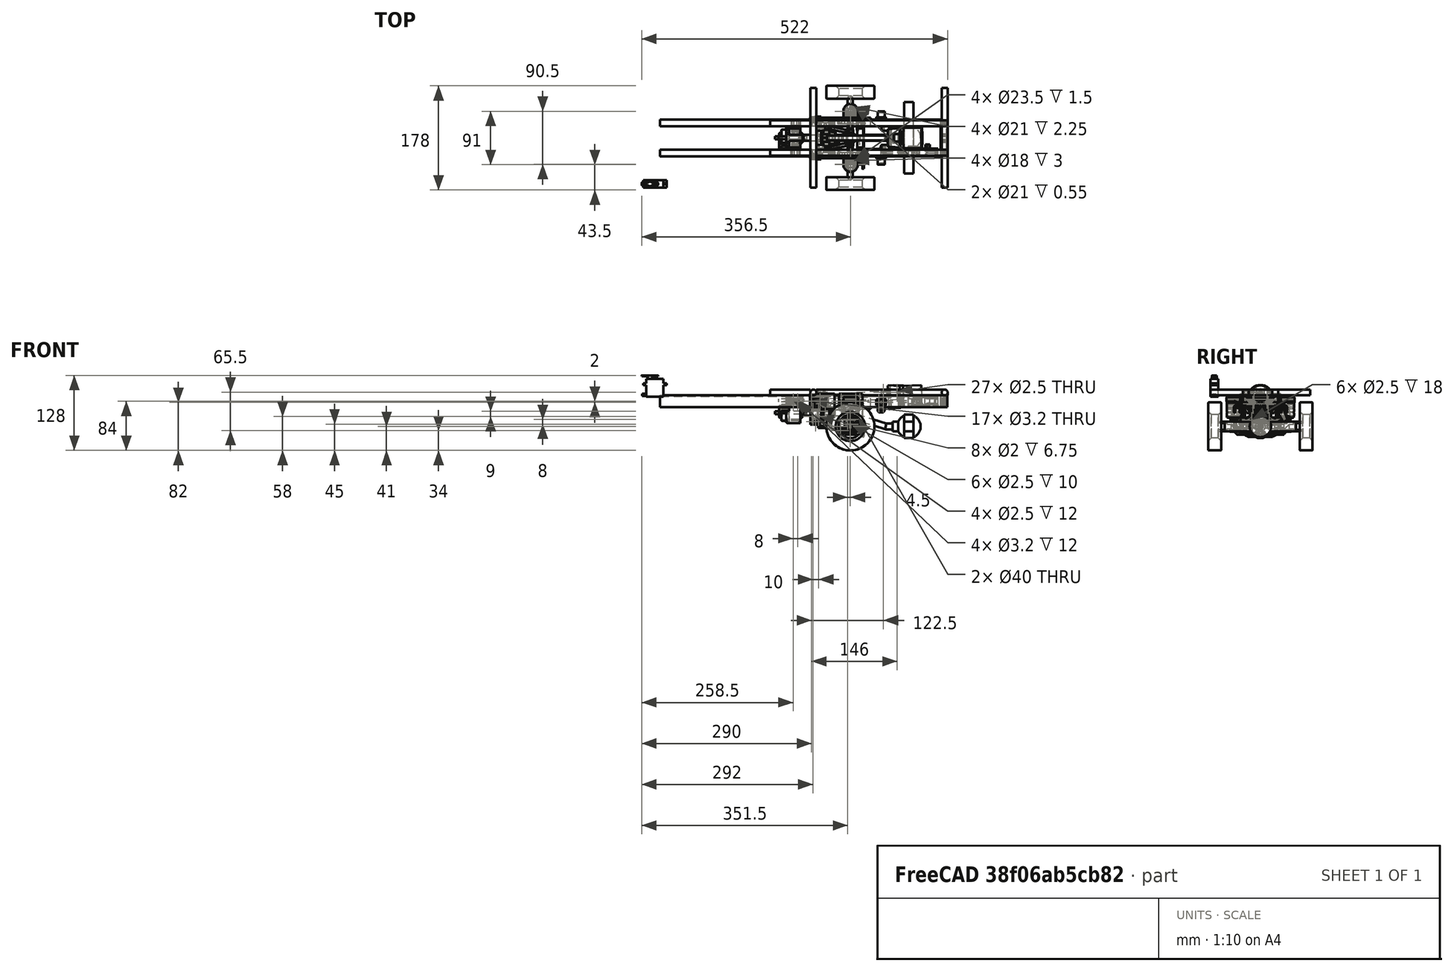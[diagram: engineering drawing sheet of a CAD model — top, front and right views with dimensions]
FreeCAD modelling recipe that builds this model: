
FCSTD DOCUMENT  (FreeCAD 0.17R13522 (Git))
Label: central-axle-lift-02
License: All rights reserved
LicenseURL: http://en.wikipedia.org/wiki/All_rights_reserved
objects: Part::Cylinder×338, Part::Box×195, Part::MultiFuse×193, Part::Cut×182, Part::Fillet×66, Part::Chamfer×49, Part::Torus×34, Part::Mirroring×14, Part::Feature×13, Part::Loft×6, App::DocumentObjectGroup×6, Part::Cone×3, Part::Sphere×1, Part::Extrusion×1
note: 1095 computed .brp shape members not serialized (recipe doc carries the construction recipe); baked Part::Feature solids carry a one-line shape summary decoded from their .brp

FEATURE [Part::Box] Box416  label="Cube641"
  AttacherType = Attacher::AttachEngine3D
  Height = 20
  Length = 490
  Placement = pos=(0,0,-92) rot=(0,0,1;0rad)
  Width = 11.5
FEATURE [Part::Box] Box417  label="Cube642"
  AttacherType = Attacher::AttachEngine3D
  Height = 17
  Length = 490
  Placement = pos=(0,1.5,-90.5) rot=(0,0,1;0rad)
  Width = 10
FEATURE [Part::Cut] Cut429  label="Cut768"
  Base = -> Box416
  Refine = true
  Tool = -> Box417
FEATURE [Part::Fillet] Fillet268
  Base = -> Cut429
  Edges = 2 edges r=3: [Edge11,Edge23]
  Placement = pos=(0,-1.5,0) rot=(0,0,1;0rad)
FEATURE [Part::Box] Box418  label="Cube643"
  AttacherType = Attacher::AttachEngine3D
  Height = 20
  Length = 490
  Placement = pos=(0,0,-92) rot=(0,0,1;0rad)
  Width = 11.5
FEATURE [Part::Box] Box419  label="Cube644"
  AttacherType = Attacher::AttachEngine3D
  Height = 17
  Length = 490
  Placement = pos=(0,1.5,-90.5) rot=(0,0,1;0rad)
  Width = 10
FEATURE [Part::Cut] Cut430  label="Cut769"
  Base = -> Box418
  Refine = true
  Tool = -> Box419
FEATURE [Part::Fillet] Fillet269
  Base = -> Cut430
  Edges = 2 edges r=3: [Edge11,Edge23]
FEATURE [Part::Mirroring] Part__Mirroring036  label="Fillet269 (Mirror #29)"
  Base = (0,0,0)
  Normal = (0,1,0)
  Placement = pos=(0,61.5,0) rot=(0,0,1;0rad)
  Source = -> Fillet269
FEATURE [Part::MultiFuse] Fusion231  label="frame-00"
  Placement = pos=(23.5,55,74) rot=(0,0,1;0rad)
  Refine = true
  Shapes = -> [Part__Mirroring036,Fillet268]
FEATURE [Part::Box] Box494  label="Cube696"
  AttacherType = Attacher::AttachEngine3D
  Height = 10
  Length = 15
  Placement = pos=(340.5,44.5,-63) rot=(0,0,1;0rad)
  Width = 7
FEATURE [Part::Cylinder] Cylinder766  label="Cylinder982"
  Angle = 360
  AttacherType = Attacher::AttachEngine3D
  Height = 10
  Placement = pos=(0,0,0) rot=(0,1,0;1.5708rad)
  Radius = 1.5
FEATURE [Part::Cylinder] Cylinder767  label="Cylinder983"
  Angle = 360
  AttacherType = Attacher::AttachEngine3D
  Height = 10
  Placement = pos=(0,74,0) rot=(0,1,0;1.5708rad)
  Radius = 1.5
FEATURE [Part::MultiFuse] Fusion498
  Placement = pos=(335,48,-59) rot=(0,0,1;0rad)
  Refine = true
  Shapes = -> [Cylinder767,Cylinder766]
FEATURE [Part::Box] Box495  label="Cube697"
  AttacherType = Attacher::AttachEngine3D
  Height = 8
  Length = 9
  Placement = pos=(343.5,28.5,-55) rot=(0,0,1;0rad)
  Width = 7
FEATURE [Part::Box] Box496  label="Cube698"
  AttacherType = Attacher::AttachEngine3D
  Height = 8
  Length = 9
  Placement = pos=(343.5,43.5,-63) rot=(0,0,1;0rad)
  Width = 83
FEATURE [Part::Box] Box497  label="Cube699"
  AttacherType = Attacher::AttachEngine3D
  Height = 8
  Length = 9
  Placement = pos=(343.5,134.5,-55) rot=(0,0,1;0rad)
  Width = 7
FEATURE [Part::Box] Box498  label="Cube700"
  AttacherType = Attacher::AttachEngine3D
  Height = 16
  Length = 9
  Placement = pos=(343.5,13.5,-59) rot=(0,0,1;0rad)
  Width = 15
FEATURE [Part::Box] Box499  label="Cube701"
  AttacherType = Attacher::AttachEngine3D
  Height = 16
  Length = 9
  Placement = pos=(343.5,141.5,-59) rot=(0,0,1;0rad)
  Width = 15
FEATURE [Part::MultiFuse] Fusion499
  Refine = true
  Shapes = -> [Box495,Box498]
FEATURE [Part::MultiFuse] Fusion500
  Refine = true
  Shapes = -> [Box499,Box497]
FEATURE [Part::Box] Box501  label="Cube703"
  AttacherType = Attacher::AttachEngine3D
  Height = 11
  Length = 9
  Placement = pos=(343.5,144,-56.5) rot=(0,0,1;0rad)
  Width = 15
FEATURE [Part::Feature] Face040
  shape: bbox 9.9 x 2e-07 x 8.8 mm, 1 faces, 0 solids (baked)
FEATURE [Part::Feature] Face041
  shape: bbox 9.9 x 2e-07 x 8.8 mm, 1 faces, 0 solids (baked)
FEATURE [Part::Loft] Loft016
  Closed = false
  MaxDegree = 5
  Ruled = false
  Sections = -> [Face040,Face041]
  Solid = true
FEATURE [Part::Feature] Face042
  shape: bbox 9.9 x 2e-07 x 8.8 mm, 1 faces, 0 solids (baked)
FEATURE [Part::Feature] Face043
  shape: bbox 9.9 x 2e-07 x 8.8 mm, 1 faces, 0 solids (baked)
FEATURE [Part::Loft] Loft017
  Closed = false
  MaxDegree = 5
  Ruled = false
  Sections = -> [Face042,Face043]
  Solid = true
FEATURE [Part::MultiFuse] Fusion501
  Refine = true
  Shapes = -> [Fusion499,Loft016]
FEATURE [Part::MultiFuse] Fusion502
  Refine = true
  Shapes = -> [Fusion500,Loft017]
FEATURE [Part::MultiFuse] Fusion503
  Refine = true
  Shapes = -> [Fusion501,Box496,Fusion502]
FEATURE [Part::Fillet] Fillet339
  Base = -> Fusion503
  Edges = 4 edges r=4.49: [Edge18,Edge39,Edge51,Edge65]
FEATURE [Part::Box] Box504  label="Cube706"
  AttacherType = Attacher::AttachEngine3D
  Height = 11
  Length = 9
  Placement = pos=(343.5,11,-56.5) rot=(0,0,1;0rad)
  Width = 15
FEATURE [Part::MultiFuse] Fusion504
  Refine = true
  Shapes = -> [Box501,Box504]
FEATURE [Part::Cut] Cut606  label="Cut878"
  Base = -> Fillet339
  Refine = true
  Tool = -> Fusion504
FEATURE [Part::Box] Box505  label="Cube707"
  AttacherType = Attacher::AttachEngine3D
  Height = 10
  Length = 15
  Placement = pos=(340.5,118.5,-63) rot=(0,0,1;0rad)
  Width = 7
FEATURE [Part::MultiFuse] Fusion505
  Refine = true
  Shapes = -> [Box505,Box494,Cut606]
FEATURE [Part::Cylinder] Cylinder768  label="Cylinder984"
  Angle = 360
  AttacherType = Attacher::AttachEngine3D
  Height = 2.5
  Placement = pos=(0,0,0) rot=(0,1,0;1.5708rad)
  Radius = 2.25
FEATURE [Part::Cylinder] Cylinder769  label="Cylinder985"
  Angle = 360
  AttacherType = Attacher::AttachEngine3D
  Height = 2.5
  Placement = pos=(0,74,0) rot=(0,1,0;1.5708rad)
  Radius = 2.25
FEATURE [Part::MultiFuse] Fusion506
  Placement = pos=(348,48,-53) rot=(0,1,0;1.5708rad)
  Refine = true
  Shapes = -> [Cylinder769,Cylinder768]
FEATURE [Part::Cut] Cut607  label="Cut879"
  Base = -> Fusion505
  Refine = true
  Tool = -> Fusion498
FEATURE [Part::Cut] Cut608  label="Cut880"
  Base = -> Cut607
  Refine = true
  Tool = -> Fusion506
FEATURE [Part::Cylinder] Cylinder807  label="Cylinder986"
  Angle = 360
  AttacherType = Attacher::AttachEngine3D
  Height = 1.5
  Placement = pos=(348,48,-64.5) rot=(0,0,1;0rad)
  Radius = 1.5
FEATURE [Part::Cylinder] Cylinder808  label="Cylinder987"
  Angle = 360
  AttacherType = Attacher::AttachEngine3D
  Height = 1.5
  Placement = pos=(348,122,-64.5) rot=(0,0,1;0rad)
  Radius = 1.5
FEATURE [Part::MultiFuse] Fusion523
  Refine = true
  Shapes = -> [Cylinder808,Cylinder807]
FEATURE [Part::Cylinder] Cylinder288
  Angle = 360
  AttacherType = Attacher::AttachEngine3D
  Height = 22
  Placement = pos=(0,0,0) rot=(1,0,0;1.5708rad)
  Radius = 41
FEATURE [Part::Cylinder] Cylinder289
  Angle = 360
  AttacherType = Attacher::AttachEngine3D
  Height = 22
  Placement = pos=(0,0,0) rot=(1,0,0;1.5708rad)
  Radius = 41
FEATURE [Part::Cylinder] Cylinder290
  Angle = 360
  AttacherType = Attacher::AttachEngine3D
  Height = 22
  Placement = pos=(0,0,0) rot=(1,0,0;1.5708rad)
  Radius = 20
FEATURE [Part::Cut] Cut427  label="Cut766"
  Base = -> Cylinder289
  Refine = true
  Tool = -> Cylinder290
FEATURE [Part::Fillet] Fillet267  label="wheel-007"
  Base = -> Cut427
  Edges = 2 edges r=1: [Edge1,Edge3]
  Placement = pos=(0,174,0) rot=(0,0,1;0rad)
FEATURE [Part::Cylinder] Cylinder291
  Angle = 360
  AttacherType = Attacher::AttachEngine3D
  Height = 22
  Placement = pos=(0,0,0) rot=(1,0,0;1.5708rad)
  Radius = 20
FEATURE [Part::Cut] Cut428  label="Cut767"
  Base = -> Cylinder288
  Refine = true
  Tool = -> Cylinder291
FEATURE [Part::Fillet] Fillet266  label="wheel-006"
  Base = -> Cut428
  Edges = 2 edges r=1: [Edge1,Edge3]
  Placement = pos=(0,18,0) rot=(0,0,1;0rad)
FEATURE [Part::MultiFuse] Fusion244
  Placement = pos=(348,0,-51) rot=(0,0,1;0rad)
  Refine = true
  Shapes = -> [Fillet266,Fillet267]
FEATURE [Part::Chamfer] Chamfer056  label="whees-middle"
  Base = -> Fusion244
  Edges = 4 edges r=5: [Edge8,Edge9,Edge18,Edge19]
FEATURE [Part::Box] Box512  label="Cube712"
  AttacherType = Attacher::AttachEngine3D
  Height = 10
  Length = 15
  Placement = pos=(340.5,44.5,-63) rot=(0,0,1;0rad)
  Width = 7
FEATURE [Part::Cylinder] Cylinder780  label="Cylinder896"
  Angle = 360
  AttacherType = Attacher::AttachEngine3D
  Height = 10
  Placement = pos=(332.5,48,-59) rot=(0,1,0;1.5708rad)
  Radius = 1.5
FEATURE [Part::Box] Box513  label="Cube713"
  AttacherType = Attacher::AttachEngine3D
  Height = 8
  Length = 9
  Placement = pos=(343.5,38.5,-63) rot=(0,0,1;0rad)
  Width = 25
FEATURE [Part::Box] Box514  label="Cube714"
  AttacherType = Attacher::AttachEngine3D
  Height = 12
  Length = 14
  Placement = pos=(338.5,44.5,-65) rot=(0,0,1;0rad)
  Width = 16
FEATURE [Part::Cylinder] Cylinder797  label="Cylinder988"
  Angle = 360
  AttacherType = Attacher::AttachEngine3D
  Height = 3
  Placement = pos=(348.5,40,-38.5) rot=(0,0,1;0rad)
  Radius = 8
FEATURE [Part::MultiFuse] Fusion518
  Refine = true
  Shapes = -> [Box513,Cylinder780,Box512]
FEATURE [Part::Box] Box523  label="Cube723"
  AttacherType = Attacher::AttachEngine3D
  Height = 17.5
  Length = 14
  Placement = pos=(338.5,44.5,-53) rot=(0,0,1;0rad)
  Width = 16
FEATURE [Part::Box] Box524  label="Cube724"
  AttacherType = Attacher::AttachEngine3D
  Height = 10
  Length = 26
  Placement = pos=(326.5,51.5,-63) rot=(0,0,1;0rad)
  Width = 5
FEATURE [Part::Fillet] Fillet352
  Base = -> Box524
  Edges = 2 edges r=4.99: [Edge2,Edge4]
  Placement = pos=(0,4,0) rot=(0,0,1;0rad)
FEATURE [Part::Cylinder] Cylinder798  label="Cylinder989"
  Angle = 360
  AttacherType = Attacher::AttachEngine3D
  Height = 10
  Placement = pos=(348.5,40,-44) rot=(0,0,1;0rad)
  Radius = 1.25
FEATURE [Part::Cylinder] Cylinder800  label="Cylinder903"
  Angle = 360
  AttacherType = Attacher::AttachEngine3D
  Height = 10
  Placement = pos=(331.5,60.5,-58) rot=(1,0,0;1.5708rad)
  Radius = 1.25
FEATURE [Part::Cylinder] Cylinder801  label="Cylinder990"
  Angle = 360
  AttacherType = Attacher::AttachEngine3D
  Height = 10
  Placement = pos=(343.5,56,-40) rot=(1,0,0;1.5708rad)
  Radius = 1.25
FEATURE [Part::Cylinder] Cylinder802  label="Cylinder991"
  Angle = 360
  AttacherType = Attacher::AttachEngine3D
  Height = 10
  Placement = pos=(342.5,51.5,-50) rot=(0,1,0;1.5708rad)
  Radius = 1.25
FEATURE [Part::Cylinder] Cylinder806  label="Cylinder992"
  Angle = 360
  AttacherType = Attacher::AttachEngine3D
  Height = 10
  Placement = pos=(342.5,51.5,-42) rot=(0,1,0;1.5708rad)
  Radius = 1.25
FEATURE [Part::Cylinder] Cylinder810  label="Cylinder993"
  Angle = 360
  AttacherType = Attacher::AttachEngine3D
  Height = 2
  Placement = pos=(348.5,48,-65) rot=(0,0,1;0rad)
  Radius = 2.1
FEATURE [Part::Cylinder] Cylinder
  Angle = 360
  AttacherType = Attacher::AttachEngine3D
  Height = 5
  Placement = pos=(291.5,51.5,-48) rot=(1,0,0;1.5708rad)
  Radius = 5
FEATURE [Part::Cylinder] Cylinder783
  Angle = 360
  AttacherType = Attacher::AttachEngine3D
  Height = 5
  Placement = pos=(336.5,51.5,-48) rot=(1,0,0;1.5708rad)
  Radius = 5
FEATURE [Part::Box] Box526  label="Cube726"
  AttacherType = Attacher::AttachEngine3D
  Height = 6
  Length = 45
  Placement = pos=(291.5,46.5,-51) rot=(0,0,1;0rad)
  Width = 5
FEATURE [Part::Cylinder] Cylinder784
  Angle = 360
  AttacherType = Attacher::AttachEngine3D
  Height = 5
  Placement = pos=(291.5,51.5,-48) rot=(1,0,0;1.5708rad)
  Radius = 3.1
FEATURE [Part::Cylinder] Cylinder785
  Angle = 360
  AttacherType = Attacher::AttachEngine3D
  Height = 5
  Placement = pos=(336.5,51.5,-48) rot=(1,0,0;1.5708rad)
  Radius = 3.1
FEATURE [Part::MultiFuse] Fusion
  Refine = true
  Shapes = -> [Cylinder,Cylinder783,Box526]
FEATURE [Part::MultiFuse] Fusion511
  Refine = true
  Shapes = -> [Cylinder784,Cylinder785]
FEATURE [Part::Cut] Cut
  Base = -> Fusion
  Refine = true
  Tool = -> Fusion511
FEATURE [Part::Box] Box042  label="Cube280"
  AttacherType = Attacher::AttachEngine3D
  Height = 28
  Length = 21
  Placement = pos=(-13,0,0) rot=(0,0,1;0rad)
  Width = 170
FEATURE [Part::Fillet] Fillet013
  Base = -> Box042
  Edges = 2 edges r=15: [Edge1,Edge3]
FEATURE [Part::Box] Box184  label="Cube410"
  AttacherType = Attacher::AttachEngine3D
  Height = 10
  Length = 2.5
  Placement = pos=(-1.25,0,0) rot=(0,0,1;0rad)
  Width = 4
FEATURE [Part::Cylinder] Cylinder068
  Angle = 360
  AttacherType = Attacher::AttachEngine3D
  Height = 10
  Placement = pos=(0,4,0) rot=(0,0,1;0rad)
  Radius = 1.25
FEATURE [Part::Cylinder] Cylinder069
  Angle = 360
  AttacherType = Attacher::AttachEngine3D
  Height = 10
  Radius = 1.25
FEATURE [Part::MultiFuse] Fusion056
  Placement = pos=(0,8,0) rot=(0,0,1;0rad)
  Refine = true
  Shapes = -> [Box184,Cylinder068,Cylinder069]
FEATURE [Part::Box] Box527  label="Cube727"
  AttacherType = Attacher::AttachEngine3D
  Height = 16
  Length = 16
  Placement = pos=(90,24,-59) rot=(0,0,1;0rad)
  Width = 122
FEATURE [Part::Cylinder] Cylinder795  label="Cylinder994"
  Angle = 360
  AttacherType = Attacher::AttachEngine3D
  Height = 16
  Placement = pos=(90,85,-51) rot=(0,1,0;1.5708rad)
  Radius = 20
FEATURE [Part::Sphere] Sphere001
  Angle1 = -90
  Angle2 = 90
  Angle3 = 360
  AttacherType = Attacher::AttachEngine3D
  Placement = pos=(98,85,-51) rot=(0,0,1;0rad)
  Radius = 20
FEATURE [Part::Cylinder] Cylinder796  label="Cylinder995"
  Angle = 360
  AttacherType = Attacher::AttachEngine3D
  Height = 28
  Placement = pos=(70,85,-51) rot=(0,1,0;1.5708rad)
  Radius = 8.5
FEATURE [Part::MultiFuse] Fusion513  label="rear-axle"
  Placement = pos=(350,0,0) rot=(0,0,1;0rad)
  Refine = true
  Shapes = -> [Box527,Sphere001,Cylinder796,Cylinder795]
FEATURE [Part::Cut] Cut014047  label="diff-box-rear-01"
  Placement = pos=(0,0,-1) rot=(0,0,1;0rad)
  Refine = true
FEATURE [Part::Fillet] Fillet355  label="diff-box-front-01"
  Edges = 1 edges r=1.99: [Edge305]
FEATURE [Part::Cylinder] Cylinder088
  Angle = 360
  AttacherType = Attacher::AttachEngine3D
  Height = 43.5
  Placement = pos=(20.75,0,-18.5) rot=(0,0,1;0rad)
  Radius = 2.5
FEATURE [Part::Cylinder] Cylinder087
  Angle = 360
  AttacherType = Attacher::AttachEngine3D
  Height = 54
  Placement = pos=(0,0,-23.5) rot=(0,0,1;0rad)
  Radius = 2.5
FEATURE [Part::Cut] Cut014020  label="diff-box-mount-left"
  Base = -> Fillet013
  Placement = pos=(0,0,-1) rot=(0,0,1;0rad)
  Refine = true
  Tool = -> Fusion056
FEATURE [Part::Mirroring] Part__Mirroring001  label="diff-box-mount-right"
  Base = (0,0,0)
  Normal = (0,1,0)
  Placement = pos=(0,0,-1) rot=(0,0,1;0rad)
FEATURE [Part::MultiFuse] Fusion514  label="gearbox"
  Placement = pos=(250,85,-27.5) rot=(0,-1,0;1.5708rad)
  Refine = true
  Shapes = -> [Cut014047,Fillet355,Cylinder087,Cylinder088,Cut014020,Part__Mirroring001]
FEATURE [Part::Cylinder] Cylinder811  label="Cylinder996"
  Angle = 360
  AttacherType = Attacher::AttachEngine3D
  Height = 12
  Placement = pos=(408,85,-54) rot=(0,1,0;1.5708rad)
  Radius = 5
FEATURE [Part::Cylinder] Cylinder812  label="Cylinder997"
  Angle = 360
  AttacherType = Attacher::AttachEngine3D
  Height = 12
  Placement = pos=(268,85,-30.5) rot=(0,1,0;1.5708rad)
  Radius = 5
FEATURE [Part::Cylinder] Cylinder813  label="Cylinder998"
  Angle = 360
  AttacherType = Attacher::AttachEngine3D
  Height = 78
  Placement = pos=(334,85,-30.5) rot=(0,1,0;1.87623rad)
  Radius = 5
FEATURE [Part::Cylinder] Cylinder817  label="Cylinder999"
  Angle = 360
  AttacherType = Attacher::AttachEngine3D
  Height = 40
  Placement = pos=(361,105,-46.5) rot=(1,0,0;1.5708rad)
  Radius = 1.5
FEATURE [Part::Cylinder] Cylinder818  label="Cylinder1000"
  Angle = 360
  AttacherType = Attacher::AttachEngine3D
  Height = 12
  Placement = pos=(322,85,-30.5) rot=(0,1,0;1.5708rad)
  Radius = 5
FEATURE [Part::Cylinder] Cylinder819  label="Cylinder1001"
  Angle = 360
  AttacherType = Attacher::AttachEngine3D
  Height = 30
  Placement = pos=(292,85,-30.5) rot=(0,1,0;1.5708rad)
  Radius = 2.5
FEATURE [Part::Cylinder] Cylinder820  label="Cylinder1002"
  Angle = 360
  AttacherType = Attacher::AttachEngine3D
  Height = 12
  Placement = pos=(280,85,-30.5) rot=(0,1,0;1.5708rad)
  Radius = 5
FEATURE [Part::Cylinder] Cylinder821  label="Cylinder1003"
  Angle = 360
  AttacherType = Attacher::AttachEngine3D
  Height = 15
  Placement = pos=(370,47.5,-46.5) rot=(1,0,0;1.5708rad)
  Radius = 1.5
FEATURE [Part::Cylinder] Cylinder822  label="Cylinder1004"
  Angle = 360
  AttacherType = Attacher::AttachEngine3D
  Height = 15
  Placement = pos=(370,137.5,-46.5) rot=(1,0,0;1.5708rad)
  Radius = 1.5
FEATURE [Part::Feature] Face
  shape: bbox 3.476 x 2e-07 x 3.258 mm, 1 faces, 0 solids (baked)
FEATURE [Part::Feature] Face044
  shape: bbox 3.476 x 2e-07 x 3.258 mm, 1 faces, 0 solids (baked)
FEATURE [Part::Feature] Face045
  shape: bbox 3.476 x 2e-07 x 3.258 mm, 1 faces, 0 solids (baked)
FEATURE [Part::Feature] Face046
  shape: bbox 3.551 x 2e-07 x 3.372 mm, 1 faces, 0 solids (baked)
FEATURE [Part::Loft] Loft
  Closed = false
  MaxDegree = 5
  Ruled = false
  Sections = -> [Face,Face044]
  Solid = true
FEATURE [Part::Loft] Loft018
  Closed = false
  MaxDegree = 5
  Ruled = false
  Sections = -> [Face045,Face046]
  Solid = true
FEATURE [Part::MultiFuse] Fusion528
  Placement = pos=(323.5,0,-428.5) rot=(0,-1,0;1.5708rad)
  Refine = true
  Shapes = -> [Cylinder817,Cylinder821,Cylinder822,Loft,Loft018]
FEATURE [Part::Box] Box558  label="Cube749"
  AttacherType = Attacher::AttachEngine3D
  Height = 10
  Length = 10
  Placement = pos=(312,57,-28) rot=(0,0,1;0rad)
  Width = 56
FEATURE [Part::Cylinder] Cylinder823  label="Cylinder1005"
  Angle = 360
  AttacherType = Attacher::AttachEngine3D
  Height = 1
  Placement = pos=(317,85,-30.5) rot=(0,1,0;1.5708rad)
  Radius = 4
FEATURE [Part::Cylinder] Cylinder824  label="Cylinder1006"
  Angle = 360
  AttacherType = Attacher::AttachEngine3D
  Height = 5
  Placement = pos=(317,85,-27.5) rot=(0,1,0;1.5708rad)
  Radius = 8
FEATURE [Part::Cylinder] Cylinder825  label="Cylinder1007"
  Angle = 360
  AttacherType = Attacher::AttachEngine3D
  Height = 4
  Placement = pos=(313,85,-30.5) rot=(0,1,0;1.5708rad)
  Radius = 5.6
FEATURE [Part::MultiFuse] Fusion531
  Placement = pos=(4,0,3) rot=(0,0,1;0rad)
  Refine = true
  Shapes = -> [Cylinder823,Cylinder825]
FEATURE [Part::Fillet] Fillet
  Base = -> Cut
  Edges = 4 edges r=2.49: [Edge1,Edge3,Edge7,Edge15]
FEATURE [Part::Fillet] Fillet356  label="central-axle-left-lower-bar"
  Base = -> Fillet
  Edges = 6 edges r=0.75: [Edge10,Edge11,Edge12,Edge13,Edge24,Edge25]
  Placement = pos=(30.1998,4,99.6027) rot=(0,1,0;0.340339rad)
FEATURE [Part::Box] Box559  label="Cube750"
  AttacherType = Attacher::AttachEngine3D
  Height = 5
  Length = 22
  Placement = pos=(341.5,77,-65) rot=(0,0,1;0rad)
  Width = 16
FEATURE [Part::Box] Box560  label="Cube751"
  AttacherType = Attacher::AttachEngine3D
  Height = 1.8
  Length = 9
  Placement = pos=(343.5,77,-63) rot=(0,0,1;0rad)
  Width = 16
FEATURE [Part::Box] Box561  label="Cube752"
  AttacherType = Attacher::AttachEngine3D
  Height = 2.8
  Length = 9
  Placement = pos=(343.5,84,-61.2) rot=(0,0,1;0rad)
  Width = 2
FEATURE [Part::Box] Box562  label="Cube753"
  AttacherType = Attacher::AttachEngine3D
  Height = 2.8
  Length = 8
  Placement = pos=(344,77,-61.2) rot=(0,0,1;0rad)
  Width = 16
FEATURE [Part::MultiFuse] Fusion532
  Refine = true
  Shapes = -> [Box560,Box562,Box561]
FEATURE [Part::Box] Box564  label="Cube755"
  AttacherType = Attacher::AttachEngine3D
  Height = 8
  Length = 2
  Placement = pos=(363.5,77,-65) rot=(0,0,1;0rad)
  Width = 16
FEATURE [Part::Cut] Cut014048
  Base = -> Box559
  Refine = true
  Tool = -> Fusion532
FEATURE [Part::Box] Box565  label="Cube756"
  AttacherType = Attacher::AttachEngine3D
  Height = 11
  Length = 12
  Placement = pos=(353.5,77,-65) rot=(0,0,1;0rad)
  Width = 4
FEATURE [Part::Box] Box566  label="Cube757"
  AttacherType = Attacher::AttachEngine3D
  Height = 11
  Length = 12
  Placement = pos=(353.5,89,-65) rot=(0,0,1;0rad)
  Width = 4
FEATURE [Part::MultiFuse] Fusion534
  Refine = true
  Shapes = -> [Box565,Box566]
FEATURE [Part::MultiFuse] Fusion535
  Refine = true
  Shapes = -> [Cut014048,Box564]
FEATURE [Part::Cut] Cut014049
  Base = -> Fusion535
  Refine = true
  Tool = -> Fusion534
FEATURE [Part::Fillet] Fillet357
  Base = -> Cut014049
  Edges = 2 edges r=2: [Edge4,Edge34]
FEATURE [Part::Chamfer] Chamfer099
  Base = -> Fillet357
  Edges = 2 edges r=3.99: [Edge43,Edge70]
FEATURE [Part::Chamfer] Chamfer100
  Base = -> Chamfer099
  Edges = 4 edges r=0.49: [Edge68,Edge76,Edge85,Edge87]
FEATURE [Part::Chamfer] Chamfer101  label="central-axle-steering-arm-support"
  Base = -> Chamfer100
  Edges = 1 edges r=1.75: [Edge102]
FEATURE [Part::MultiFuse] Fusion536  label="rear-prop-shaft"
  Placement = pos=(0,0,3) rot=(0,0,1;0rad)
  Refine = true
  Shapes = -> [Cylinder811,Cylinder812,Cylinder813,Cylinder818,Cylinder819,Cylinder820]
FEATURE [Part::Box] Box568  label="Cube759"
  AttacherType = Attacher::AttachEngine3D
  Height = 6
  Length = 6
  Placement = pos=(294,63.5,-2) rot=(0,0,1;0rad)
  Width = 5
FEATURE [Part::Cylinder] Cylinder831
  Angle = 360
  AttacherType = Attacher::AttachEngine3D
  Height = 5
  Placement = pos=(291.5,68.5,1) rot=(1,0,0;1.5708rad)
  Radius = 5
FEATURE [Part::Fillet] Fillet358
  Base = -> Box568
  Edges = 4 edges r=2.49: [Edge9,Edge10,Edge11,Edge12]
FEATURE [Part::Fillet] Fillet360
  Base = -> Cylinder831
  Edges = 2 edges r=0.75: [Edge1,Edge3]
FEATURE [Part::Cylinder] Cylinder841
  Angle = 360
  AttacherType = Attacher::AttachEngine3D
  Height = 5
  Placement = pos=(291.5,51.5,-48) rot=(1,0,0;1.5708rad)
  Radius = 5
FEATURE [Part::Cylinder] Cylinder842
  Angle = 360
  AttacherType = Attacher::AttachEngine3D
  Height = 5
  Placement = pos=(336.5,51.5,-48) rot=(1,0,0;1.5708rad)
  Radius = 5
FEATURE [Part::Box] Box572  label="Cube763"
  AttacherType = Attacher::AttachEngine3D
  Height = 6
  Length = 45
  Placement = pos=(291.5,46.5,-51) rot=(0,0,1;0rad)
  Width = 5
FEATURE [Part::Cylinder] Cylinder843
  Angle = 360
  AttacherType = Attacher::AttachEngine3D
  Height = 5
  Placement = pos=(291.5,51.5,-48) rot=(1,0,0;1.5708rad)
  Radius = 3.1
FEATURE [Part::Cylinder] Cylinder844
  Angle = 360
  AttacherType = Attacher::AttachEngine3D
  Height = 5
  Placement = pos=(336.5,51.5,-48) rot=(1,0,0;1.5708rad)
  Radius = 3.1
FEATURE [Part::MultiFuse] Fusion545
  Refine = true
  Shapes = -> [Cylinder841,Cylinder842,Box572]
FEATURE [Part::MultiFuse] Fusion546
  Refine = true
  Shapes = -> [Cylinder843,Cylinder844]
FEATURE [Part::Cut] Cut014051
  Base = -> Fusion545
  Refine = true
  Tool = -> Fusion546
FEATURE [Part::Fillet] Fillet364
  Base = -> Cut014051
  Edges = 4 edges r=2.49: [Edge1,Edge3,Edge7,Edge15]
FEATURE [Part::Fillet] Fillet365  label="central-axle-right-lower-bar"
  Base = -> Fillet364
  Edges = 6 edges r=0.75: [Edge10,Edge11,Edge12,Edge13,Edge24,Edge25]
  Placement = pos=(30.1998,68,99.6027) rot=(0,1,0;0.340339rad)
FEATURE [Part::MultiFuse] Fusion547
  Placement = pos=(0,1.75,0) rot=(0,0,1;0rad)
  Refine = true
  Shapes = -> [Fillet360,Fillet358]
FEATURE [Part::Box] Box575  label="Cube766"
  AttacherType = Attacher::AttachEngine3D
  Height = 6
  Length = 6
  Placement = pos=(294,63.5,-2) rot=(0,0,1;0rad)
  Width = 5
FEATURE [Part::Cylinder] Cylinder846
  Angle = 360
  AttacherType = Attacher::AttachEngine3D
  Height = 5
  Placement = pos=(291.5,68.5,1) rot=(1,0,0;1.5708rad)
  Radius = 5
FEATURE [Part::Fillet] Fillet368
  Base = -> Box575
  Edges = 4 edges r=2.49: [Edge9,Edge10,Edge11,Edge12]
FEATURE [Part::Fillet] Fillet369
  Base = -> Cylinder846
  Edges = 2 edges r=0.75: [Edge1,Edge3]
FEATURE [Part::MultiFuse] Fusion549
  Placement = pos=(628,7.5,2) rot=(0,1,0;3.14159rad)
  Refine = true
  Shapes = -> [Fillet369,Fillet368]
FEATURE [Part::Cylinder] Cylinder839
  Angle = 360
  AttacherType = Attacher::AttachEngine3D
  Height = 5
  Placement = pos=(291.5,70.25,1) rot=(1,0,0;1.5708rad)
  Radius = 3.1
FEATURE [Part::Cylinder] Cylinder847
  Angle = 360
  AttacherType = Attacher::AttachEngine3D
  Height = 5
  Placement = pos=(336.5,76,1) rot=(1,0,0;1.5708rad)
  Radius = 3.1
FEATURE [Part::MultiFuse] Fusion551
  Refine = true
  Shapes = -> [Cylinder839,Cylinder847]
FEATURE [Part::Feature] Face047
  Placement = pos=(0,1.5,0) rot=(0,0,1;0rad)
  shape: bbox 2e-07 x 5.5 x 6.6 mm, 1 faces, 0 solids (baked)
FEATURE [Part::Feature] Face048
  Placement = pos=(0,1.75,0) rot=(0,0,1;0rad)
  shape: bbox 2e-07 x 5.5 x 6.6 mm, 1 faces, 0 solids (baked)
FEATURE [Part::Cylinder] Cylinder851  label="Cylinder1008"
  Angle = 360
  AttacherType = Attacher::AttachEngine3D
  Height = 5
  Placement = pos=(312,85,-27.5) rot=(0,1,0;1.5708rad)
  Radius = 6.5
FEATURE [Part::Cut] Cut014053
  Base = -> Box558
  Refine = true
  Tool = -> Cylinder851
FEATURE [Part::MultiFuse] Fusion553
  Refine = true
  Shapes = -> [Cut014053,Cylinder824]
FEATURE [Part::Cut] Cut014054
  Base = -> Fusion553
  Refine = true
  Tool = -> Fusion531
FEATURE [Part::Chamfer] Chamfer102
  Base = -> Cut014054
  Edges = 2 edges r=6: [Edge14,Edge19]
FEATURE [Part::Chamfer] Chamfer103
  Base = -> Chamfer102
  Edges = 2 edges r=5: [Edge3,Edge35]
FEATURE [Part::Cylinder] Cylinder852  label="Cylinder1009"
  Angle = 360
  AttacherType = Attacher::AttachEngine3D
  Height = 20
  Placement = pos=(311,101,-13.5) rot=(0,1,0;2.0944rad)
  Radius = 5.5
FEATURE [Part::Cylinder] Cylinder853  label="Cylinder1010"
  Angle = 360
  AttacherType = Attacher::AttachEngine3D
  Height = 20
  Placement = pos=(311,69,-13.5) rot=(0,1,0;2.0944rad)
  Radius = 5.5
FEATURE [Part::Box] Box578  label="Cube769"
  AttacherType = Attacher::AttachEngine3D
  Height = 8
  Length = 8
  Placement = pos=(344.5,39.5,-45) rot=(0,0,1;0rad)
  Width = 8
FEATURE [Part::Chamfer] Chamfer104
  Base = -> Box578
  Edges = 1 edges r=7.99: [Edge9]
  Placement = pos=(0,-2,1) rot=(0,0,1;0rad)
FEATURE [Part::Cylinder] Cylinder864  label="Cylinder1011"
  Angle = 360
  AttacherType = Attacher::AttachEngine3D
  Height = 7
  Placement = pos=(348.5,40,-45.5) rot=(0,0,1;0rad)
  Radius = 3.1
FEATURE [Part::Cylinder] Cylinder865  label="Cylinder1012"
  Angle = 360
  AttacherType = Attacher::AttachEngine3D
  Height = 10
  Placement = pos=(348,60.5,-47) rot=(1,0,0;1.5708rad)
  Radius = 1.25
FEATURE [Part::Cylinder] Cylinder866  label="Cylinder1013"
  Angle = 360
  AttacherType = Attacher::AttachEngine3D
  Height = 10
  Placement = pos=(348,60.5,-39) rot=(1,0,0;1.5708rad)
  Radius = 1.25
FEATURE [Part::Cylinder] Cylinder867  label="Cylinder1014"
  Angle = 360
  AttacherType = Attacher::AttachEngine3D
  Height = 10
  Placement = pos=(331.5,59.5,-58) rot=(1,0,0;1.5708rad)
  Radius = 2.1
FEATURE [Part::MultiFuse] Fusion567
  Refine = true
  Shapes = -> [Box523,Cylinder797,Box514,Fillet352,Chamfer104]
FEATURE [Part::Cut] Cut014059
  Base = -> Fusion567
  Refine = true
  Tool = -> Fusion518
FEATURE [Part::MultiFuse] Fusion568
  Refine = true
  Shapes = -> [Cylinder810,Cylinder798,Cylinder800,Cylinder801,Cylinder802,Cylinder806,Cylinder865,Cylinder866,Cylinder867,Cylinder864]
FEATURE [Part::Cut] Cut014060  label="central-axle-left-baloon-support"
  Base = -> Cut014059
  Refine = true
  Tool = -> Fusion568
FEATURE [Part::Box] Box579  label="Cube770"
  AttacherType = Attacher::AttachEngine3D
  Height = 19.5
  Length = 9
  Placement = pos=(343.5,60.5,-55) rot=(0,0,1;0rad)
  Width = 17.5
FEATURE [Part::Box] Box580  label="Cube771"
  AttacherType = Attacher::AttachEngine3D
  Height = 13.5
  Length = 9
  Placement = pos=(343.5,68,-35.5) rot=(0,0,1;0rad)
  Width = 2.75
FEATURE [Part::Box] Box581  label="Cube772"
  AttacherType = Attacher::AttachEngine3D
  Height = 3
  Length = 9
  Placement = pos=(343.5,68,-35.5) rot=(0,0,1;0rad)
  Width = 10
FEATURE [Part::Box] Box582  label="Cube773"
  AttacherType = Attacher::AttachEngine3D
  Height = 13.5
  Length = 9
  Placement = pos=(343.5,76.25,-35.5) rot=(0,0,1;0rad)
  Width = 1.75
FEATURE [Part::Chamfer] Chamfer105
  Base = -> Box579
  Edges = 1 edges r=15: [Edge11]
FEATURE [Part::MultiFuse] Fusion569
  Refine = true
  Shapes = -> [Box580,Box581,Box582]
FEATURE [Part::Cylinder] Cylinder868  label="Cylinder1015"
  Angle = 360
  AttacherType = Attacher::AttachEngine3D
  Height = 18
  Placement = pos=(348,78.5,-47) rot=(1,0,0;1.5708rad)
  Radius = 1.25
FEATURE [Part::Cylinder] Cylinder869  label="Cylinder1016"
  Angle = 360
  AttacherType = Attacher::AttachEngine3D
  Height = 18
  Placement = pos=(348,78.5,-39) rot=(1,0,0;1.5708rad)
  Radius = 1.25
FEATURE [Part::Cylinder] Cylinder870  label="Cylinder1017"
  Angle = 360
  AttacherType = Attacher::AttachEngine3D
  Height = 18
  Placement = pos=(348,84.5,-47) rot=(1,0,0;1.5708rad)
  Radius = 3.1
FEATURE [Part::Cylinder] Cylinder871  label="Cylinder1018"
  Angle = 360
  AttacherType = Attacher::AttachEngine3D
  Height = 18
  Placement = pos=(348,84.5,-39) rot=(1,0,0;1.5708rad)
  Radius = 3.1
FEATURE [Part::MultiFuse] Fusion571
  Refine = true
  Shapes = -> [Chamfer105,Fusion569]
FEATURE [Part::Fillet] Fillet374
  Base = -> Fusion571
  Edges = 1 edges r=6: [Edge2]
FEATURE [Part::Fillet] Fillet375
  Base = -> Fillet374
  Edges = 4 edges r=3: [Edge9,Edge14,Edge21,Edge27]
FEATURE [Part::Chamfer] Chamfer106
  Base = -> Fillet375
  Edges = 1 edges r=3: [Edge40]
FEATURE [Part::Cylinder] Cylinder872  label="Cylinder1361"
  Angle = 360
  AttacherType = Attacher::AttachEngine3D
  Height = 18
  Placement = pos=(348,78.5,-27) rot=(1,0,0;1.5708rad)
  Radius = 1.25
FEATURE [Part::MultiFuse] Fusion572
  Refine = true
  Shapes = -> [Cylinder872,Cylinder869,Cylinder870,Cylinder871,Cylinder868]
FEATURE [Part::Cut] Cut014061  label="central-axle-left-upper-bar-support"
  Base = -> Chamfer106
  Refine = true
  Tool = -> Fusion572
FEATURE [Part::Box] Box583  label="Cube774"
  AttacherType = Attacher::AttachEngine3D
  Height = 30
  Length = 18
  Placement = pos=(280,48.5,-48) rot=(0,0,1;0rad)
  Width = 1.75
FEATURE [Part::Chamfer] Chamfer107
  Base = -> Box583
  Edges = 1 edges r=5: [Edge8]
FEATURE [Part::Cylinder] Cylinder873  label="Cylinder1020"
  Angle = 360
  AttacherType = Attacher::AttachEngine3D
  Height = 9
  Placement = pos=(289,57.5,-43) rot=(1,0,0;1.5708rad)
  Radius = 2.1
FEATURE [Part::Box] Box584  label="Cube775"
  AttacherType = Attacher::AttachEngine3D
  Height = 19
  Length = 18
  Placement = pos=(280,49.5,-37) rot=(0,0,1;0rad)
  Width = 4
FEATURE [Part::Box] Box585  label="Cube776"
  AttacherType = Attacher::AttachEngine3D
  Height = 26.75
  Length = 18
  Placement = pos=(280,48.5,-48) rot=(0,0,1;0rad)
  Width = 2.75
FEATURE [Part::Chamfer] Chamfer108
  Base = -> Box585
  Edges = 1 edges r=5: [Edge8]
  Placement = pos=(0,7.25,0) rot=(0,0,1;0rad)
FEATURE [Part::Box] Box586  label="Cube777"
  AttacherType = Attacher::AttachEngine3D
  Height = 11
  Length = 3
  Placement = pos=(280,49.5,-48) rot=(0,0,1;0rad)
  Width = 4
FEATURE [Part::Cylinder] Cylinder874  label="Cylinder1021"
  Angle = 360
  AttacherType = Attacher::AttachEngine3D
  Height = 12
  Placement = pos=(289,60.5,-43) rot=(1,0,0;1.5708rad)
  Radius = 1.25
FEATURE [Part::MultiFuse] Fusion574
  Refine = true
  Shapes = -> [Cylinder874,Cylinder873]
FEATURE [Part::Box] Box587  label="Cube778"
  AttacherType = Attacher::AttachEngine3D
  Height = 3
  Length = 18
  Placement = pos=(280,55.75,-21) rot=(0,0,1;0rad)
  Width = 9
FEATURE [Part::Cylinder] Cylinder878  label="Cylinder1022"
  Angle = 360
  AttacherType = Attacher::AttachEngine3D
  Height = 12
  Placement = pos=(289,61.5,-27) rot=(0,0,1;0rad)
  Radius = 1.6
FEATURE [Part::Cylinder] Cylinder879  label="Cylinder1023"
  Angle = 360
  AttacherType = Attacher::AttachEngine3D
  Height = 9
  Placement = pos=(294,62.5,-34) rot=(1,0,0;1.5708rad)
  Radius = 1.2
FEATURE [Part::Cylinder] Cylinder880  label="Cylinder1024"
  Angle = 360
  AttacherType = Attacher::AttachEngine3D
  Height = 9
  Placement = pos=(284,62.5,-34) rot=(1,0,0;1.5708rad)
  Radius = 1.2
FEATURE [Part::Cylinder] Cylinder881  label="Cylinder1025"
  Angle = 360
  AttacherType = Attacher::AttachEngine3D
  Height = 9
  Placement = pos=(294,62.5,-25) rot=(1,0,0;1.5708rad)
  Radius = 1.2
FEATURE [Part::Cylinder] Cylinder882  label="Cylinder1026"
  Angle = 360
  AttacherType = Attacher::AttachEngine3D
  Height = 9
  Placement = pos=(284,62.5,-25) rot=(1,0,0;1.5708rad)
  Radius = 1.2
FEATURE [Part::Cylinder] Cylinder883  label="Cylinder1027"
  Angle = 360
  AttacherType = Attacher::AttachEngine3D
  Height = 10
  Placement = pos=(294,62.5,-34) rot=(1,0,0;1.5708rad)
  Radius = 1
FEATURE [Part::Cylinder] Cylinder884  label="Cylinder1048"
  Angle = 360
  AttacherType = Attacher::AttachEngine3D
  Height = 10
  Placement = pos=(284,62.5,-34) rot=(1,0,0;1.5708rad)
  Radius = 1
FEATURE [Part::Cylinder] Cylinder885  label="Cylinder1049"
  Angle = 360
  AttacherType = Attacher::AttachEngine3D
  Height = 10
  Placement = pos=(294,62.5,-25) rot=(1,0,0;1.5708rad)
  Radius = 1
FEATURE [Part::Cylinder] Cylinder886  label="Cylinder1119"
  Angle = 360
  AttacherType = Attacher::AttachEngine3D
  Height = 10
  Placement = pos=(284,62.5,-25) rot=(1,0,0;1.5708rad)
  Radius = 1
FEATURE [Part::Cylinder] Cylinder887  label="Cylinder1120"
  Angle = 360
  AttacherType = Attacher::AttachEngine3D
  Height = 9
  Placement = pos=(289,57.5,-43) rot=(1,0,0;1.5708rad)
  Radius = 2.1
FEATURE [Part::Cylinder] Cylinder888  label="Cylinder1052"
  Angle = 360
  AttacherType = Attacher::AttachEngine3D
  Height = 12
  Placement = pos=(289,60.5,-43) rot=(1,0,0;1.5708rad)
  Radius = 1.25
FEATURE [Part::MultiFuse] Fusion578
  Refine = true
  Shapes = -> [Cylinder888,Cylinder887]
FEATURE [Part::Cylinder] Cylinder889  label="Cylinder1113"
  Angle = 360
  AttacherType = Attacher::AttachEngine3D
  Height = 12
  Placement = pos=(282,59.5,-8) rot=(1,0,0;1.5708rad)
  Radius = 1.6
FEATURE [Part::Cylinder] Cylinder890  label="Cylinder1114"
  Angle = 360
  AttacherType = Attacher::AttachEngine3D
  Height = 12
  Placement = pos=(296,59.5,-8) rot=(1,0,0;1.5708rad)
  Radius = 1.6
FEATURE [Part::Box] Box588  label="Cube779"
  AttacherType = Attacher::AttachEngine3D
  Height = 16
  Length = 18
  Placement = pos=(280,52,-18) rot=(0,0,1;0rad)
  Width = 1.5
FEATURE [Part::Box] Box589  label="Cube780"
  AttacherType = Attacher::AttachEngine3D
  Height = 16
  Length = 1.5
  Placement = pos=(285,48.5,-18) rot=(0,0,1;0rad)
  Width = 3.5
FEATURE [Part::Box] Box590  label="Cube781"
  AttacherType = Attacher::AttachEngine3D
  Height = 16
  Length = 1.52
  Placement = pos=(291.5,48.5,-18) rot=(0,0,1;0rad)
  Width = 3.5
FEATURE [Part::Cylinder] Cylinder891  label="Cylinder1055"
  Angle = 360
  AttacherType = Attacher::AttachEngine3D
  Height = 1.5
  Placement = pos=(282,53.5,-8) rot=(1,0,0;1.5708rad)
  Radius = 3.1
FEATURE [Part::Cylinder] Cylinder892  label="Cylinder1121"
  Angle = 360
  AttacherType = Attacher::AttachEngine3D
  Height = 1.5
  Placement = pos=(296,53.5,-8) rot=(1,0,0;1.5708rad)
  Radius = 3.1
FEATURE [Part::Box] Box592  label="Cube783"
  AttacherType = Attacher::AttachEngine3D
  Height = 18
  Length = 9.5
  Placement = pos=(284,45.0765,-17.2723) rot=(-1,0,0;0.20944rad)
  Width = 3.5
FEATURE [Part::MultiFuse] Fusion579
  Refine = true
  Shapes = -> [Cylinder889,Cylinder890]
FEATURE [Part::MultiFuse] Fusion580
  Refine = true
  Shapes = -> [Box588,Cylinder892,Box589,Box590,Cylinder891]
FEATURE [Part::Box] Box594  label="Cube785"
  AttacherType = Attacher::AttachEngine3D
  Height = 19
  Length = 18
  Placement = pos=(280,53.5,-37) rot=(0,0,1;0rad)
  Width = 2.25
FEATURE [Part::Box] Box595  label="Cube786"
  AttacherType = Attacher::AttachEngine3D
  Height = 11
  Length = 3
  Placement = pos=(280,53.5,-48) rot=(0,0,1;0rad)
  Width = 2.25
FEATURE [Part::Box] Box  label="Cube"
  AttacherType = Attacher::AttachEngine3D
  Height = 17
  Length = 31
  Placement = pos=(280,55,-16.5) rot=(0,0,1;0rad)
  Width = 10
FEATURE [Part::Cylinder] Cylinder893  label="Cylinder1122"
  Angle = 360
  AttacherType = Attacher::AttachEngine3D
  Height = 9
  Placement = pos=(289,60.5,-43) rot=(1,0,0;1.5708rad)
  Radius = 2.1
FEATURE [Part::Cylinder] Cylinder894  label="Cylinder1123"
  Angle = 360
  AttacherType = Attacher::AttachEngine3D
  Height = 14
  Placement = pos=(289,60.5,-43) rot=(1,0,0;1.5708rad)
  Radius = 1.25
FEATURE [Part::MultiFuse] Fusion584
  Placement = pos=(16.5,10,31) rot=(0,0,1;0rad)
  Refine = true
  Shapes = -> [Cylinder894,Cylinder893]
FEATURE [Part::MultiFuse] Fusion588
  Placement = pos=(0,-3.5,0) rot=(0,0,1;0rad)
  Refine = true
  Shapes = -> [Cylinder883,Cylinder886,Cylinder885,Cylinder884]
FEATURE [Part::Cylinder] Cylinder901  label="Cylinder1124"
  Angle = 360
  AttacherType = Attacher::AttachEngine3D
  Height = 12
  Placement = pos=(289,61.5,-27) rot=(0,0,1;0rad)
  Radius = 1.25
FEATURE [Part::Loft] Loft021
  Closed = false
  MaxDegree = 5
  Ruled = false
  Sections = -> [Face047,Face048]
  Solid = true
FEATURE [Part::MultiFuse] Fusion590
  Refine = true
  Shapes = -> [Fusion547,Fusion549,Loft021]
FEATURE [Part::Cut] Cut014074  label="central-axle-left-upper-bar"
  Base = -> Fusion590
  Placement = pos=(30.3862,0,84.3621) rot=(0,1,0;0.340339rad)
  Refine = true
  Tool = -> Fusion551
FEATURE [Part::Fillet] Fillet376
  Base = -> Box
  Edges = 2 edges r=3: [Edge9,Edge10]
FEATURE [Part::Cut] Cut014075
  Base = -> Fillet376
  Refine = true
  Tool = -> Fusion584
FEATURE [Part::Box] Box596  label="Cube787"
  AttacherType = Attacher::AttachEngine3D
  Height = 6
  Length = 6
  Placement = pos=(294,63.5,-2) rot=(0,0,1;0rad)
  Width = 5
FEATURE [Part::Cylinder] Cylinder905  label="Cylinder1125"
  Angle = 360
  AttacherType = Attacher::AttachEngine3D
  Height = 5
  Placement = pos=(291.5,68.5,1) rot=(1,0,0;1.5708rad)
  Radius = 5
FEATURE [Part::Fillet] Fillet377
  Base = -> Box596
  Edges = 4 edges r=2.49: [Edge9,Edge10,Edge11,Edge12]
FEATURE [Part::Fillet] Fillet378
  Base = -> Cylinder905
  Edges = 2 edges r=0.75: [Edge1,Edge3]
FEATURE [Part::MultiFuse] Fusion591
  Placement = pos=(0,1.75,0) rot=(0,0,1;0rad)
  Refine = true
  Shapes = -> [Fillet378,Fillet377]
FEATURE [Part::Box] Box597  label="Cube788"
  AttacherType = Attacher::AttachEngine3D
  Height = 6
  Length = 6
  Placement = pos=(294,63.5,-2) rot=(0,0,1;0rad)
  Width = 5
FEATURE [Part::Cylinder] Cylinder906
  Angle = 360
  AttacherType = Attacher::AttachEngine3D
  Height = 5
  Placement = pos=(291.5,68.5,1) rot=(1,0,0;1.5708rad)
  Radius = 5
FEATURE [Part::Fillet] Fillet379
  Base = -> Box597
  Edges = 4 edges r=2.49: [Edge9,Edge10,Edge11,Edge12]
FEATURE [Part::Fillet] Fillet380
  Base = -> Cylinder906
  Edges = 2 edges r=0.75: [Edge1,Edge3]
FEATURE [Part::MultiFuse] Fusion592
  Placement = pos=(628,7.5,2) rot=(0,1,0;3.14159rad)
  Refine = true
  Shapes = -> [Fillet380,Fillet379]
FEATURE [Part::Cylinder] Cylinder907
  Angle = 360
  AttacherType = Attacher::AttachEngine3D
  Height = 5
  Placement = pos=(291.5,70.25,1) rot=(1,0,0;1.5708rad)
  Radius = 3.1
FEATURE [Part::Cylinder] Cylinder908
  Angle = 360
  AttacherType = Attacher::AttachEngine3D
  Height = 5
  Placement = pos=(336.5,76,1) rot=(1,0,0;1.5708rad)
  Radius = 3.1
FEATURE [Part::MultiFuse] Fusion593
  Refine = true
  Shapes = -> [Cylinder907,Cylinder908]
FEATURE [Part::Feature] Face049
  Placement = pos=(0,1.5,0) rot=(0,0,1;0rad)
  shape: bbox 2e-07 x 5.5 x 6.6 mm, 1 faces, 0 solids (baked)
FEATURE [Part::Feature] Face050
  Placement = pos=(0,1.75,0) rot=(0,0,1;0rad)
  shape: bbox 2e-07 x 5.5 x 6.6 mm, 1 faces, 0 solids (baked)
FEATURE [Part::Loft] Loft022
  Closed = false
  MaxDegree = 5
  Ruled = false
  Sections = -> [Face049,Face050]
  Solid = true
FEATURE [Part::MultiFuse] Fusion594
  Refine = true
  Shapes = -> [Fusion591,Fusion592,Loft022]
FEATURE [Part::Cut] Cut014078  label="central-axle-left-upper-bar001"
  Base = -> Fusion594
  Placement = pos=(30.3862,0,84.3621) rot=(0,1,0;0.340339rad)
  Refine = true
  Tool = -> Fusion593
FEATURE [Part::Mirroring] Part__Mirroring  label="central-axle-right-upper-bar"
  Base = (0,0,0)
  Normal = (0,1,0)
  Placement = pos=(0,170,0) rot=(0,0,1;0rad)
  Source = -> Cut014078
FEATURE [Part::Cylinder] Cylinder909  label="Cylinder1126"
  Angle = 360
  AttacherType = Attacher::AttachEngine3D
  Height = 12
  Placement = pos=(282,59.5,-8) rot=(1,0,0;1.5708rad)
  Radius = 1.25
FEATURE [Part::Cylinder] Cylinder910  label="Cylinder1127"
  Angle = 360
  AttacherType = Attacher::AttachEngine3D
  Height = 12
  Placement = pos=(296,59.5,-8) rot=(1,0,0;1.5708rad)
  Radius = 1.25
FEATURE [Part::MultiFuse] Fusion595
  Placement = pos=(0,7,0) rot=(0,0,1;0rad)
  Refine = true
  Shapes = -> [Cylinder909,Cylinder910]
FEATURE [Part::Box] Box598  label="Cube789"
  AttacherType = Attacher::AttachEngine3D
  Height = 10
  Length = 11
  Placement = pos=(300.5,49.5,-17) rot=(0,0,1;0rad)
  Width = 10
FEATURE [Part::Cut] Cut014079
  Base = -> Cut014075
  Refine = true
  Tool = -> Box598
FEATURE [Part::Cut] Cut014082
  Base = -> Fusion580
  Refine = true
  Tool = -> Box592
FEATURE [Part::Cut] Cut014083
  Base = -> Cut014082
  Refine = true
  Tool = -> Fusion579
FEATURE [Part::MultiFuse] Fusion596
  Refine = true
  Shapes = -> [Box587,Box594,Box595,Box586,Box584,Chamfer107,Cut014083]
FEATURE [Part::MultiFuse] Fusion598
  Refine = true
  Shapes = -> [Cylinder879,Cylinder880,Cylinder881,Cylinder882]
FEATURE [Part::Cut] Cut014084
  Base = -> Cut014079
  Refine = true
  Tool = -> Cylinder901
FEATURE [Part::Cut] Cut014085  label="central-axle-left-upper-bar-support-internal"
  Base = -> Cut014084
  Refine = true
  Tool = -> Fusion595
FEATURE [Part::Cut] Cut014086
  Base = -> Fusion596
  Refine = true
  Tool = -> Fusion588
FEATURE [Part::Cut] Cut014087
  Base = -> Cut014086
  Refine = true
  Tool = -> Cylinder878
FEATURE [Part::Cut] Cut014088
  Base = -> Chamfer108
  Refine = true
  Tool = -> Fusion598
FEATURE [Part::Cut] Cut014089  label="central-axle-left-lower-bar-support-external"
  Base = -> Cut014087
  Refine = true
  Tool = -> Fusion574
FEATURE [Part::Cut] Cut014090  label="central-axle-left-lower-bar-support-internal"
  Base = -> Cut014088
  Refine = true
  Tool = -> Fusion578
FEATURE [Part::Box] Box599  label="Cube790"
  AttacherType = Attacher::AttachEngine3D
  Height = 10
  Length = 15
  Placement = pos=(340.5,44.5,-63) rot=(0,0,1;0rad)
  Width = 7
FEATURE [Part::Cylinder] Cylinder911  label="Cylinder1128"
  Angle = 360
  AttacherType = Attacher::AttachEngine3D
  Height = 10
  Placement = pos=(332.5,48,-59) rot=(0,1,0;1.5708rad)
  Radius = 1.5
FEATURE [Part::Box] Box600  label="Cube791"
  AttacherType = Attacher::AttachEngine3D
  Height = 8
  Length = 9
  Placement = pos=(343.5,38.5,-63) rot=(0,0,1;0rad)
  Width = 25
FEATURE [Part::Box] Box601  label="Cube792"
  AttacherType = Attacher::AttachEngine3D
  Height = 12
  Length = 14
  Placement = pos=(338.5,44.5,-65) rot=(0,0,1;0rad)
  Width = 16
FEATURE [Part::Cylinder] Cylinder912  label="Cylinder1129"
  Angle = 360
  AttacherType = Attacher::AttachEngine3D
  Height = 3
  Placement = pos=(348.5,40,-38.5) rot=(0,0,1;0rad)
  Radius = 8
FEATURE [Part::MultiFuse] Fusion599
  Refine = true
  Shapes = -> [Box600,Cylinder911,Box599]
FEATURE [Part::Box] Box602  label="Cube793"
  AttacherType = Attacher::AttachEngine3D
  Height = 17.5
  Length = 14
  Placement = pos=(338.5,44.5,-53) rot=(0,0,1;0rad)
  Width = 16
FEATURE [Part::Box] Box603  label="Cube794"
  AttacherType = Attacher::AttachEngine3D
  Height = 10
  Length = 26
  Placement = pos=(326.5,51.5,-63) rot=(0,0,1;0rad)
  Width = 5
FEATURE [Part::Fillet] Fillet381
  Base = -> Box603
  Edges = 2 edges r=4.99: [Edge2,Edge4]
  Placement = pos=(0,4,0) rot=(0,0,1;0rad)
FEATURE [Part::Cylinder] Cylinder913  label="Cylinder1130"
  Angle = 360
  AttacherType = Attacher::AttachEngine3D
  Height = 10
  Placement = pos=(348.5,40,-44) rot=(0,0,1;0rad)
  Radius = 1.25
FEATURE [Part::Cylinder] Cylinder914  label="Cylinder1131"
  Angle = 360
  AttacherType = Attacher::AttachEngine3D
  Height = 10
  Placement = pos=(331.5,60.5,-58) rot=(1,0,0;1.5708rad)
  Radius = 1.25
FEATURE [Part::Cylinder] Cylinder915  label="Cylinder1132"
  Angle = 360
  AttacherType = Attacher::AttachEngine3D
  Height = 10
  Placement = pos=(343.5,56,-40) rot=(1,0,0;1.5708rad)
  Radius = 1.25
FEATURE [Part::Cylinder] Cylinder916  label="Cylinder1133"
  Angle = 360
  AttacherType = Attacher::AttachEngine3D
  Height = 10
  Placement = pos=(342.5,51.5,-50) rot=(0,1,0;1.5708rad)
  Radius = 1.25
FEATURE [Part::Cylinder] Cylinder917  label="Cylinder1134"
  Angle = 360
  AttacherType = Attacher::AttachEngine3D
  Height = 10
  Placement = pos=(342.5,51.5,-42) rot=(0,1,0;1.5708rad)
  Radius = 1.25
FEATURE [Part::Cylinder] Cylinder918  label="Cylinder1135"
  Angle = 360
  AttacherType = Attacher::AttachEngine3D
  Height = 2
  Placement = pos=(348.5,48,-65) rot=(0,0,1;0rad)
  Radius = 2.1
FEATURE [Part::Box] Box604  label="Cube795"
  AttacherType = Attacher::AttachEngine3D
  Height = 8
  Length = 8
  Placement = pos=(344.5,39.5,-45) rot=(0,0,1;0rad)
  Width = 8
FEATURE [Part::Chamfer] Chamfer109
  Base = -> Box604
  Edges = 1 edges r=7.99: [Edge9]
  Placement = pos=(0,-2,1) rot=(0,0,1;0rad)
FEATURE [Part::Cylinder] Cylinder919  label="Cylinder1136"
  Angle = 360
  AttacherType = Attacher::AttachEngine3D
  Height = 7
  Placement = pos=(348.5,40,-45.5) rot=(0,0,1;0rad)
  Radius = 3.1
FEATURE [Part::Cylinder] Cylinder920  label="Cylinder1137"
  Angle = 360
  AttacherType = Attacher::AttachEngine3D
  Height = 10
  Placement = pos=(348,60.5,-47) rot=(1,0,0;1.5708rad)
  Radius = 1.25
FEATURE [Part::Cylinder] Cylinder921  label="Cylinder1138"
  Angle = 360
  AttacherType = Attacher::AttachEngine3D
  Height = 10
  Placement = pos=(348,60.5,-39) rot=(1,0,0;1.5708rad)
  Radius = 1.25
FEATURE [Part::Cylinder] Cylinder922  label="Cylinder1139"
  Angle = 360
  AttacherType = Attacher::AttachEngine3D
  Height = 10
  Placement = pos=(331.5,59.5,-58) rot=(1,0,0;1.5708rad)
  Radius = 2.1
FEATURE [Part::MultiFuse] Fusion600
  Refine = true
  Shapes = -> [Box602,Cylinder912,Box601,Fillet381,Chamfer109]
FEATURE [Part::Cut] Cut014091
  Base = -> Fusion600
  Refine = true
  Tool = -> Fusion599
FEATURE [Part::MultiFuse] Fusion601
  Refine = true
  Shapes = -> [Cylinder918,Cylinder913,Cylinder914,Cylinder915,Cylinder916,Cylinder917,Cylinder920,Cylinder921,Cylinder922,Cylinder919]
FEATURE [Part::Cut] Cut014092  label="central-axle-left-baloon-support001"
  Base = -> Cut014091
  Refine = true
  Tool = -> Fusion601
FEATURE [Part::Box] Box605  label="Cube796"
  AttacherType = Attacher::AttachEngine3D
  Height = 19.5
  Length = 9
  Placement = pos=(343.5,60.5,-55) rot=(0,0,1;0rad)
  Width = 17.5
FEATURE [Part::Box] Box606  label="Cube797"
  AttacherType = Attacher::AttachEngine3D
  Height = 13.5
  Length = 9
  Placement = pos=(343.5,68,-35.5) rot=(0,0,1;0rad)
  Width = 2.75
FEATURE [Part::Box] Box607  label="Cube798"
  AttacherType = Attacher::AttachEngine3D
  Height = 3
  Length = 9
  Placement = pos=(343.5,68,-35.5) rot=(0,0,1;0rad)
  Width = 10
FEATURE [Part::Box] Box608  label="Cube799"
  AttacherType = Attacher::AttachEngine3D
  Height = 13.5
  Length = 9
  Placement = pos=(343.5,76.25,-35.5) rot=(0,0,1;0rad)
  Width = 1.75
FEATURE [Part::Chamfer] Chamfer110
  Base = -> Box605
  Edges = 1 edges r=15: [Edge11]
FEATURE [Part::MultiFuse] Fusion602
  Refine = true
  Shapes = -> [Box606,Box607,Box608]
FEATURE [Part::Cylinder] Cylinder923  label="Cylinder1095"
  Angle = 360
  AttacherType = Attacher::AttachEngine3D
  Height = 18
  Placement = pos=(348,78.5,-47) rot=(1,0,0;1.5708rad)
  Radius = 1.25
FEATURE [Part::Cylinder] Cylinder924  label="Cylinder1140"
  Angle = 360
  AttacherType = Attacher::AttachEngine3D
  Height = 18
  Placement = pos=(348,78.5,-39) rot=(1,0,0;1.5708rad)
  Radius = 1.25
FEATURE [Part::Cylinder] Cylinder925  label="Cylinder1141"
  Angle = 360
  AttacherType = Attacher::AttachEngine3D
  Height = 18
  Placement = pos=(348,84.5,-47) rot=(1,0,0;1.5708rad)
  Radius = 3.1
FEATURE [Part::Cylinder] Cylinder926  label="Cylinder1142"
  Angle = 360
  AttacherType = Attacher::AttachEngine3D
  Height = 18
  Placement = pos=(348,84.5,-39) rot=(1,0,0;1.5708rad)
  Radius = 3.1
FEATURE [Part::MultiFuse] Fusion603
  Refine = true
  Shapes = -> [Chamfer110,Fusion602]
FEATURE [Part::Fillet] Fillet382
  Base = -> Fusion603
  Edges = 1 edges r=6: [Edge2]
FEATURE [Part::Fillet] Fillet383
  Base = -> Fillet382
  Edges = 4 edges r=3: [Edge9,Edge14,Edge21,Edge27]
FEATURE [Part::Chamfer] Chamfer111
  Base = -> Fillet383
  Edges = 1 edges r=3: [Edge40]
FEATURE [Part::Cylinder] Cylinder927  label="Cylinder1143"
  Angle = 360
  AttacherType = Attacher::AttachEngine3D
  Height = 18
  Placement = pos=(348,78.5,-27) rot=(1,0,0;1.5708rad)
  Radius = 1.25
FEATURE [Part::MultiFuse] Fusion604
  Refine = true
  Shapes = -> [Cylinder927,Cylinder924,Cylinder925,Cylinder926,Cylinder923]
FEATURE [Part::Cut] Cut014093  label="central-axle-left-upper-bar-support001"
  Base = -> Chamfer111
  Refine = true
  Tool = -> Fusion604
FEATURE [Part::Box] Box609  label="Cube800"
  AttacherType = Attacher::AttachEngine3D
  Height = 30
  Length = 18
  Placement = pos=(280,48.5,-48) rot=(0,0,1;0rad)
  Width = 1.75
FEATURE [Part::Chamfer] Chamfer112
  Base = -> Box609
  Edges = 1 edges r=5: [Edge8]
FEATURE [Part::Cylinder] Cylinder928  label="Cylinder1144"
  Angle = 360
  AttacherType = Attacher::AttachEngine3D
  Height = 9
  Placement = pos=(289,57.5,-43) rot=(1,0,0;1.5708rad)
  Radius = 2.1
FEATURE [Part::Box] Box610  label="Cube801"
  AttacherType = Attacher::AttachEngine3D
  Height = 19
  Length = 18
  Placement = pos=(280,49.5,-37) rot=(0,0,1;0rad)
  Width = 4
FEATURE [Part::Box] Box611  label="Cube802"
  AttacherType = Attacher::AttachEngine3D
  Height = 26.75
  Length = 18
  Placement = pos=(280,48.5,-48) rot=(0,0,1;0rad)
  Width = 2.75
FEATURE [Part::Chamfer] Chamfer113
  Base = -> Box611
  Edges = 1 edges r=5: [Edge8]
  Placement = pos=(0,7.25,0) rot=(0,0,1;0rad)
FEATURE [Part::Box] Box612  label="Cube803"
  AttacherType = Attacher::AttachEngine3D
  Height = 11
  Length = 3
  Placement = pos=(280,49.5,-48) rot=(0,0,1;0rad)
  Width = 4
FEATURE [Part::Cylinder] Cylinder929  label="Cylinder1145"
  Angle = 360
  AttacherType = Attacher::AttachEngine3D
  Height = 12
  Placement = pos=(289,60.5,-43) rot=(1,0,0;1.5708rad)
  Radius = 1.25
FEATURE [Part::MultiFuse] Fusion605
  Refine = true
  Shapes = -> [Cylinder929,Cylinder928]
FEATURE [Part::Box] Box613  label="Cube804"
  AttacherType = Attacher::AttachEngine3D
  Height = 3
  Length = 18
  Placement = pos=(280,55.75,-21) rot=(0,0,1;0rad)
  Width = 9
FEATURE [Part::Cylinder] Cylinder930  label="Cylinder1146"
  Angle = 360
  AttacherType = Attacher::AttachEngine3D
  Height = 12
  Placement = pos=(289,61.5,-27) rot=(0,0,1;0rad)
  Radius = 1.6
FEATURE [Part::Cylinder] Cylinder931  label="Cylinder1147"
  Angle = 360
  AttacherType = Attacher::AttachEngine3D
  Height = 9
  Placement = pos=(294,62.5,-34) rot=(1,0,0;1.5708rad)
  Radius = 1.2
FEATURE [Part::Cylinder] Cylinder932  label="Cylinder1148"
  Angle = 360
  AttacherType = Attacher::AttachEngine3D
  Height = 9
  Placement = pos=(284,62.5,-34) rot=(1,0,0;1.5708rad)
  Radius = 1.2
FEATURE [Part::Cylinder] Cylinder933  label="Cylinder1149"
  Angle = 360
  AttacherType = Attacher::AttachEngine3D
  Height = 9
  Placement = pos=(294,62.5,-25) rot=(1,0,0;1.5708rad)
  Radius = 1.2
FEATURE [Part::Cylinder] Cylinder934  label="Cylinder1150"
  Angle = 360
  AttacherType = Attacher::AttachEngine3D
  Height = 9
  Placement = pos=(284,62.5,-25) rot=(1,0,0;1.5708rad)
  Radius = 1.2
FEATURE [Part::Cylinder] Cylinder935  label="Cylinder1151"
  Angle = 360
  AttacherType = Attacher::AttachEngine3D
  Height = 10
  Placement = pos=(294,62.5,-34) rot=(1,0,0;1.5708rad)
  Radius = 1
FEATURE [Part::Cylinder] Cylinder936  label="Cylinder1152"
  Angle = 360
  AttacherType = Attacher::AttachEngine3D
  Height = 10
  Placement = pos=(284,62.5,-34) rot=(1,0,0;1.5708rad)
  Radius = 1
FEATURE [Part::Cylinder] Cylinder937  label="Cylinder1153"
  Angle = 360
  AttacherType = Attacher::AttachEngine3D
  Height = 10
  Placement = pos=(294,62.5,-25) rot=(1,0,0;1.5708rad)
  Radius = 1
FEATURE [Part::Cylinder] Cylinder938  label="Cylinder1154"
  Angle = 360
  AttacherType = Attacher::AttachEngine3D
  Height = 10
  Placement = pos=(284,62.5,-25) rot=(1,0,0;1.5708rad)
  Radius = 1
FEATURE [Part::Cylinder] Cylinder939  label="Cylinder1155"
  Angle = 360
  AttacherType = Attacher::AttachEngine3D
  Height = 9
  Placement = pos=(289,57.5,-43) rot=(1,0,0;1.5708rad)
  Radius = 2.1
FEATURE [Part::Cylinder] Cylinder940  label="Cylinder1156"
  Angle = 360
  AttacherType = Attacher::AttachEngine3D
  Height = 12
  Placement = pos=(289,60.5,-43) rot=(1,0,0;1.5708rad)
  Radius = 1.25
FEATURE [Part::MultiFuse] Fusion606
  Refine = true
  Shapes = -> [Cylinder940,Cylinder939]
FEATURE [Part::Cylinder] Cylinder941  label="Cylinder1157"
  Angle = 360
  AttacherType = Attacher::AttachEngine3D
  Height = 12
  Placement = pos=(282,59.5,-8) rot=(1,0,0;1.5708rad)
  Radius = 1.6
FEATURE [Part::Cylinder] Cylinder942  label="Cylinder1158"
  Angle = 360
  AttacherType = Attacher::AttachEngine3D
  Height = 12
  Placement = pos=(296,59.5,-8) rot=(1,0,0;1.5708rad)
  Radius = 1.6
FEATURE [Part::Box] Box614  label="Cube805"
  AttacherType = Attacher::AttachEngine3D
  Height = 16
  Length = 18
  Placement = pos=(280,52,-18) rot=(0,0,1;0rad)
  Width = 1.5
FEATURE [Part::Box] Box615  label="Cube806"
  AttacherType = Attacher::AttachEngine3D
  Height = 16
  Length = 1.5
  Placement = pos=(285,48.5,-18) rot=(0,0,1;0rad)
  Width = 3.5
FEATURE [Part::Box] Box616  label="Cube807"
  AttacherType = Attacher::AttachEngine3D
  Height = 16
  Length = 1.52
  Placement = pos=(291.5,48.5,-18) rot=(0,0,1;0rad)
  Width = 3.5
FEATURE [Part::Cylinder] Cylinder943  label="Cylinder1159"
  Angle = 360
  AttacherType = Attacher::AttachEngine3D
  Height = 1.5
  Placement = pos=(282,53.5,-8) rot=(1,0,0;1.5708rad)
  Radius = 3.1
FEATURE [Part::Cylinder] Cylinder944  label="Cylinder1160"
  Angle = 360
  AttacherType = Attacher::AttachEngine3D
  Height = 1.5
  Placement = pos=(296,53.5,-8) rot=(1,0,0;1.5708rad)
  Radius = 3.1
FEATURE [Part::Box] Box617  label="Cube808"
  AttacherType = Attacher::AttachEngine3D
  Height = 18
  Length = 9.5
  Placement = pos=(284,45.0765,-17.2723) rot=(-1,0,0;0.20944rad)
  Width = 3.5
FEATURE [Part::MultiFuse] Fusion607
  Refine = true
  Shapes = -> [Cylinder941,Cylinder942]
FEATURE [Part::MultiFuse] Fusion608
  Refine = true
  Shapes = -> [Box614,Cylinder944,Box615,Box616,Cylinder943]
FEATURE [Part::Box] Box618  label="Cube809"
  AttacherType = Attacher::AttachEngine3D
  Height = 19
  Length = 18
  Placement = pos=(280,53.5,-37) rot=(0,0,1;0rad)
  Width = 2.25
FEATURE [Part::Box] Box619  label="Cube810"
  AttacherType = Attacher::AttachEngine3D
  Height = 11
  Length = 3
  Placement = pos=(280,53.5,-48) rot=(0,0,1;0rad)
  Width = 2.25
FEATURE [Part::Box] Box620  label="Cube811"
  AttacherType = Attacher::AttachEngine3D
  Height = 17
  Length = 31
  Placement = pos=(280,55,-16.5) rot=(0,0,1;0rad)
  Width = 10
FEATURE [Part::Cylinder] Cylinder945  label="Cylinder1161"
  Angle = 360
  AttacherType = Attacher::AttachEngine3D
  Height = 9
  Placement = pos=(289,60.5,-43) rot=(1,0,0;1.5708rad)
  Radius = 2.1
FEATURE [Part::Cylinder] Cylinder946  label="Cylinder1162"
  Angle = 360
  AttacherType = Attacher::AttachEngine3D
  Height = 14
  Placement = pos=(289,60.5,-43) rot=(1,0,0;1.5708rad)
  Radius = 1.25
FEATURE [Part::MultiFuse] Fusion609
  Placement = pos=(16.5,10,31) rot=(0,0,1;0rad)
  Refine = true
  Shapes = -> [Cylinder946,Cylinder945]
FEATURE [Part::MultiFuse] Fusion610
  Placement = pos=(0,-3.5,0) rot=(0,0,1;0rad)
  Refine = true
  Shapes = -> [Cylinder935,Cylinder938,Cylinder937,Cylinder936]
FEATURE [Part::Cylinder] Cylinder947  label="Cylinder1163"
  Angle = 360
  AttacherType = Attacher::AttachEngine3D
  Height = 12
  Placement = pos=(289,61.5,-27) rot=(0,0,1;0rad)
  Radius = 1.25
FEATURE [Part::Fillet] Fillet384
  Base = -> Box620
  Edges = 2 edges r=3: [Edge9,Edge10]
FEATURE [Part::Cut] Cut014094
  Base = -> Fillet384
  Refine = true
  Tool = -> Fusion609
FEATURE [Part::Cylinder] Cylinder948  label="Cylinder1164"
  Angle = 360
  AttacherType = Attacher::AttachEngine3D
  Height = 12
  Placement = pos=(282,59.5,-8) rot=(1,0,0;1.5708rad)
  Radius = 1.25
FEATURE [Part::Cylinder] Cylinder949  label="Cylinder1165"
  Angle = 360
  AttacherType = Attacher::AttachEngine3D
  Height = 12
  Placement = pos=(296,59.5,-8) rot=(1,0,0;1.5708rad)
  Radius = 1.25
FEATURE [Part::MultiFuse] Fusion611
  Placement = pos=(0,7,0) rot=(0,0,1;0rad)
  Refine = true
  Shapes = -> [Cylinder948,Cylinder949]
FEATURE [Part::Box] Box621  label="Cube812"
  AttacherType = Attacher::AttachEngine3D
  Height = 10
  Length = 11
  Placement = pos=(300.5,49.5,-17) rot=(0,0,1;0rad)
  Width = 10
FEATURE [Part::Cut] Cut014095
  Base = -> Cut014094
  Refine = true
  Tool = -> Box621
FEATURE [Part::Cut] Cut014096
  Base = -> Fusion608
  Refine = true
  Tool = -> Box617
FEATURE [Part::Cut] Cut014097
  Base = -> Cut014096
  Refine = true
  Tool = -> Fusion607
FEATURE [Part::MultiFuse] Fusion612
  Refine = true
  Shapes = -> [Box613,Box618,Box619,Box612,Box610,Chamfer112,Cut014097]
FEATURE [Part::MultiFuse] Fusion613
  Refine = true
  Shapes = -> [Cylinder931,Cylinder932,Cylinder933,Cylinder934]
FEATURE [Part::Cut] Cut014098
  Base = -> Cut014095
  Refine = true
  Tool = -> Cylinder947
FEATURE [Part::Cut] Cut014099  label="central-axle-left-upper-bar-support-internal001"
  Base = -> Cut014098
  Refine = true
  Tool = -> Fusion611
FEATURE [Part::Cut] Cut014100
  Base = -> Fusion612
  Refine = true
  Tool = -> Fusion610
FEATURE [Part::Cut] Cut014101
  Base = -> Cut014100
  Refine = true
  Tool = -> Cylinder930
FEATURE [Part::Cut] Cut014102
  Base = -> Chamfer113
  Refine = true
  Tool = -> Fusion613
FEATURE [Part::Cut] Cut014103  label="central-axle-left-lower-bar-support-external001"
  Base = -> Cut014101
  Refine = true
  Tool = -> Fusion605
FEATURE [Part::Cut] Cut014104  label="central-axle-left-lower-bar-support-internal001"
  Base = -> Cut014102
  Refine = true
  Tool = -> Fusion606
FEATURE [Part::Mirroring] Part__Mirroring037  label="central-axle-right-baloon-support"
  Base = (0,0,0)
  Normal = (0,1,0)
  Placement = pos=(0,170,0) rot=(0,0,1;0rad)
  Source = -> Cut014092
FEATURE [Part::Mirroring] Part__Mirroring038  label="central-axle-right-upper-bar-support"
  Base = (0,0,0)
  Normal = (0,1,0)
  Placement = pos=(0,170,0) rot=(0,0,1;0rad)
  Source = -> Cut014093
FEATURE [Part::Mirroring] Part__Mirroring039  label="central-axle-right-upper-bar-support-internal"
  Base = (0,0,0)
  Normal = (0,1,0)
  Placement = pos=(0,170,0) rot=(0,0,1;0rad)
  Source = -> Cut014099
FEATURE [Part::Mirroring] Part__Mirroring040  label="central-axle-right-lower-bar-support-external"
  Base = (0,0,0)
  Normal = (0,1,0)
  Placement = pos=(0,170,0) rot=(0,0,1;0rad)
  Source = -> Cut014103
FEATURE [Part::Mirroring] Part__Mirroring041  label="central-axle-right-lower-bar-support-internal"
  Base = (0,0,0)
  Normal = (0,1,0)
  Placement = pos=(0,170,0) rot=(0,0,1;0rad)
  Source = -> Cut014104
FEATURE [Part::Cylinder] Cylinder950  label="Cylinder1166"
  Angle = 360
  AttacherType = Attacher::AttachEngine3D
  Height = 15
  Placement = pos=(317,60,-33) rot=(0,0,1;0rad)
  Radius = 1.25
FEATURE [Part::Cylinder] Cylinder951  label="Cylinder1167"
  Angle = 360
  AttacherType = Attacher::AttachEngine3D
  Height = 12
  Placement = pos=(289,61.5,-27) rot=(0,0,1;0rad)
  Radius = 1.25
FEATURE [Part::Cylinder] Cylinder952  label="Cylinder1168"
  Angle = 360
  AttacherType = Attacher::AttachEngine3D
  Height = 12
  Placement = pos=(282,59.5,-8) rot=(1,0,0;1.5708rad)
  Radius = 1.25
FEATURE [Part::Cylinder] Cylinder953  label="Cylinder1169"
  Angle = 360
  AttacherType = Attacher::AttachEngine3D
  Height = 12
  Placement = pos=(296,59.5,-8) rot=(1,0,0;1.5708rad)
  Radius = 1.25
FEATURE [Part::Box] Box622  label="Cube813"
  AttacherType = Attacher::AttachEngine3D
  Height = 26
  Length = 42
  Placement = pos=(279,50.5,-21) rot=(0,0,1;0rad)
  Width = 14.5
FEATURE [Part::Box] Box623  label="Cube814"
  AttacherType = Attacher::AttachEngine3D
  Height = 20
  Length = 42
  Placement = pos=(279,53.5,-18) rot=(0,0,1;0rad)
  Width = 11.5
FEATURE [Part::Cut] Cut014105
  Base = -> Box622
  Refine = true
  Tool = -> Box623
FEATURE [Part::MultiFuse] Fusion614
  Refine = true
  Shapes = -> [Cylinder951,Cylinder952,Cylinder953,Cylinder950]
FEATURE [Part::Cut] Cut014106  label="central-axle-left-suspension-HOLES"
  Base = -> Cut014105
  Refine = true
  Tool = -> Fusion614
FEATURE [Part::Cylinder] Cylinder954  label="Cylinder1170"
  Angle = 360
  AttacherType = Attacher::AttachEngine3D
  Height = 15
  Placement = pos=(317,60,-33) rot=(0,0,1;0rad)
  Radius = 1.25
FEATURE [Part::Cylinder] Cylinder955  label="Cylinder1171"
  Angle = 360
  AttacherType = Attacher::AttachEngine3D
  Height = 12
  Placement = pos=(289,61.5,-27) rot=(0,0,1;0rad)
  Radius = 1.25
FEATURE [Part::Cylinder] Cylinder956  label="Cylinder1172"
  Angle = 360
  AttacherType = Attacher::AttachEngine3D
  Height = 12
  Placement = pos=(282,59.5,-8) rot=(1,0,0;1.5708rad)
  Radius = 1.25
FEATURE [Part::Cylinder] Cylinder957  label="Cylinder1173"
  Angle = 360
  AttacherType = Attacher::AttachEngine3D
  Height = 12
  Placement = pos=(296,59.5,-8) rot=(1,0,0;1.5708rad)
  Radius = 1.25
FEATURE [Part::Box] Box624  label="Cube815"
  AttacherType = Attacher::AttachEngine3D
  Height = 26
  Length = 42
  Placement = pos=(279,50.5,-21) rot=(0,0,1;0rad)
  Width = 14.5
FEATURE [Part::Box] Box625  label="Cube816"
  AttacherType = Attacher::AttachEngine3D
  Height = 20
  Length = 42
  Placement = pos=(279,53.5,-18) rot=(0,0,1;0rad)
  Width = 11.5
FEATURE [Part::Cut] Cut014107
  Base = -> Box624
  Refine = true
  Tool = -> Box625
FEATURE [Part::MultiFuse] Fusion615
  Refine = true
  Shapes = -> [Cylinder955,Cylinder956,Cylinder957,Cylinder954]
FEATURE [Part::Cut] Cut014108
  Base = -> Cut014107
  Refine = true
  Tool = -> Fusion615
FEATURE [Part::Mirroring] Part__Mirroring042  label="central-axle-right-suspension-HOLES"
  Base = (0,0,0)
  Normal = (0,1,0)
  Placement = pos=(0,170,0) rot=(0,0,1;0rad)
  Source = -> Cut014108
FEATURE [Part::Box] Box626  label="Cube817"
  AttacherType = Attacher::AttachEngine3D
  Height = 7
  Length = 10
  Placement = pos=(312,56.5,-25) rot=(0,0,1;0rad)
  Width = 6.2
FEATURE [Part::Fillet] Fillet385
  Base = -> Box626
  Edges = 4 edges r=3.09: [Edge1,Edge3,Edge5,Edge7]
  Placement = pos=(0,-0.5,0) rot=(0,0,1;0rad)
FEATURE [Part::Box] Box627  label="Cube818"
  AttacherType = Attacher::AttachEngine3D
  Height = 7
  Length = 10
  Placement = pos=(312,56.8,-25) rot=(0,0,1;0rad)
  Width = 6.2
FEATURE [Part::Fillet] Fillet386
  Base = -> Box627
  Edges = 4 edges r=3.09: [Edge1,Edge3,Edge5,Edge7]
  Placement = pos=(0,51.1,0) rot=(0,0,1;0rad)
FEATURE [Part::Box] Box630  label="Cube821"
  AttacherType = Attacher::AttachEngine3D
  Height = 7
  Length = 6.8
  Placement = pos=(313.6,57.8,-25) rot=(0,0,1;0rad)
  Width = 3.6
FEATURE [Part::Fillet] Fillet389
  Base = -> Box630
  Edges = 4 edges r=1.79: [Edge1,Edge3,Edge5,Edge7]
  Placement = pos=(0,-0.5,0) rot=(0,0,1;0rad)
FEATURE [Part::Box] Box631  label="Cube822"
  AttacherType = Attacher::AttachEngine3D
  Height = 7
  Length = 6.8
  Placement = pos=(313.6,57.8,-25) rot=(0,0,1;0rad)
  Width = 3.6
FEATURE [Part::Fillet] Fillet390
  Base = -> Box631
  Edges = 4 edges r=1.79: [Edge1,Edge3,Edge5,Edge7]
  Placement = pos=(0,51.4,0) rot=(0,0,1;0rad)
FEATURE [Part::MultiFuse] Fusion621
  Refine = true
  Shapes = -> [Cylinder852,Cylinder853]
FEATURE [Part::Cut] Cut014109
  Base = -> Chamfer103
  Refine = true
  Tool = -> Fusion621
FEATURE [Part::Box] Box632  label="Cube823"
  AttacherType = Attacher::AttachEngine3D
  Height = 30
  Length = 29
  Width = 13
FEATURE [Part::Box] Box633  label="Cube824"
  AttacherType = Attacher::AttachEngine3D
  Height = 4
  Length = 7
  Placement = pos=(-7,3.5,1) rot=(0,0,1;0rad)
  Width = 6
FEATURE [Part::Box] Box634  label="Cube825"
  AttacherType = Attacher::AttachEngine3D
  Height = 3.3
  Length = 40
  Placement = pos=(-5.5,0,19.5) rot=(0,0,1;0rad)
  Width = 13
FEATURE [Part::Cylinder] Cylinder958  label="Cylinder1174"
  Angle = 360
  AttacherType = Attacher::AttachEngine3D
  Height = 6
  Placement = pos=(6,6.5,30) rot=(0,0,1;0rad)
  Radius = 4
FEATURE [Part::Box] Box635  label="Cube826"
  AttacherType = Attacher::AttachEngine3D
  Height = 1.5
  Length = 28
  Placement = pos=(-8,3.5,34.5) rot=(0,0,1;0rad)
  Width = 6
FEATURE [Part::Fillet] Fillet391
  Base = -> Box635
  Edges = 4 edges r=2: [Edge1,Edge3,Edge5,Edge7]
FEATURE [Part::Cylinder] Cylinder959  label="Cylinder1175"
  Angle = 360
  AttacherType = Attacher::AttachEngine3D
  Height = 10
  Radius = 1
FEATURE [Part::Cylinder] Cylinder960  label="Cylinder1176"
  Angle = 360
  AttacherType = Attacher::AttachEngine3D
  Height = 10
  Placement = pos=(35.3,0,0) rot=(0,0,1;0rad)
  Radius = 1
FEATURE [Part::MultiFuse] Fusion624
  Refine = true
  Shapes = -> [Box632,Fillet391,Box633,Box634,Cylinder958]
FEATURE [Part::MultiFuse] Fusion623
  Placement = pos=(-3.15,6.5,13) rot=(0,0,1;0rad)
  Refine = true
  Shapes = -> [Cylinder959,Cylinder960]
FEATURE [Part::Cylinder] Cylinder961  label="Cylinder1177"
  Angle = 360
  AttacherType = Attacher::AttachEngine3D
  Height = 10
  Placement = pos=(0,6.5,29) rot=(0,0,1;0rad)
  Radius = 1
FEATURE [Part::Cylinder] Cylinder962  label="Cylinder1362"
  Angle = 360
  AttacherType = Attacher::AttachEngine3D
  Height = 10
  Placement = pos=(24,6.5,29) rot=(0,0,1;0rad)
  Radius = 1
FEATURE [Part::Cylinder] Cylinder963  label="Cylinder1179"
  Angle = 360
  AttacherType = Attacher::AttachEngine3D
  Height = 10
  Placement = pos=(0,6.5,29) rot=(0,0,1;0rad)
  Radius = 1
FEATURE [Part::Cylinder] Cylinder964  label="Cylinder1180"
  Angle = 360
  AttacherType = Attacher::AttachEngine3D
  Height = 10
  Placement = pos=(19,6.5,29) rot=(0,0,1;0rad)
  Radius = 1
FEATURE [Part::Cylinder] Cylinder965  label="Cylinder1181"
  Angle = 360
  AttacherType = Attacher::AttachEngine3D
  Height = 10
  Placement = pos=(0,6.5,29) rot=(0,0,1;0rad)
  Radius = 1
FEATURE [Part::Cylinder] Cylinder966  label="Cylinder1182"
  Angle = 360
  AttacherType = Attacher::AttachEngine3D
  Height = 10
  Placement = pos=(14,6.5,29) rot=(0,0,1;0rad)
  Radius = 1
FEATURE [Part::MultiFuse] Fusion625
  Placement = pos=(-6,0,2) rot=(0,0,1;0rad)
  Refine = true
  Shapes = -> [Cylinder961,Cylinder962]
FEATURE [Part::MultiFuse] Fusion626
  Placement = pos=(-3.5,0,2) rot=(0,0,1;0rad)
  Refine = true
  Shapes = -> [Cylinder963,Cylinder964]
FEATURE [Part::MultiFuse] Fusion627
  Placement = pos=(-1,0,2) rot=(0,0,1;0rad)
  Refine = true
  Shapes = -> [Cylinder965,Cylinder966]
FEATURE [Part::MultiFuse] Fusion628
  Refine = true
  Shapes = -> [Fusion623,Fusion626,Fusion625,Fusion627]
FEATURE [Part::Cut] Cut014112  label="hitec-hs85bb"
  Base = -> Fusion624
  Refine = true
  Tool = -> Fusion628
FEATURE [Part::Box] Box636  label="Cube827"
  AttacherType = Attacher::AttachEngine3D
  Height = 30
  Length = 29
  Width = 13
FEATURE [Part::Box] Box637  label="Cube828"
  AttacherType = Attacher::AttachEngine3D
  Height = 4
  Length = 7
  Placement = pos=(-7,3.5,1) rot=(0,0,1;0rad)
  Width = 6
FEATURE [Part::Box] Box638  label="Cube829"
  AttacherType = Attacher::AttachEngine3D
  Height = 3.3
  Length = 40
  Placement = pos=(-5.5,0,19.5) rot=(0,0,1;0rad)
  Width = 13
FEATURE [Part::Cylinder] Cylinder967  label="Cylinder1183"
  Angle = 360
  AttacherType = Attacher::AttachEngine3D
  Height = 6
  Placement = pos=(6,6.5,30) rot=(0,0,1;0rad)
  Radius = 4
FEATURE [Part::Box] Box639  label="Cube830"
  AttacherType = Attacher::AttachEngine3D
  Height = 1.5
  Length = 28
  Placement = pos=(-8,3.5,34.5) rot=(0,0,1;0rad)
  Width = 6
FEATURE [Part::Fillet] Fillet392
  Base = -> Box639
  Edges = 4 edges r=2: [Edge1,Edge3,Edge5,Edge7]
FEATURE [Part::Cylinder] Cylinder968  label="Cylinder1184"
  Angle = 360
  AttacherType = Attacher::AttachEngine3D
  Height = 10
  Radius = 1
FEATURE [Part::Cylinder] Cylinder969  label="Cylinder1185"
  Angle = 360
  AttacherType = Attacher::AttachEngine3D
  Height = 10
  Placement = pos=(35.3,0,0) rot=(0,0,1;0rad)
  Radius = 1
FEATURE [Part::MultiFuse] Fusion629
  Refine = true
  Shapes = -> [Box636,Fillet392,Box637,Box638,Cylinder967]
FEATURE [Part::MultiFuse] Fusion630
  Placement = pos=(-3.15,6.5,13) rot=(0,0,1;0rad)
  Refine = true
  Shapes = -> [Cylinder968,Cylinder969]
FEATURE [Part::Cylinder] Cylinder970  label="Cylinder1186"
  Angle = 360
  AttacherType = Attacher::AttachEngine3D
  Height = 10
  Placement = pos=(0,6.5,29) rot=(0,0,1;0rad)
  Radius = 1
FEATURE [Part::Cylinder] Cylinder971  label="Cylinder1187"
  Angle = 360
  AttacherType = Attacher::AttachEngine3D
  Height = 10
  Placement = pos=(24,6.5,29) rot=(0,0,1;0rad)
  Radius = 1
FEATURE [Part::Cylinder] Cylinder972  label="Cylinder1188"
  Angle = 360
  AttacherType = Attacher::AttachEngine3D
  Height = 10
  Placement = pos=(0,6.5,29) rot=(0,0,1;0rad)
  Radius = 1
FEATURE [Part::Cylinder] Cylinder973  label="Cylinder1189"
  Angle = 360
  AttacherType = Attacher::AttachEngine3D
  Height = 10
  Placement = pos=(19,6.5,29) rot=(0,0,1;0rad)
  Radius = 1
FEATURE [Part::Cylinder] Cylinder974  label="Cylinder1190"
  Angle = 360
  AttacherType = Attacher::AttachEngine3D
  Height = 10
  Placement = pos=(0,6.5,29) rot=(0,0,1;0rad)
  Radius = 1
FEATURE [Part::Cylinder] Cylinder975  label="Cylinder1191"
  Angle = 360
  AttacherType = Attacher::AttachEngine3D
  Height = 10
  Placement = pos=(14,6.5,29) rot=(0,0,1;0rad)
  Radius = 1
FEATURE [Part::MultiFuse] Fusion631
  Placement = pos=(-6,0,2) rot=(0,0,1;0rad)
  Refine = true
  Shapes = -> [Cylinder970,Cylinder971]
FEATURE [Part::MultiFuse] Fusion632
  Placement = pos=(-3.5,0,2) rot=(0,0,1;0rad)
  Refine = true
  Shapes = -> [Cylinder972,Cylinder973]
FEATURE [Part::MultiFuse] Fusion633
  Placement = pos=(-1,0,2) rot=(0,0,1;0rad)
  Refine = true
  Shapes = -> [Cylinder974,Cylinder975]
FEATURE [Part::MultiFuse] Fusion634
  Refine = true
  Shapes = -> [Fusion630,Fusion632,Fusion631,Fusion633]
FEATURE [Part::Cut] Cut014113  label="hitec-hs85bb001"
  Base = -> Fusion629
  Placement = pos=(292,66,-52) rot=(0.57735,0.57735,0.57735;2.0944rad)
  Refine = true
  Tool = -> Fusion634
FEATURE [Part::Cylinder] Cylinder1028  label="Cylinder1192"
  Angle = 360
  AttacherType = Attacher::AttachEngine3D
  Height = 15
  Placement = pos=(370,72.5,-22.85) rot=(0,1,0;1.5708rad)
  Radius = 1
FEATURE [Part::Cylinder] Cylinder1029  label="Cylinder1193"
  Angle = 360
  AttacherType = Attacher::AttachEngine3D
  Height = 15
  Placement = pos=(370,72.5,-58.15) rot=(0,1,0;1.5708rad)
  Radius = 1
FEATURE [Part::MultiFuse] Fusion675
  Placement = pos=(-1,0,3) rot=(0,0,1;0rad)
  Refine = true
  Shapes = -> [Cylinder1029,Cylinder1028]
FEATURE [Part::Box] Box653  label="Cube844"
  AttacherType = Attacher::AttachEngine3D
  Height = 6
  Length = 10
  Placement = pos=(372.5,66,-22.5) rot=(0,0,1;0rad)
  Width = 13
FEATURE [Part::Box] Box654  label="Cube845"
  AttacherType = Attacher::AttachEngine3D
  Height = 6
  Length = 10
  Placement = pos=(372.5,66,-58.5) rot=(0,0,1;0rad)
  Width = 13
FEATURE [Part::MultiFuse] Fusion676
  Refine = true
  Shapes = -> [Box653,Box654]
FEATURE [Part::Cut] Cut014189  label="hitec-hs85bb-mount"
  Base = -> Fusion676
  Placement = pos=(-70.5,45,-119.5) rot=(1,0,0;1.5708rad)
  Refine = true
  Tool = -> Fusion675
FEATURE [Part::Box] Box655  label="Cube846"
  AttacherType = Attacher::AttachEngine3D
  Height = 1.5
  Length = 28
  Placement = pos=(-8,3.5,34.5) rot=(0,0,1;0rad)
  Width = 6
FEATURE [Part::Fillet] Fillet393
  Base = -> Box655
  Edges = 4 edges r=2: [Edge1,Edge3,Edge5,Edge7]
  Placement = pos=(292,65.5,-39.5) rot=(0,1,0;1.5708rad)
FEATURE [Part::MultiFuse] Fusion677  label="hitec-hs85bb002"
  Placement = pos=(1,2,-1.5) rot=(0,0,1;0rad)
  Refine = true
  Shapes = -> [Cut014113,Fillet393]
FEATURE [Part::Box] Box656  label="Cube847"
  AttacherType = Attacher::AttachEngine3D
  Height = 6
  Length = 10
  Placement = pos=(302,61.5,-40.5) rot=(0,0,1;0rad)
  Width = 42
FEATURE [Part::Box] Box657  label="Cube848"
  AttacherType = Attacher::AttachEngine3D
  Height = 16.5
  Length = 10
  Placement = pos=(302,70.5,-34.5) rot=(0,0,1;0rad)
  Width = 8
FEATURE [Part::Box] Box658  label="Cube849"
  AttacherType = Attacher::AttachEngine3D
  Height = 16.5
  Length = 10
  Placement = pos=(302,91.5,-34.5) rot=(0,0,1;0rad)
  Width = 8
FEATURE [Part::MultiFuse] Fusion678
  Refine = true
  Shapes = -> [Cut014189,Box656,Box657,Box658]
FEATURE [Part::Fillet] Fillet394
  Base = -> Fusion678
  Edges = 4 edges r=3.5: [Edge2,Edge4,Edge19,Edge22]
FEATURE [Part::Cylinder] Cylinder1030  label="Cylinder1194"
  Angle = 360
  AttacherType = Attacher::AttachEngine3D
  Height = 10
  Placement = pos=(302,75.5,-24) rot=(0,1,0;1.5708rad)
  Radius = 1.6
FEATURE [Part::Cylinder] Cylinder1031  label="Cylinder1195"
  Angle = 360
  AttacherType = Attacher::AttachEngine3D
  Height = 10
  Placement = pos=(302,94.5,-24) rot=(0,1,0;1.5708rad)
  Radius = 1.6
FEATURE [Part::MultiFuse] Fusion679
  Refine = true
  Shapes = -> [Cylinder1031,Cylinder1030]
FEATURE [Part::Cylinder] Cylinder1032  label="Cylinder1196"
  Angle = 360
  AttacherType = Attacher::AttachEngine3D
  Height = 10
  Placement = pos=(302,75.5,-24) rot=(0,1,0;1.5708rad)
  Radius = 1.25
FEATURE [Part::Cylinder] Cylinder1033  label="Cylinder1197"
  Angle = 360
  AttacherType = Attacher::AttachEngine3D
  Height = 10
  Placement = pos=(302,94.5,-24) rot=(0,1,0;1.5708rad)
  Radius = 1.25
FEATURE [Part::MultiFuse] Fusion680
  Placement = pos=(9,0,0) rot=(0,0,1;0rad)
  Refine = true
  Shapes = -> [Cylinder1033,Cylinder1032]
FEATURE [Part::Cut] Cut014190
  Base = -> Fillet394
  Refine = true
  Tool = -> Fusion679
FEATURE [Part::Fillet] Fillet395  label="central-axle-steering-servo-mount"
  Base = -> Cut014190
  Edges = 2 edges r=3: [Edge59,Edge64]
FEATURE [Part::MultiFuse] Fusion688
  Refine = true
  Shapes = -> [Fillet390,Fillet389]
FEATURE [Part::MultiFuse] Fusion689
  Refine = true
  Shapes = -> [Fillet386,Fillet385]
FEATURE [Part::Box] Box666  label="Cube857"
  AttacherType = Attacher::AttachEngine3D
  Height = 7
  Length = 10
  Placement = pos=(312,56.5,-25) rot=(0,0,1;0rad)
  Width = 6.2
FEATURE [Part::Fillet] Fillet402
  Base = -> Box666
  Edges = 4 edges r=3.09: [Edge1,Edge3,Edge5,Edge7]
  Placement = pos=(0,-0.5,0) rot=(0,0,1;0rad)
FEATURE [Part::Box] Box667  label="Cube858"
  AttacherType = Attacher::AttachEngine3D
  Height = 7
  Length = 10
  Placement = pos=(312,56.8,-25) rot=(0,0,1;0rad)
  Width = 6.2
FEATURE [Part::Fillet] Fillet403
  Base = -> Box667
  Edges = 4 edges r=3.09: [Edge1,Edge3,Edge5,Edge7]
  Placement = pos=(0,51.1,0) rot=(0,0,1;0rad)
FEATURE [Part::MultiFuse] Fusion690
  Placement = pos=(0,0,-7) rot=(0,0,1;0rad)
  Refine = true
  Shapes = -> [Fillet403,Fillet402]
FEATURE [Part::MultiFuse] Fusion691
  Refine = true
  Shapes = -> [Cut014109,Fusion689]
FEATURE [Part::Cut] Cut014196
  Base = -> Fusion691
  Refine = true
  Tool = -> Fusion690
FEATURE [Part::Cut] Cut014197
  Base = -> Cut014196
  Refine = true
  Tool = -> Fusion688
FEATURE [Part::Cut] Cut014198  label="rear-prop-shaft-support"
  Base = -> Cut014197
  Refine = true
  Tool = -> Fusion680
FEATURE [Part::MultiFuse] Fusion692  label="central-axle"
  Refine = true
  Shapes = -> [Cut608,Fusion523,Fusion528]
FEATURE [Part::Cylinder] Cylinder1034  label="central-axle-panhard-bar-STEEL"
  Angle = 360
  AttacherType = Attacher::AttachEngine3D
  Height = 91
  Placement = pos=(365,39.5,-53) rot=(-0.998667,-0.038059,0.034874;1.48486rad)
  Radius = 1.5
FEATURE [Part::Box] Box668  label="Cube859"
  AttacherType = Attacher::AttachEngine3D
  Height = 29.5
  Length = 5
  Placement = pos=(352.5,47.5,-65) rot=(0,0,1;0rad)
  Width = 13
FEATURE [Part::Box] Box669  label="Cube860"
  AttacherType = Attacher::AttachEngine3D
  Height = 10
  Length = 3.5
  Placement = pos=(352.5,44.5,-63) rot=(0,0,1;0rad)
  Width = 7
FEATURE [Part::Box] Box670  label="Cube861"
  AttacherType = Attacher::AttachEngine3D
  Height = 8
  Length = 0.6
  Placement = pos=(352.5,51.5,-63) rot=(0,0,1;0rad)
  Width = 9
FEATURE [Part::Box] Box671  label="Cube862"
  AttacherType = Attacher::AttachEngine3D
  Height = 26
  Length = 5
  Placement = pos=(352.5,39.5,-65) rot=(0,0,1;0rad)
  Width = 13
FEATURE [Part::MultiFuse] Fusion694
  Refine = true
  Shapes = -> [Box671,Box668]
FEATURE [Part::Cylinder] Cylinder1035  label="Cylinder1198"
  Angle = 360
  AttacherType = Attacher::AttachEngine3D
  Height = 10
  Placement = pos=(361,51.5,-50) rot=(0,1,0;1.5708rad)
  Radius = 1.6
FEATURE [Part::Cylinder] Cylinder1036  label="Cylinder1199"
  Angle = 360
  AttacherType = Attacher::AttachEngine3D
  Height = 10
  Placement = pos=(361,51.5,-42) rot=(0,1,0;1.5708rad)
  Radius = 1.6
FEATURE [Part::MultiFuse] Fusion695
  Placement = pos=(-10,0,0) rot=(0,0,1;0rad)
  Refine = true
  Shapes = -> [Cylinder1036,Cylinder1035]
FEATURE [Part::Cylinder] Cylinder1037  label="Cylinder1200"
  Angle = 360
  AttacherType = Attacher::AttachEngine3D
  Height = 10
  Placement = pos=(352.5,41.5,-50) rot=(0,1,0;1.5708rad)
  Radius = 4
FEATURE [Part::Cylinder] Cylinder1038  label="Cylinder1201"
  Angle = 360
  AttacherType = Attacher::AttachEngine3D
  Height = 10
  Placement = pos=(352.5,41.5,-50) rot=(0,1,0;1.5708rad)
  Radius = 1.3
FEATURE [Part::Box] Box672  label="Cube863"
  AttacherType = Attacher::AttachEngine3D
  Height = 16
  Length = 0.6
  Placement = pos=(352.5,35.5,-63) rot=(0,0,1;0rad)
  Width = 9
FEATURE [Part::MultiFuse] Fusion696
  Refine = true
  Shapes = -> [Box672,Box670,Box669]
FEATURE [Part::Cut] Cut014199
  Base = -> Fusion694
  Refine = true
  Tool = -> Fusion695
FEATURE [Part::MultiFuse] Fusion697
  Refine = true
  Shapes = -> [Cut014199,Cylinder1037]
FEATURE [Part::Cut] Cut014204
  Base = -> Fusion697
  Refine = true
  Tool = -> Cylinder1038
FEATURE [Part::Chamfer] Chamfer
  Base = -> Cut014204
  Edges = 2 edges r=6: [Edge21,Edge30]
FEATURE [Part::Cut] Cut014205  label="central-axle-panhard-bar-lower-mount"
  Base = -> Chamfer
  Refine = true
  Tool = -> Fusion696
FEATURE [Part::Box] Box673  label="Cube864"
  AttacherType = Attacher::AttachEngine3D
  Height = 40
  Length = 6
  Placement = pos=(361,111.5,-46) rot=(0,0,1;0rad)
  Width = 20
FEATURE [Part::Box] Box674  label="Cube865"
  AttacherType = Attacher::AttachEngine3D
  Height = 3
  Length = 20
  Placement = pos=(359,105.5,-21) rot=(0,0,1;0rad)
  Width = 11
FEATURE [Part::Box] Box675  label="Cube866"
  AttacherType = Attacher::AttachEngine3D
  Height = 20
  Length = 20
  Placement = pos=(359,116.5,-21) rot=(0,0,1;0rad)
  Width = 3
FEATURE [Part::MultiFuse] Fusion699
  Placement = pos=(2,0,0) rot=(0,0,1;0rad)
  Refine = true
  Shapes = -> [Box674,Box675]
FEATURE [Part::Chamfer] Chamfer114
  Base = -> Box673
  Edges = 1 edges: [Edge12 r1=34 r2=12]
FEATURE [Part::Chamfer] Chamfer115
  Base = -> Chamfer114
  Edges = 1 edges: [Edge11 r1=25 r2=14]
FEATURE [Part::Fillet] Fillet404
  Base = -> Chamfer115
  Edges = 1 edges r=3: [Edge14]
FEATURE [Part::Fillet] Fillet405
  Base = -> Fillet404
  Edges = 2 edges r=3: [Edge9,Edge16]
FEATURE [Part::MultiFuse] Fusion700
  Refine = true
  Shapes = -> [Fusion699,Fillet405]
FEATURE [Part::Mirroring] Part__Mirroring092  label="leafspring-mount-rear-right"
  Base = (0,0,0)
  Normal = (0,1,0)
  Placement = pos=(5,170,5) rot=(0,0,1;0rad)
FEATURE [Part::Cut] Cut568  label="leafspring-mount-rear-left"
  Placement = pos=(5,0,5) rot=(0,0,1;0rad)
  Refine = true
FEATURE [Part::Cylinder] Cylinder1043  label="Cylinder1202"
  Angle = 360
  AttacherType = Attacher::AttachEngine3D
  Height = 10
  Placement = pos=(357,128,-42.5) rot=(0,1,0;1.5708rad)
  Radius = 1.3
FEATURE [Part::Cylinder] Cylinder1044  label="Cylinder1203"
  Angle = 360
  AttacherType = Attacher::AttachEngine3D
  Height = 10
  Placement = pos=(365,124,-8) rot=(1,0,0;1.5708rad)
  Radius = 1.3
FEATURE [Part::Cylinder] Cylinder1045  label="Cylinder1204"
  Angle = 360
  AttacherType = Attacher::AttachEngine3D
  Height = 10
  Placement = pos=(377,124,-8) rot=(1,0,0;1.5708rad)
  Radius = 1.3
FEATURE [Part::Cylinder] Cylinder1046  label="Cylinder1205"
  Angle = 360
  AttacherType = Attacher::AttachEngine3D
  Height = 10
  Placement = pos=(365,129.5,-8) rot=(1,0,0;1.5708rad)
  Radius = 3.1
FEATURE [Part::Cut] Cut014206
  Base = -> Fusion700
  Refine = true
  Tool = -> Cylinder1046
FEATURE [Part::Cylinder] Cylinder1047  label="Cylinder1206"
  Angle = 360
  AttacherType = Attacher::AttachEngine3D
  Height = 10
  Placement = pos=(371,110,-24) rot=(0,0,1;0rad)
  Radius = 1.3
FEATURE [Part::MultiFuse] Fusion701
  Refine = true
  Shapes = -> [Cylinder1043,Cylinder1044,Cylinder1045,Cylinder1047]
FEATURE [Part::Box] Box676  label="Cube867"
  AttacherType = Attacher::AttachEngine3D
  Height = 20
  Length = 20
  Placement = pos=(361,105,-18) rot=(0,0,1;0rad)
  Width = 11.5
FEATURE [Part::Cut] Cut014207
  Base = -> Cut014206
  Refine = true
  Tool = -> Box676
FEATURE [Part::Cut] Cut014208  label="central-axle-panhard-bar-upper-mount"
  Base = -> Cut014207
  Placement = pos=(1.5,0,0) rot=(0,0,1;0rad)
  Refine = true
  Tool = -> Fusion701
FEATURE [Part::Torus] Torus
  Angle1 = -180
  Angle2 = 180
  Angle3 = 360
  AttacherType = Attacher::AttachEngine3D
  Placement = pos=(348.5,40,-30) rot=(0,0,1;0rad)
  Radius1 = 7
  Radius2 = 5.5
FEATURE [Part::Torus] Torus001
  Angle1 = -180
  Angle2 = 180
  Angle3 = 360
  AttacherType = Attacher::AttachEngine3D
  Placement = pos=(348.5,40,-22) rot=(0,0,1;0rad)
  Radius1 = 7
  Radius2 = 5.5
FEATURE [Part::Torus] Torus002
  Angle1 = -180
  Angle2 = 180
  Angle3 = 360
  AttacherType = Attacher::AttachEngine3D
  Placement = pos=(348.5,40,-14) rot=(0,0,1;0rad)
  Radius1 = 7
  Radius2 = 5.5
FEATURE [Part::Cylinder] Cylinder1050  label="Cylinder1314"
  Angle = 360
  AttacherType = Attacher::AttachEngine3D
  Height = 5
  Placement = pos=(348.5,40,-12) rot=(0,0,1;0rad)
  Radius = 9
FEATURE [Part::Cylinder] Cylinder1051  label="Cylinder1290"
  Angle = 360
  AttacherType = Attacher::AttachEngine3D
  Height = 1
  Placement = pos=(348.5,40,-35.5) rot=(0,0,1;0rad)
  Radius = 13
FEATURE [Part::Cylinder] Cylinder1053  label="Cylinder1209"
  Angle = 360
  AttacherType = Attacher::AttachEngine3D
  Height = 1
  Placement = pos=(348.5,40,-8) rot=(0,0,1;0rad)
  Radius = 11.5
FEATURE [Part::Cylinder] Cylinder1054  label="Cylinder1210"
  Angle = 360
  AttacherType = Attacher::AttachEngine3D
  Height = 3
  Placement = pos=(348.5,40,-10) rot=(0,0,1;0rad)
  Radius = 10.5
FEATURE [Part::Torus] Torus003
  Angle1 = -180
  Angle2 = 180
  Angle3 = 360
  AttacherType = Attacher::AttachEngine3D
  Placement = pos=(348.5,40,-30) rot=(0,0,1;0rad)
  Radius1 = 7
  Radius2 = 5
FEATURE [Part::Torus] Torus004
  Angle1 = -180
  Angle2 = 180
  Angle3 = 360
  AttacherType = Attacher::AttachEngine3D
  Placement = pos=(348.5,40,-22) rot=(0,0,1;0rad)
  Radius1 = 7
  Radius2 = 5
FEATURE [Part::Torus] Torus005
  Angle1 = -180
  Angle2 = 180
  Angle3 = 360
  AttacherType = Attacher::AttachEngine3D
  Placement = pos=(348.5,40,-14) rot=(0,0,1;0rad)
  Radius1 = 7
  Radius2 = 5
FEATURE [Part::MultiFuse] Fusion704
  Refine = true
  Shapes = -> [Torus,Torus001,Torus002]
FEATURE [Part::MultiFuse] Fusion705
  Refine = true
  Shapes = -> [Torus003,Torus004,Torus005]
FEATURE [Part::Cylinder] Cylinder1056  label="Cylinder1211"
  Angle = 360
  AttacherType = Attacher::AttachEngine3D
  Height = 2
  Placement = pos=(348.5,40,-34.5) rot=(0,0,1;0rad)
  Radius = 10
FEATURE [Part::Cylinder] Cylinder1057  label="Cylinder1212"
  Angle = 360
  AttacherType = Attacher::AttachEngine3D
  Height = 36
  Placement = pos=(348.5,40,-34.5) rot=(0,0,1;0rad)
  Radius = 6
FEATURE [Part::Cut] Cut014209
  Base = -> Fusion704
  Refine = true
  Tool = -> Fusion705
FEATURE [Part::MultiFuse] Fusion706
  Refine = true
  Shapes = -> [Cut014209,Cylinder1054]
FEATURE [Part::Cut] Cut014210
  Base = -> Fusion706
  Refine = true
  Tool = -> Cylinder1051
FEATURE [Part::MultiFuse] Fusion707
  Refine = true
  Shapes = -> [Cylinder1053,Cut014210]
FEATURE [Part::Cut] Cut014211
  Base = -> Fusion707
  Refine = true
  Tool = -> Cylinder1050
FEATURE [Part::MultiFuse] Fusion708
  Refine = true
  Shapes = -> [Cut014211,Cylinder1056]
FEATURE [Part::Cut] Cut014212  label="central-axle-left-baloon"
  Base = -> Fusion708
  Refine = true
  Tool = -> Cylinder1057
FEATURE [Part::Cylinder] Cylinder1065  label="Cylinder1213"
  Angle = 360
  AttacherType = Attacher::AttachEngine3D
  Height = 6
  Placement = pos=(348.5,40,-9) rot=(0,0,1;0rad)
  Radius = 12.5
FEATURE [Part::Cylinder] Cylinder1066  label="Cylinder1214"
  Angle = 360
  AttacherType = Attacher::AttachEngine3D
  Height = 3
  Placement = pos=(348.5,40,-10) rot=(0,0,1;0rad)
  Radius = 10.5
FEATURE [Part::Cylinder] Cylinder1067  label="Cylinder1215"
  Angle = 360
  AttacherType = Attacher::AttachEngine3D
  Height = 1.5
  Placement = pos=(348.5,40,-8.25) rot=(0,0,1;0rad)
  Radius = 11.75
FEATURE [Part::MultiFuse] Fusion711
  Placement = pos=(0,0,1) rot=(0,0,1;0rad)
  Refine = true
  Shapes = -> [Cylinder1067,Cylinder1066]
FEATURE [Part::Box] Box677  label="Cube868"
  AttacherType = Attacher::AttachEngine3D
  Height = 6
  Length = 25
  Placement = pos=(336,40,-9) rot=(0,0,1;0rad)
  Width = 13.5
FEATURE [Part::Box] Box678  label="Cube869"
  AttacherType = Attacher::AttachEngine3D
  Height = 14
  Length = 40
  Placement = pos=(328.5,51.5,-15) rot=(0,0,1;0rad)
  Width = 2
FEATURE [Part::Cylinder] Cylinder1068  label="Cylinder1216"
  Angle = 360
  AttacherType = Attacher::AttachEngine3D
  Height = 6
  Placement = pos=(348.5,40,-15) rot=(0,0,1;0rad)
  Radius = 13
FEATURE [Part::Cylinder] Cylinder1069  label="Cylinder1217"
  Angle = 360
  AttacherType = Attacher::AttachEngine3D
  Height = 5
  Placement = pos=(348.5,40,-8.5) rot=(0,0,1;0rad)
  Radius = 10.5
FEATURE [Part::Cylinder] Cylinder1070  label="Cylinder1218"
  Angle = 360
  AttacherType = Attacher::AttachEngine3D
  Height = 12
  Placement = pos=(332.5,44,-8) rot=(-1,0,0;1.5708rad)
  Radius = 1.6
FEATURE [Part::Cylinder] Cylinder1071  label="Cylinder1219"
  Angle = 360
  AttacherType = Attacher::AttachEngine3D
  Height = 12
  Placement = pos=(364.5,44,-8) rot=(-1,0,0;1.5708rad)
  Radius = 1.6
FEATURE [Part::MultiFuse] Fusion713
  Refine = true
  Shapes = -> [Cylinder1071,Cylinder1070]
FEATURE [Part::Torus] Torus007
  Angle1 = -180
  Angle2 = 180
  Angle3 = 360
  AttacherType = Attacher::AttachEngine3D
  Placement = pos=(348.5,40,-30) rot=(0,0,1;0rad)
  Radius1 = 7
  Radius2 = 5.5
FEATURE [Part::Cylinder] Cylinder1072  label="Cylinder1220"
  Angle = 360
  AttacherType = Attacher::AttachEngine3D
  Height = 1
  Placement = pos=(348.5,40,-25.5) rot=(0,0,1;0rad)
  Radius = 13
FEATURE [Part::Cylinder] Cylinder1073  label="Cylinder1221"
  Angle = 360
  AttacherType = Attacher::AttachEngine3D
  Height = 11
  Placement = pos=(348.5,40,-13.5) rot=(0,0,1;0rad)
  Radius = 8
FEATURE [Part::Cylinder] Cylinder1074  label="Cylinder1222"
  Angle = 360
  AttacherType = Attacher::AttachEngine3D
  Height = 1.5
  Placement = pos=(348.5,40,-11.5) rot=(0,0,1;0rad)
  Radius = 12.5
FEATURE [Part::Cut] Cut014221
  Base = -> Torus007
  Placement = pos=(0,0,16) rot=(0,0,1;0rad)
  Refine = true
  Tool = -> Cylinder1072
FEATURE [Part::Cut] Cut014222
  Base = -> Cylinder1074
  Refine = true
  Tool = -> Cut014221
FEATURE [Part::Cut] Cut014223
  Base = -> Cut014222
  Placement = pos=(0,0,1) rot=(0,0,1;0rad)
  Refine = true
  Tool = -> Cylinder1073
FEATURE [Part::Cylinder] Cylinder1075  label="Cylinder1223"
  Angle = 360
  AttacherType = Attacher::AttachEngine3D
  Height = 2.5
  Placement = pos=(348.5,40,-12.5) rot=(0,0,1;0rad)
  Radius = 12.5
FEATURE [Part::Box] Box679  label="Cube870"
  AttacherType = Attacher::AttachEngine3D
  Height = 5
  Length = 1
  Placement = pos=(336.5,40,-15) rot=(0,0,1;0rad)
  Width = 13.5
FEATURE [Part::Chamfer] Chamfer116
  Base = -> Box679
  Edges = 1 edges: [Edge9 r1=4.99 r2=12]
FEATURE [Part::Box] Box680  label="Cube871"
  AttacherType = Attacher::AttachEngine3D
  Height = 5
  Length = 1
  Placement = pos=(336.5,40,-15) rot=(0,0,1;0rad)
  Width = 13.5
FEATURE [Part::Chamfer] Chamfer117
  Base = -> Box680
  Edges = 1 edges: [Edge9 r1=4.99 r2=12]
  Placement = pos=(24,0,0) rot=(0,0,1;0rad)
FEATURE [Part::MultiFuse] Fusion714
  Placement = pos=(-0.5,0,0) rot=(0,0,1;0rad)
  Refine = true
  Shapes = -> [Chamfer116,Chamfer117]
FEATURE [Part::Cut] Cut014224
  Base = -> Fusion714
  Placement = pos=(0,0,1) rot=(0,0,1;0rad)
  Refine = true
  Tool = -> Cylinder1075
FEATURE [Part::Torus] Torus008
  Angle1 = -180
  Angle2 = 180
  Angle3 = 360
  AttacherType = Attacher::AttachEngine3D
  Placement = pos=(348.5,40,-30) rot=(0,0,1;0rad)
  Radius1 = 7
  Radius2 = 5.5
FEATURE [Part::Torus] Torus009
  Angle1 = -180
  Angle2 = 180
  Angle3 = 360
  AttacherType = Attacher::AttachEngine3D
  Placement = pos=(348.5,40,-22) rot=(0,0,1;0rad)
  Radius1 = 7
  Radius2 = 5.5
FEATURE [Part::Torus] Torus010
  Angle1 = -180
  Angle2 = 180
  Angle3 = 360
  AttacherType = Attacher::AttachEngine3D
  Placement = pos=(348.5,40,-14) rot=(0,0,1;0rad)
  Radius1 = 7
  Radius2 = 5.5
FEATURE [Part::Cylinder] Cylinder1076  label="Cylinder1224"
  Angle = 360
  AttacherType = Attacher::AttachEngine3D
  Height = 5
  Placement = pos=(348.5,40,-12) rot=(0,0,1;0rad)
  Radius = 9
FEATURE [Part::Cylinder] Cylinder1077  label="Cylinder1225"
  Angle = 360
  AttacherType = Attacher::AttachEngine3D
  Height = 1
  Placement = pos=(348.5,40,-35.5) rot=(0,0,1;0rad)
  Radius = 13
FEATURE [Part::Cylinder] Cylinder1078  label="Cylinder1226"
  Angle = 360
  AttacherType = Attacher::AttachEngine3D
  Height = 1
  Placement = pos=(348.5,40,-8) rot=(0,0,1;0rad)
  Radius = 11.5
FEATURE [Part::Cylinder] Cylinder1079  label="Cylinder1227"
  Angle = 360
  AttacherType = Attacher::AttachEngine3D
  Height = 3
  Placement = pos=(348.5,40,-10) rot=(0,0,1;0rad)
  Radius = 10.5
FEATURE [Part::Torus] Torus011
  Angle1 = -180
  Angle2 = 180
  Angle3 = 360
  AttacherType = Attacher::AttachEngine3D
  Placement = pos=(348.5,40,-30) rot=(0,0,1;0rad)
  Radius1 = 7
  Radius2 = 5
FEATURE [Part::Torus] Torus012
  Angle1 = -180
  Angle2 = 180
  Angle3 = 360
  AttacherType = Attacher::AttachEngine3D
  Placement = pos=(348.5,40,-22) rot=(0,0,1;0rad)
  Radius1 = 7
  Radius2 = 5
FEATURE [Part::Torus] Torus013
  Angle1 = -180
  Angle2 = 180
  Angle3 = 360
  AttacherType = Attacher::AttachEngine3D
  Placement = pos=(348.5,40,-14) rot=(0,0,1;0rad)
  Radius1 = 7
  Radius2 = 5
FEATURE [Part::MultiFuse] Fusion716
  Refine = true
  Shapes = -> [Torus008,Torus009,Torus010]
FEATURE [Part::MultiFuse] Fusion717
  Refine = true
  Shapes = -> [Torus011,Torus012,Torus013]
FEATURE [Part::Cylinder] Cylinder1080  label="Cylinder1228"
  Angle = 360
  AttacherType = Attacher::AttachEngine3D
  Height = 2
  Placement = pos=(348.5,40,-34.5) rot=(0,0,1;0rad)
  Radius = 10
FEATURE [Part::Cylinder] Cylinder1081  label="Cylinder1229"
  Angle = 360
  AttacherType = Attacher::AttachEngine3D
  Height = 36
  Placement = pos=(348.5,40,-34.5) rot=(0,0,1;0rad)
  Radius = 6
FEATURE [Part::Cut] Cut014225
  Base = -> Fusion716
  Refine = true
  Tool = -> Fusion717
FEATURE [Part::MultiFuse] Fusion718
  Refine = true
  Shapes = -> [Cut014225,Cylinder1079]
FEATURE [Part::Cut] Cut014226
  Base = -> Fusion718
  Refine = true
  Tool = -> Cylinder1077
FEATURE [Part::MultiFuse] Fusion719
  Refine = true
  Shapes = -> [Cylinder1078,Cut014226]
FEATURE [Part::Cut] Cut014227
  Base = -> Fusion719
  Refine = true
  Tool = -> Cylinder1076
FEATURE [Part::MultiFuse] Fusion720
  Refine = true
  Shapes = -> [Cut014227,Cylinder1080]
FEATURE [Part::Cut] Cut014228  label="central-axle-right-baloon"
  Base = -> Fusion720
  Placement = pos=(0,90,0) rot=(0,0,1;0rad)
  Refine = true
  Tool = -> Cylinder1081
FEATURE [Part::Cylinder] Cylinder1089  label="Cylinder1291"
  Angle = 360
  AttacherType = Attacher::AttachEngine3D
  Height = 6
  Placement = pos=(348.5,130.5,-9) rot=(0,0,1;0rad)
  Radius = 12.5
FEATURE [Part::Cylinder] Cylinder1090  label="Cylinder1315"
  Angle = 360
  AttacherType = Attacher::AttachEngine3D
  Height = 3
  Placement = pos=(348.5,40,-10) rot=(0,0,1;0rad)
  Radius = 10.5
FEATURE [Part::Cylinder] Cylinder1091  label="Cylinder1363"
  Angle = 360
  AttacherType = Attacher::AttachEngine3D
  Height = 1.5
  Placement = pos=(348.5,40,-8.25) rot=(0,0,1;0rad)
  Radius = 11.75
FEATURE [Part::MultiFuse] Fusion723
  Placement = pos=(0,90.5,1) rot=(0,0,1;0rad)
  Refine = true
  Shapes = -> [Cylinder1091,Cylinder1090]
FEATURE [Part::Box] Box682  label="Cube873"
  AttacherType = Attacher::AttachEngine3D
  Height = 6
  Length = 25
  Placement = pos=(336,117,-9) rot=(0,0,1;0rad)
  Width = 13.5
FEATURE [Part::Box] Box683  label="Cube874"
  AttacherType = Attacher::AttachEngine3D
  Height = 14
  Length = 34
  Placement = pos=(328.5,116.5,-15) rot=(0,0,1;0rad)
  Width = 2
FEATURE [Part::Cylinder] Cylinder1092  label="Cylinder1243"
  Angle = 360
  AttacherType = Attacher::AttachEngine3D
  Height = 6
  Placement = pos=(348.5,130.5,-15) rot=(0,0,1;0rad)
  Radius = 13
FEATURE [Part::Cylinder] Cylinder1093  label="Cylinder1244"
  Angle = 360
  AttacherType = Attacher::AttachEngine3D
  Height = 5
  Placement = pos=(348.5,130.5,-8.5) rot=(0,0,1;0rad)
  Radius = 10.5
FEATURE [Part::Cylinder] Cylinder1094  label="Cylinder1245"
  Angle = 360
  AttacherType = Attacher::AttachEngine3D
  Height = 12
  Placement = pos=(332.5,109,-8) rot=(-1,0,0;1.5708rad)
  Radius = 1.6
FEATURE [Part::Torus] Torus015
  Angle1 = -180
  Angle2 = 180
  Angle3 = 360
  AttacherType = Attacher::AttachEngine3D
  Placement = pos=(348.5,40,-30) rot=(0,0,1;0rad)
  Radius1 = 7
  Radius2 = 5.5
FEATURE [Part::Cylinder] Cylinder1096  label="Cylinder1247"
  Angle = 360
  AttacherType = Attacher::AttachEngine3D
  Height = 1
  Placement = pos=(348.5,40,-25.5) rot=(0,0,1;0rad)
  Radius = 13
FEATURE [Part::Cylinder] Cylinder1097  label="Cylinder1248"
  Angle = 360
  AttacherType = Attacher::AttachEngine3D
  Height = 11
  Placement = pos=(348.5,40,-13.5) rot=(0,0,1;0rad)
  Radius = 8
FEATURE [Part::Cylinder] Cylinder1098  label="Cylinder1249"
  Angle = 360
  AttacherType = Attacher::AttachEngine3D
  Height = 1.5
  Placement = pos=(348.5,40,-11.5) rot=(0,0,1;0rad)
  Radius = 12.5
FEATURE [Part::Cut] Cut014238
  Base = -> Torus015
  Placement = pos=(0,0,16) rot=(0,0,1;0rad)
  Refine = true
  Tool = -> Cylinder1096
FEATURE [Part::Cut] Cut014239
  Base = -> Cylinder1098
  Refine = true
  Tool = -> Cut014238
FEATURE [Part::Cut] Cut014240
  Base = -> Cut014239
  Placement = pos=(0,90.5,1) rot=(0,0,1;0rad)
  Refine = true
  Tool = -> Cylinder1097
FEATURE [Part::Cylinder] Cylinder1099  label="Cylinder1250"
  Angle = 360
  AttacherType = Attacher::AttachEngine3D
  Height = 2.5
  Placement = pos=(348.5,40,-12.5) rot=(0,0,1;0rad)
  Radius = 12.5
FEATURE [Part::Box] Box684  label="Cube875"
  AttacherType = Attacher::AttachEngine3D
  Height = 5
  Length = 1
  Placement = pos=(336.5,40,-15) rot=(0,0,1;0rad)
  Width = 13.5
FEATURE [Part::Chamfer] Chamfer118
  Base = -> Box684
  Edges = 1 edges: [Edge9 r1=4.99 r2=12]
FEATURE [Part::Box] Box685  label="Cube876"
  AttacherType = Attacher::AttachEngine3D
  Height = 5
  Length = 1
  Placement = pos=(336.5,40,-15) rot=(0,0,1;0rad)
  Width = 13.5
FEATURE [Part::Chamfer] Chamfer119
  Base = -> Box685
  Edges = 1 edges: [Edge9 r1=4.99 r2=12]
  Placement = pos=(24,0,0) rot=(0,0,1;0rad)
FEATURE [Part::MultiFuse] Fusion726
  Placement = pos=(-0.5,0,0) rot=(0,0,1;0rad)
  Refine = true
  Shapes = -> [Chamfer118,Chamfer119]
FEATURE [Part::Cut] Cut014241
  Base = -> Fusion726
  Refine = true
  Tool = -> Cylinder1099
FEATURE [Part::Mirroring] Part__Mirroring093  label="Cut014241 (Mirror #11)"
  Base = (0,0,0)
  Normal = (0,1,0)
  Placement = pos=(0,170,1) rot=(0,0,1;0rad)
  Source = -> Cut014241
FEATURE [Part::Cylinder] Cylinder1100  label="Cylinder1251"
  Angle = 360
  AttacherType = Attacher::AttachEngine3D
  Height = 12
  Placement = pos=(357.5,109,-8) rot=(-1,0,0;1.5708rad)
  Radius = 1.25
FEATURE [Part::MultiFuse] Fusion729
  Refine = true
  Shapes = -> [Cylinder1094,Cylinder1100]
FEATURE [Part::Cylinder] Cylinder1101  label="Cylinder1254"
  Angle = 360
  AttacherType = Attacher::AttachEngine3D
  Height = 12
  Placement = pos=(332.5,109,-8) rot=(-1,0,0;1.5708rad)
  Radius = 1.6
FEATURE [Part::Cylinder] Cylinder1102  label="Cylinder1255"
  Angle = 360
  AttacherType = Attacher::AttachEngine3D
  Height = 12
  Placement = pos=(357.5,109,-8) rot=(-1,0,0;1.5708rad)
  Radius = 1.25
FEATURE [Part::MultiFuse] Fusion730
  Refine = true
  Shapes = -> [Cylinder1101,Cylinder1102]
FEATURE [Part::Cylinder] Cylinder1103  label="Cylinder1258"
  Angle = 360
  AttacherType = Attacher::AttachEngine3D
  Height = 12
  Placement = pos=(332.5,44,-8) rot=(-1,0,0;1.5708rad)
  Radius = 1.6
FEATURE [Part::Cylinder] Cylinder1104  label="Cylinder1259"
  Angle = 360
  AttacherType = Attacher::AttachEngine3D
  Height = 12
  Placement = pos=(364.5,44,-8) rot=(-1,0,0;1.5708rad)
  Radius = 1.6
FEATURE [Part::MultiFuse] Fusion731
  Refine = true
  Shapes = -> [Cylinder1104,Cylinder1103]
FEATURE [Part::Box] Box686  label="Cube877"
  AttacherType = Attacher::AttachEngine3D
  Height = 26
  Length = 40
  Placement = pos=(279,50.5,-21) rot=(0,0,1;0rad)
  Width = 10
FEATURE [Part::Box] Box687  label="Cube878"
  AttacherType = Attacher::AttachEngine3D
  Height = 20
  Length = 40
  Placement = pos=(279,53.5,-18) rot=(0,0,1;0rad)
  Width = 11.5
FEATURE [Part::Cut] Cut014246
  Base = -> Box686
  Placement = pos=(49.5,0,0) rot=(0,0,1;0rad)
  Refine = true
  Tool = -> Box687
FEATURE [Part::Box] Box688  label="Cube879"
  AttacherType = Attacher::AttachEngine3D
  Height = 26
  Length = 33
  Placement = pos=(279,109.5,-21) rot=(0,0,1;0rad)
  Width = 10
FEATURE [Part::Box] Box689  label="Cube880"
  AttacherType = Attacher::AttachEngine3D
  Height = 20
  Length = 33
  Placement = pos=(279,105,-18) rot=(0,0,1;0rad)
  Width = 11.5
FEATURE [Part::Cut] Cut014247
  Base = -> Box688
  Placement = pos=(49.5,0,0) rot=(0,0,1;0rad)
  Refine = true
  Tool = -> Box689
FEATURE [Part::Cut] Cut014248  label="central-axle-left-baloon-upper-retainer-HOLES"
  Base = -> Cut014246
  Refine = true
  Tool = -> Fusion731
FEATURE [Part::Cut] Cut014249  label="central-axle-right-baloon-upper-retainer-HOLES"
  Base = -> Cut014247
  Refine = true
  Tool = -> Fusion730
FEATURE [Part::MultiFuse] Fusion732
  Refine = true
  Shapes = -> [Box682,Cylinder1089,Box683]
FEATURE [Part::Cut] Cut014250
  Base = -> Fusion732
  Refine = true
  Tool = -> Fusion723
FEATURE [Part::Cut] Cut014251
  Base = -> Cut014250
  Refine = true
  Tool = -> Cylinder1093
FEATURE [Part::Chamfer] Chamfer120
  Base = -> Cut014251
  Edges = 1 edges r=1.2: [Edge2]
FEATURE [Part::Cut] Cut014252
  Base = -> Chamfer120
  Refine = true
  Tool = -> Cylinder1092
FEATURE [Part::MultiFuse] Fusion733
  Refine = true
  Shapes = -> [Cut014240,Part__Mirroring093,Cut014252]
FEATURE [Part::Cut] Cut014253
  Base = -> Fusion733
  Refine = true
  Tool = -> Fusion729
FEATURE [Part::Fillet] Fillet407
  Base = -> Cut014253
  Edges = 2 edges r=3: [Edge66,Edge69]
FEATURE [Part::Fillet] Fillet408  label="central-axle-right-baloon-upper-retainer"
  Base = -> Fillet407
  Edges = 1 edges r=1: [Edge57]
FEATURE [Part::MultiFuse] Fusion734
  Refine = true
  Shapes = -> [Box677,Cylinder1065,Box678]
FEATURE [Part::Cut] Cut014254
  Base = -> Fusion734
  Refine = true
  Tool = -> Fusion711
FEATURE [Part::Chamfer] Chamfer121
  Base = -> Cut014254
  Edges = 1 edges r=1.2: [Edge27]
FEATURE [Part::Cut] Cut014255
  Base = -> Chamfer121
  Refine = true
  Tool = -> Cylinder1068
FEATURE [Part::Cut] Cut014256
  Base = -> Cut014255
  Refine = true
  Tool = -> Cylinder1069
FEATURE [Part::Cut] Cut014257
  Base = -> Cut014256
  Refine = true
  Tool = -> Fusion713
FEATURE [Part::Fillet] Fillet409
  Base = -> Cut014257
  Edges = 4 edges r=3: [Edge35,Edge36,Edge37,Edge40]
FEATURE [Part::Fillet] Fillet410
  Base = -> Fillet409
  Edges = 1 edges r=1: [Edge38]
FEATURE [Part::MultiFuse] Fusion735  label="central-axle-left-baloon-upper-retainer"
  Refine = true
  Shapes = -> [Cut014223,Cut014224,Fillet410]
FEATURE [Part::Torus] Torus017
  Angle1 = -180
  Angle2 = 180
  Angle3 = 360
  AttacherType = Attacher::AttachEngine3D
  Placement = pos=(348.5,40,-30) rot=(0,0,1;0rad)
  Radius1 = 7
  Radius2 = 5.5
FEATURE [Part::Cylinder] Cylinder1111  label="Cylinder1317"
  Angle = 360
  AttacherType = Attacher::AttachEngine3D
  Height = 1
  Placement = pos=(348.5,40,-35.5) rot=(0,0,1;0rad)
  Radius = 13
FEATURE [Part::Cut] Cut014264
  Base = -> Torus017
  Refine = true
  Tool = -> Cylinder1111
FEATURE [Part::Cylinder] Cylinder1112  label="Cylinder1318"
  Angle = 360
  AttacherType = Attacher::AttachEngine3D
  Height = 2.5
  Placement = pos=(348.5,40,-35.5) rot=(0,0,1;0rad)
  Radius = 12
FEATURE [Part::Cut] Cut014265
  Base = -> Cylinder1112
  Refine = true
  Tool = -> Cut014264
FEATURE [Part::Cylinder] Cylinder1115  label="Cylinder1364"
  Angle = 360
  AttacherType = Attacher::AttachEngine3D
  Height = 14
  Placement = pos=(348.5,40,-35.5) rot=(0,0,1;0rad)
  Radius = 1.25
FEATURE [Part::Cone] Cone
  Angle = 360
  AttacherType = Attacher::AttachEngine3D
  Height = 13
  Placement = pos=(348.5,40,-34.5) rot=(0,0,1;0rad)
  Radius1 = 5.5
  Radius2 = 4
FEATURE [Part::MultiFuse] Fusion739
  Refine = true
  Shapes = -> [Cut014265,Cone]
FEATURE [Part::Cut] Cut014266  label="central-axle-left-baloon-plate"
  Base = -> Fusion739
  Refine = true
  Tool = -> Cylinder1115
FEATURE [Part::Torus] Torus018
  Angle1 = -180
  Angle2 = 180
  Angle3 = 360
  AttacherType = Attacher::AttachEngine3D
  Placement = pos=(348.5,40,-30) rot=(0,0,1;0rad)
  Radius1 = 7
  Radius2 = 5.5
FEATURE [Part::Cylinder] Cylinder1116  label="Cylinder1365"
  Angle = 360
  AttacherType = Attacher::AttachEngine3D
  Height = 1
  Placement = pos=(348.5,40,-35.5) rot=(0,0,1;0rad)
  Radius = 13
FEATURE [Part::Cut] Cut014267
  Base = -> Torus018
  Refine = true
  Tool = -> Cylinder1116
FEATURE [Part::Cylinder] Cylinder1117  label="Cylinder1321"
  Angle = 360
  AttacherType = Attacher::AttachEngine3D
  Height = 2.5
  Placement = pos=(348.5,40,-35.5) rot=(0,0,1;0rad)
  Radius = 12
FEATURE [Part::Cut] Cut014268
  Base = -> Cylinder1117
  Refine = true
  Tool = -> Cut014267
FEATURE [Part::Cylinder] Cylinder1118  label="Cylinder1366"
  Angle = 360
  AttacherType = Attacher::AttachEngine3D
  Height = 14
  Placement = pos=(348.5,40,-35.5) rot=(0,0,1;0rad)
  Radius = 1.25
FEATURE [Part::Cone] Cone001
  Angle = 360
  AttacherType = Attacher::AttachEngine3D
  Height = 13
  Placement = pos=(348.5,40,-34.5) rot=(0,0,1;0rad)
  Radius1 = 5.5
  Radius2 = 4
FEATURE [Part::MultiFuse] Fusion740
  Refine = true
  Shapes = -> [Cut014268,Cone001]
FEATURE [Part::Cut] Cut014269
  Base = -> Fusion740
  Placement = pos=(0,90,0) rot=(0,0,1;0rad)
  Refine = true
  Tool = -> Cylinder1118
FEATURE [Part::Box] Box690  label="Cube881"
  AttacherType = Attacher::AttachEngine3D
  Height = 10
  Length = 10
  Placement = pos=(355.5,121,-37.5) rot=(0,1,0;0.872665rad)
  Width = 20
FEATURE [Part::Cut] Cut014270  label="central-axle-right-baloon-plate"
  Base = -> Cut014269
  Refine = true
  Tool = -> Box690
FEATURE [Part::Cylinder] Cylinder1019  label="Cylinder1367"
  Angle = 360
  AttacherType = Attacher::AttachEngine3D
  Height = 170
  Placement = pos=(509,170,7) rot=(1,0,0;1.5708rad)
  Radius = 5
FEATURE [Part::Box] Box691  label="Cube882"
  AttacherType = Attacher::AttachEngine3D
  Height = 10
  Length = 224
  Placement = pos=(290,55,2) rot=(0,0,1;0rad)
  Width = 10
FEATURE [Part::Box] Box692  label="Cube883"
  AttacherType = Attacher::AttachEngine3D
  Height = 10
  Length = 224
  Placement = pos=(290,105,2) rot=(0,0,1;0rad)
  Width = 10
FEATURE [Part::Cylinder] Cylinder1178  label="Cylinder1368"
  Angle = 360
  AttacherType = Attacher::AttachEngine3D
  Height = 170
  Placement = pos=(285,170,7) rot=(1,0,0;1.5708rad)
  Radius = 5
FEATURE [Part::MultiFuse] Fusion368
  Refine = true
  Shapes = -> [Box692,Box691,Cylinder1019,Cylinder1178]
FEATURE [Part::Fillet] Fillet411  label="kipper-frame-ALU_"
  Base = -> Fusion368
  Edges = 2 edges r=5: [Edge59,Edge60]
FEATURE [Part::Cylinder] Cylinder050
  Angle = 360
  AttacherType = Attacher::AttachEngine3D
  Height = 20
  Placement = pos=(390,85,4.5) rot=(0,1,0;1.5708rad)
  Radius = 20.5
FEATURE [Part::Cylinder] Cylinder051
  Angle = 360
  AttacherType = Attacher::AttachEngine3D
  Height = 10
  Placement = pos=(400,85,12) rot=(0,1,0;1.5708rad)
  Radius = 7
FEATURE [Part::Cylinder] Cylinder052
  Angle = 360
  AttacherType = Attacher::AttachEngine3D
  Height = 75
  Placement = pos=(331,85,5) rot=(0,1,0;1.5708rad)
  Radius = 18.7
FEATURE [Part::Cylinder] Cylinder053
  Angle = 360
  AttacherType = Attacher::AttachEngine3D
  Height = 10
  Placement = pos=(15.5,0,0) rot=(0,0,1;0rad)
  Radius = 1.6
FEATURE [Part::Cylinder] Cylinder054
  Angle = 360
  AttacherType = Attacher::AttachEngine3D
  Height = 10
  Placement = pos=(-15.5,0,0) rot=(0,0,1;0rad)
  Radius = 1.6
FEATURE [Part::MultiFuse] Fusion041
  Placement = pos=(0,0,0) rot=(0,0,1;1.0472rad)
  Refine = true
  Shapes = -> [Cylinder054,Cylinder053]
FEATURE [Part::Cylinder] Cylinder055
  Angle = 360
  AttacherType = Attacher::AttachEngine3D
  Height = 10
  Placement = pos=(15.5,0,0) rot=(0,0,1;0rad)
  Radius = 1.6
FEATURE [Part::Cylinder] Cylinder056
  Angle = 360
  AttacherType = Attacher::AttachEngine3D
  Height = 10
  Placement = pos=(-15.5,0,0) rot=(0,0,1;0rad)
  Radius = 1.6
FEATURE [Part::MultiFuse] Fusion042
  Placement = pos=(0,0,0) rot=(0,0,1;2.0944rad)
  Refine = true
  Shapes = -> [Cylinder056,Cylinder055]
FEATURE [Part::Cylinder] Cylinder057
  Angle = 360
  AttacherType = Attacher::AttachEngine3D
  Height = 10
  Placement = pos=(-15.5,0,0) rot=(0,0,1;0rad)
  Radius = 1.6
FEATURE [Part::Cylinder] Cylinder058
  Angle = 360
  AttacherType = Attacher::AttachEngine3D
  Height = 10
  Placement = pos=(15.5,0,0) rot=(0,0,1;0rad)
  Radius = 1.6
FEATURE [Part::MultiFuse] Fusion043
  Refine = true
  Shapes = -> [Cylinder057,Cylinder058]
FEATURE [Part::MultiFuse] Fusion044
  Placement = pos=(0,0,0) rot=(0,0,1;0.523599rad)
  Refine = true
  Shapes = -> [Fusion041,Fusion042,Fusion043]
FEATURE [Part::Box] Box023  label="Cube002"
  AttacherType = Attacher::AttachEngine3D
  Height = 10
  Length = 10
  Width = 10
FEATURE [Part::Cut] Cut026  label="holes"
  Base = -> Fusion044
  Placement = pos=(408,85,2) rot=(0,1,0;1.5708rad)
  Refine = true
  Tool = -> Box023
FEATURE [Part::Cylinder] Cylinder059
  Angle = 360
  AttacherType = Attacher::AttachEngine3D
  Height = 22
  Placement = pos=(417,85,5) rot=(0,1,0;1.5708rad)
  Radius = 18.7
FEATURE [Part::Cylinder] Cylinder060
  Angle = 360
  AttacherType = Attacher::AttachEngine3D
  Height = 31
  Placement = pos=(439,85,5) rot=(0,1,0;1.5708rad)
  Radius = 17.5
FEATURE [Part::Cut] Cut014319
  Base = -> Cylinder050
  Refine = true
  Tool = -> Cylinder052
FEATURE [Part::Cut] Cut014320
  Base = -> Cut014319
  Placement = pos=(823,170,-3) rot=(0,0,1;3.14159rad)
  Refine = true
  Tool = -> Cylinder051
FEATURE [Part::Cylinder] Cylinder1207  label="Cylinder1378"
  Angle = 360
  AttacherType = Attacher::AttachEngine3D
  Height = 6
  Placement = pos=(411,85,12) rot=(0,1,0;1.5708rad)
  Radius = 7
FEATURE [Part::Cylinder] Cylinder1208  label="Cylinder1379"
  Angle = 360
  AttacherType = Attacher::AttachEngine3D
  Height = 150
  Placement = pos=(290,85,12) rot=(0,1,0;1.5708rad)
  Radius = 4
FEATURE [Part::Box] Box831  label="Cube928"
  AttacherType = Attacher::AttachEngine3D
  Height = 17
  Length = 10
  Placement = pos=(-2,0,1.5) rot=(0,0,1;0rad)
  Width = 60
FEATURE [Part::Fillet] Fillet007070
  Base = -> Box831
  Edges = 4 edges r=3: [Edge9,Edge10,Edge11,Edge12]
  Placement = pos=(485.5,55,-23) rot=(0,0,1;0rad)
FEATURE [Part::Box] Box832  label="Cube929"
  AttacherType = Attacher::AttachEngine3D
  Height = 10
  Length = 10
  Placement = pos=(483.5,63,-7.5) rot=(0,0,1;0rad)
  Width = 44
FEATURE [Part::Cut] Cut014331  label="Cut014449"
  Base = -> Fillet007070
  Refine = true
  Tool = -> Box832
FEATURE [Part::Cylinder] Cylinder1236  label="Cylinder1591"
  Angle = 360
  AttacherType = Attacher::AttachEngine3D
  Height = 10
  Placement = pos=(3,60,10) rot=(1,0,0;1.5708rad)
  Radius = 1.2
FEATURE [Part::Cylinder] Cylinder1237  label="Cylinder1592"
  Angle = 360
  AttacherType = Attacher::AttachEngine3D
  Height = 10
  Placement = pos=(3,10,10) rot=(1,0,0;1.5708rad)
  Radius = 1.2
FEATURE [Part::MultiFuse] Fusion248002159  label="Fusion248002266"
  Placement = pos=(485.5,55,-23) rot=(0,0,1;0rad)
  Refine = true
  Shapes = -> [Cylinder1236,Cylinder1237]
FEATURE [Part::Chamfer] Chamfer180
  Base = -> Cut014331
  Edges = 2 edges r=2.99: [Edge18,Edge25]
FEATURE [Part::Cut] Cut014332  label="Cut014450"
  Base = -> Chamfer180
  Placement = pos=(18,0,5) rot=(0,0,1;0rad)
  Refine = true
  Tool = -> Fusion248002159
FEATURE [Part::Cylinder] Cylinder1238  label="Cylinder1593"
  Angle = 360
  AttacherType = Attacher::AttachEngine3D
  Height = 10
  Placement = pos=(483.5,85,-14.5) rot=(0,1,0;1.5708rad)
  Radius = 2.6
FEATURE [Part::Cylinder] Cylinder1239  label="Cylinder1594"
  Angle = 360
  AttacherType = Attacher::AttachEngine3D
  Height = 10
  Placement = pos=(483.5,79,-10.5) rot=(0,1,0;1.5708rad)
  Radius = 1.2
FEATURE [Part::Cylinder] Cylinder1240  label="Cylinder1595"
  Angle = 360
  AttacherType = Attacher::AttachEngine3D
  Height = 10
  Placement = pos=(483.5,91,-10.5) rot=(0,1,0;1.5708rad)
  Radius = 1.2
FEATURE [Part::Cylinder] Cylinder1241  label="Cylinder1596"
  Angle = 360
  AttacherType = Attacher::AttachEngine3D
  Height = 10
  Placement = pos=(483.5,79,-18.5) rot=(0,1,0;1.5708rad)
  Radius = 1.2
FEATURE [Part::Cylinder] Cylinder1242  label="Cylinder1597"
  Angle = 360
  AttacherType = Attacher::AttachEngine3D
  Height = 10
  Placement = pos=(483.5,91,-18.5) rot=(0,1,0;1.5708rad)
  Radius = 1.2
FEATURE [Part::MultiFuse] Fusion248002160  label="Fusion248002267"
  Placement = pos=(18,0,5) rot=(0,0,1;0rad)
  Refine = true
  Shapes = -> [Cylinder1238,Cylinder1242,Cylinder1239,Cylinder1240,Cylinder1241]
FEATURE [Part::Cut] Cut014333  label="Cut014451"
  Base = -> Cut014332
  Placement = pos=(0.5,0,0) rot=(0,0,1;0rad)
  Refine = true
  Tool = -> Fusion248002160
FEATURE [Part::Cylinder] Cylinder1262  label="Cylinder1616"
  Angle = 360
  AttacherType = Attacher::AttachEngine3D
  Height = 10
  Placement = pos=(509,61,-10.5) rot=(0,1,0;1.5708rad)
  Radius = 1.1
FEATURE [Part::Cylinder] Cylinder1263  label="Cylinder1617"
  Angle = 360
  AttacherType = Attacher::AttachEngine3D
  Height = 10
  Placement = pos=(509,58,-14.5) rot=(0,1,0;1.5708rad)
  Radius = 1.1
FEATURE [Part::MultiFuse] Fusion248002174  label="Fusion248002280"
  Placement = pos=(-7,0,0) rot=(0,0,1;0rad)
  Refine = true
  Shapes = -> [Cylinder1263,Cylinder1262]
FEATURE [Part::Cylinder] Cylinder1264  label="Cylinder1618"
  Angle = 360
  AttacherType = Attacher::AttachEngine3D
  Height = 10
  Placement = pos=(509,64,-14.5) rot=(0,1,0;1.5708rad)
  Radius = 1.1
FEATURE [Part::Cylinder] Cylinder1265  label="Cylinder1619"
  Angle = 360
  AttacherType = Attacher::AttachEngine3D
  Height = 10
  Placement = pos=(509,61,-10.5) rot=(0,1,0;1.5708rad)
  Radius = 1.1
FEATURE [Part::MultiFuse] Fusion248002175  label="Fusion248002281"
  Placement = pos=(-7,48,0) rot=(0,0,1;0rad)
  Refine = true
  Shapes = -> [Cylinder1264,Cylinder1265]
FEATURE [Part::MultiFuse] Fusion248002176  label="Fusion248002282"
  Refine = true
  Shapes = -> [Fusion248002175,Fusion248002174]
FEATURE [Part::Cut] Cut014334  label="Cut014459"
  Base = -> Cut014333
  Refine = true
  Tool = -> Fusion248002176
FEATURE [Part::Box] Box833  label="Cube1012"
  AttacherType = Attacher::AttachEngine3D
  Height = 3
  Length = 10
  Placement = pos=(502,55,-11.5) rot=(0,0,1;0rad)
  Width = 4
FEATURE [Part::Box] Box834  label="Cube1013"
  AttacherType = Attacher::AttachEngine3D
  Height = 3
  Length = 10
  Placement = pos=(502,111,-11.5) rot=(0,0,1;0rad)
  Width = 4
FEATURE [Part::MultiFuse] Fusion248002177  label="Fusion248002283"
  Placement = pos=(0,0,-1) rot=(0,0,1;0rad)
  Refine = true
  Shapes = -> [Box833,Box834]
FEATURE [Part::Fillet] Fillet007073
  Base = -> Fusion248002177
  Edges = 4 edges r=1: [Edge9,Edge10,Edge23,Edge24]
FEATURE [Part::Cut] Cut014335  label="cross-member-rear"
  Base = -> Cut014334
  Refine = true
  Tool = -> Fillet007073
FEATURE [Part::MultiFuse] Fusion248002200  label="kipper-spindle-motor"
  Placement = pos=(0.821678,0,-27.5671) rot=(0,-1,0;0.05236rad)
  Refine = true
  Shapes = -> [Cylinder1207,Cylinder059,Cylinder060,Cylinder1208]
FEATURE [Part::Box] Box835  label="Cube1014"
  AttacherType = Attacher::AttachEngine3D
  Height = 1
  Length = 10
  Placement = pos=(423,65,21) rot=(0,0,1;0rad)
  Width = 40
FEATURE [Part::Box] Box836  label="Cube1015"
  AttacherType = Attacher::AttachEngine3D
  Height = 1.5
  Length = 10
  Placement = pos=(423,65,-19) rot=(0,0,1;0rad)
  Width = 40
FEATURE [Part::Box] Box837  label="Cube1016"
  AttacherType = Attacher::AttachEngine3D
  Height = 41
  Length = 20
  Placement = pos=(413,64,-19) rot=(0,0,1;0rad)
  Width = 1
FEATURE [Part::Box] Box838  label="Cube1017"
  AttacherType = Attacher::AttachEngine3D
  Height = 41
  Length = 20
  Placement = pos=(413,105,-19) rot=(0,0,1;0rad)
  Width = 1
FEATURE [Part::MultiFuse] Fusion248002201
  Refine = true
  Shapes = -> [Box838,Box836,Box837,Box835]
FEATURE [Part::Cut] Cut014336
  Base = -> Cut014320
  Refine = true
  Tool = -> Cut026
FEATURE [Part::Cut] Cut014337
  Base = -> Cut014336
  Placement = pos=(0.66467,0,-24.5712) rot=(0,-1,0;0.05236rad)
  Refine = true
  Tool = -> Fusion248002201
FEATURE [Part::Cylinder] Cylinder1270  label="Cylinder1650"
  Angle = 360
  AttacherType = Attacher::AttachEngine3D
  Height = 4
  Placement = pos=(297,85,9) rot=(0,1,0;1.5708rad)
  Radius = 5.6
FEATURE [Part::Box] Box843  label="Cube1022"
  AttacherType = Attacher::AttachEngine3D
  Height = 8
  Length = 10
  Placement = pos=(290,65,9) rot=(0,0,1;0rad)
  Width = 40
FEATURE [Part::Cylinder] Cylinder1271  label="Cylinder1651"
  Angle = 360
  AttacherType = Attacher::AttachEngine3D
  Height = 10
  Placement = pos=(290,85,9) rot=(0,1,0;1.5708rad)
  Radius = 8
FEATURE [Part::MultiFuse] Fusion248002208
  Refine = true
  Shapes = -> [Cylinder1271,Box843]
FEATURE [Part::Cut] Cut014350
  Base = -> Fusion248002208
  Placement = pos=(-0.33396,0,-24.6235) rot=(0,-1,0;0.05236rad)
  Refine = true
  Tool = -> Cylinder1270
FEATURE [Part::Box] Box845  label="Cube1024"
  AttacherType = Attacher::AttachEngine3D
  Height = 25
  Length = 4
  Placement = pos=(286,65,-8.5) rot=(0,0,1;0rad)
  Width = 40
FEATURE [Part::Cut] Cut014351
  Base = -> Cut014350
  Refine = true
  Tool = -> Box845
FEATURE [Part::Chamfer] Chamfer182
  Base = -> Cut014351
  Edges = 2 edges r=5: [Edge6,Edge19]
FEATURE [Part::Box] Box846  label="Cube1025"
  AttacherType = Attacher::AttachEngine3D
  Height = 12.5
  Length = 15
  Placement = pos=(290,65,-0.5) rot=(0,0,1;0rad)
  Width = 8
FEATURE [Part::Box] Box847  label="Cube1026"
  AttacherType = Attacher::AttachEngine3D
  Height = 12.5
  Length = 15
  Placement = pos=(290,97,-0.5) rot=(0,0,1;0rad)
  Width = 8
FEATURE [Part::MultiFuse] Fusion248002209
  Refine = true
  Shapes = -> [Chamfer182,Box846,Box847]
FEATURE [Part::Chamfer] Chamfer183
  Base = -> Fusion248002209
  Edges = 2 edges r=3: [Edge13,Edge38]
FEATURE [Part::Cylinder] Cylinder1272  label="Cylinder1652"
  Angle = 360
  AttacherType = Attacher::AttachEngine3D
  Height = 10
  Placement = pos=(293,72,7.5) rot=(1,0,0;1.5708rad)
  Radius = 1.5
FEATURE [Part::Cylinder] Cylinder1273  label="Cylinder1653"
  Angle = 360
  AttacherType = Attacher::AttachEngine3D
  Height = 10
  Placement = pos=(302,72,7.5) rot=(1,0,0;1.5708rad)
  Radius = 1.5
FEATURE [Part::MultiFuse] Fusion248002210
  Placement = pos=(0,36,0) rot=(0,0,1;0rad)
  Refine = true
  Shapes = -> [Cylinder1272,Cylinder1273]
FEATURE [Part::Cylinder] Cylinder1274  label="Cylinder1656"
  Angle = 360
  AttacherType = Attacher::AttachEngine3D
  Height = 10
  Placement = pos=(293,72,7.5) rot=(1,0,0;1.5708rad)
  Radius = 1.5
FEATURE [Part::Cylinder] Cylinder1275  label="Cylinder1657"
  Angle = 360
  AttacherType = Attacher::AttachEngine3D
  Height = 10
  Placement = pos=(302,72,7.5) rot=(1,0,0;1.5708rad)
  Radius = 1.5
FEATURE [Part::MultiFuse] Fusion248002211
  Refine = true
  Shapes = -> [Cylinder1274,Cylinder1275]
FEATURE [Part::MultiFuse] Fusion248002212
  Refine = true
  Shapes = -> [Fusion248002210,Fusion248002211]
FEATURE [Part::Cut] Cut014352  label="kipper-motor-rod-holder_"
  Base = -> Chamfer183
  Refine = true
  Tool = -> Fusion248002212
FEATURE [Part::Box] Box848  label="Cube1027"
  AttacherType = Attacher::AttachEngine3D
  Height = 10
  Length = 30
  Placement = pos=(401,65,2) rot=(0,0,1;0rad)
  Width = 8
FEATURE [Part::Cylinder] Cylinder1276  label="Cylinder1658"
  Angle = 360
  AttacherType = Attacher::AttachEngine3D
  Height = 20
  Placement = pos=(413.02,85,-1.45848) rot=(0,1,0;1.51844rad)
  Radius = 20.5
FEATURE [Part::Box] Box849  label="Cube1028"
  AttacherType = Attacher::AttachEngine3D
  Height = 10
  Length = 30
  Placement = pos=(401,97,2) rot=(0,0,1;0rad)
  Width = 8
FEATURE [Part::MultiFuse] Fusion248002213
  Refine = true
  Shapes = -> [Box848,Box849]
FEATURE [Part::Cut] Cut014353
  Base = -> Fusion248002213
  Refine = true
  Tool = -> Cylinder1276
FEATURE [Part::MultiFuse] Fusion248002214
  Refine = true
  Shapes = -> [Cut014353,Cut014337]
FEATURE [Part::Cylinder] Cylinder1278  label="Cylinder1664"
  Angle = 360
  AttacherType = Attacher::AttachEngine3D
  Height = 10
  Placement = pos=(317,72,7.5) rot=(1,0,0;1.5708rad)
  Radius = 1.25
FEATURE [Part::Cylinder] Cylinder1279  label="Cylinder1665"
  Angle = 360
  AttacherType = Attacher::AttachEngine3D
  Height = 10
  Placement = pos=(293,72,7.5) rot=(1,0,0;1.5708rad)
  Radius = 1.25
FEATURE [Part::Cylinder] Cylinder1280  label="Cylinder1666"
  Angle = 360
  AttacherType = Attacher::AttachEngine3D
  Height = 10
  Placement = pos=(303,72,7.5) rot=(1,0,0;1.5708rad)
  Radius = 1.25
FEATURE [Part::MultiFuse] Fusion248002215
  Placement = pos=(111,1,0) rot=(0,0,1;0rad)
  Refine = true
  Shapes = -> [Cylinder1278,Cylinder1280,Cylinder1279]
FEATURE [Part::Cylinder] Cylinder1281  label="Cylinder1670"
  Angle = 360
  AttacherType = Attacher::AttachEngine3D
  Height = 10
  Placement = pos=(317,72,7.5) rot=(1,0,0;1.5708rad)
  Radius = 1.25
FEATURE [Part::Cylinder] Cylinder1282  label="Cylinder1671"
  Angle = 360
  AttacherType = Attacher::AttachEngine3D
  Height = 10
  Placement = pos=(293,72,7.5) rot=(1,0,0;1.5708rad)
  Radius = 1.25
FEATURE [Part::Cylinder] Cylinder1283  label="Cylinder1672"
  Angle = 360
  AttacherType = Attacher::AttachEngine3D
  Height = 10
  Placement = pos=(303,72,7.5) rot=(1,0,0;1.5708rad)
  Radius = 1.25
FEATURE [Part::MultiFuse] Fusion248002216
  Placement = pos=(111,35,0) rot=(0,0,1;0rad)
  Refine = true
  Shapes = -> [Cylinder1281,Cylinder1283,Cylinder1282]
FEATURE [Part::MultiFuse] Fusion248002217
  Refine = true
  Shapes = -> [Fusion248002216,Fusion248002215]
FEATURE [Part::Cut] Cut014354  label="kipper-motor-holder"
  Base = -> Fusion248002214
  Refine = true
  Tool = -> Fusion248002217
FEATURE [Part::Box] Box854  label="Cube1033"
  AttacherType = Attacher::AttachEngine3D
  Height = 10
  Length = 69
  Placement = pos=(211,105,2) rot=(0,0,1;0rad)
  Width = 10
FEATURE [Part::Box] Box855  label="Cube1034"
  AttacherType = Attacher::AttachEngine3D
  Height = 10
  Length = 69
  Placement = pos=(211,55,2) rot=(0,0,1;0rad)
  Width = 10
FEATURE [Part::MultiFuse] Fusion248002220  label="kipper-frame-ALU"
  Refine = true
  Shapes = -> [Fillet411,Box854,Box855]
FEATURE [Part::Feature] Face051
  shape: bbox 22.54 x 22.54 x 2e-07 mm, 1 faces, 0 solids (baked)
FEATURE [Part::Extrusion] Extrude  label="kipper-lifter-hex-screw-STEEL"
  Base = -> Face051
  Dir = (0,0,8)
  DirMode = 0
  FaceMakerClass = Part::FaceMakerExtrusion
  LengthFwd = 0
  LengthRev = 0
  Placement = pos=(300.627,85,0.06083) rot=(0,1,0;1.51844rad)
  Solid = false
  Symmetric = false
FEATURE [Part::Fillet] Fillet007076  label="kipper-motor-rod-holder"
  Base = -> Cut014352
  Edges = 2 edges r=4: [Edge5,Edge47]
FEATURE [App::DocumentObjectGroup] Group  label="kipper-frame"
  Group = -> [Fillet007076,Extrude,Fusion248002220,Cut014354,Fusion248002200]
FEATURE [App::DocumentObjectGroup] Group001  label="transmission"
  Group = -> [Fusion513,Fusion514,Fusion536,Cut014198]
FEATURE [App::DocumentObjectGroup] Group002  label="frame"
  Group = -> [Fusion231,Cut014335,Part__Mirroring092,Cut568]
FEATURE [App::DocumentObjectGroup] Group003  label="tools"
  Group = -> [Part__Mirroring042,Cut014106,Cut014248,Cut014249,Cut014112]
FEATURE [App::DocumentObjectGroup] Group004  label="steering"
  Group = -> [Chamfer101,Fusion677,Fillet395,Fusion692]
FEATURE [Part::Box] Box856  label="Cube1035"
  AttacherType = Attacher::AttachEngine3D
  Height = 17
  Length = 10
  Placement = pos=(360,65,-7.5) rot=(0,0,1;0rad)
  Width = 46.99
FEATURE [Part::Box] Box857  label="Cube1036"
  AttacherType = Attacher::AttachEngine3D
  Height = 17
  Length = 10
  Placement = pos=(360,55,-16.5) rot=(0,0,1;0rad)
  Width = 60
FEATURE [Part::Box] Box858  label="Cube1037"
  AttacherType = Attacher::AttachEngine3D
  Height = 17
  Length = 10
  Placement = pos=(360,69,-11.5) rot=(0,0,1;0rad)
  Width = 32
FEATURE [Part::MultiFuse] Fusion248002221
  Refine = true
  Shapes = -> [Box856,Box858]
FEATURE [Part::Cut] Cut014355
  Base = -> Box857
  Refine = true
  Tool = -> Fusion248002221
FEATURE [Part::Cylinder] Cylinder1284  label="Cylinder1673"
  Angle = 360
  AttacherType = Attacher::AttachEngine3D
  Height = 5
  Placement = pos=(370,66.5,-12) rot=(0,-1,0;1.5708rad)
  Radius = 1.1
FEATURE [Part::Cylinder] Cylinder1285  label="Cylinder1674"
  Angle = 360
  AttacherType = Attacher::AttachEngine3D
  Height = 10
  Placement = pos=(370,66.5,-12) rot=(0,-1,0;1.5708rad)
  Radius = 0.6
FEATURE [Part::Cylinder] Cylinder1286  label="Cylinder1675"
  Angle = 360
  AttacherType = Attacher::AttachEngine3D
  Height = 13.5
  Placement = pos=(361.5,68.5,-13.65) rot=(1,0,0;1.5708rad)
  Radius = 1
FEATURE [Part::Box] Box859  label="Cube1038"
  AttacherType = Attacher::AttachEngine3D
  Height = 4.5
  Length = 0.75
  Placement = pos=(360,65.5,-16.5) rot=(0,0,1;0rad)
  Width = 2
FEATURE [Part::Box] Box860  label="Cube1039"
  AttacherType = Attacher::AttachEngine3D
  Height = 3
  Length = 2
  Placement = pos=(360,65.5,-13.65) rot=(0,0,1;0rad)
  Width = 2
FEATURE [Part::Fillet] Fillet007077
  Base = -> Box860
  Edges = 2 edges r=0.9: [Edge10,Edge12]
FEATURE [Part::MultiFuse] Fusion248002222
  Refine = true
  Shapes = -> [Cylinder1286,Cylinder1284,Cylinder1285,Box859,Fillet007077]
FEATURE [Part::Cylinder] Cylinder1287  label="Cylinder1679"
  Angle = 360
  AttacherType = Attacher::AttachEngine3D
  Height = 5
  Placement = pos=(370,66.5,-12) rot=(0,-1,0;1.5708rad)
  Radius = 1.1
FEATURE [Part::Cylinder] Cylinder1288  label="Cylinder1680"
  Angle = 360
  AttacherType = Attacher::AttachEngine3D
  Height = 10
  Placement = pos=(370,66.5,-12) rot=(0,-1,0;1.5708rad)
  Radius = 0.6
FEATURE [Part::Cylinder] Cylinder1289  label="Cylinder1681"
  Angle = 360
  AttacherType = Attacher::AttachEngine3D
  Height = 13.5
  Placement = pos=(361.5,68.5,-13.65) rot=(1,0,0;1.5708rad)
  Radius = 1
FEATURE [Part::Box] Box861  label="Cube1040"
  AttacherType = Attacher::AttachEngine3D
  Height = 4.5
  Length = 0.75
  Placement = pos=(360,65.5,-16.5) rot=(0,0,1;0rad)
  Width = 2
FEATURE [Part::Box] Box862  label="Cube1041"
  AttacherType = Attacher::AttachEngine3D
  Height = 3
  Length = 2
  Placement = pos=(360,65.5,-13.65) rot=(0,0,1;0rad)
  Width = 2
FEATURE [Part::Fillet] Fillet007078
  Base = -> Box862
  Edges = 2 edges r=0.9: [Edge10,Edge12]
FEATURE [Part::MultiFuse] Fusion248002223
  Refine = true
  Shapes = -> [Cylinder1289,Cylinder1287,Cylinder1288,Box861,Fillet007078]
FEATURE [Part::Mirroring] Part__Mirroring094  label="Fusion248002223 (Mirror #12)"
  Base = (0,0,0)
  Normal = (0,1,0)
  Placement = pos=(0,170,0) rot=(0,0,1;0rad)
  Source = -> Fusion248002223
FEATURE [Part::MultiFuse] Fusion248002224
  Refine = true
  Shapes = -> [Fusion248002222,Part__Mirroring094]
FEATURE [Part::Fillet] Fillet007079
  Base = -> Cut014355
  Edges = 4 edges r=3: [Edge15,Edge30,Edge32,Edge35]
FEATURE [Part::Fillet] Fillet007080
  Base = -> Fillet007079
  Edges = 6 edges r=1.9: [Edge23,Edge26,Edge31,Edge34,Edge39,Edge42]
FEATURE [Part::Cut] Cut014356
  Base = -> Fillet007080
  Refine = true
  Tool = -> Fusion248002224
FEATURE [Part::Box] Box863  label="Cube1042"
  AttacherType = Attacher::AttachEngine3D
  Height = 17
  Length = 8
  Placement = pos=(400.5,55,-16.5) rot=(0,0,1;0rad)
  Width = 10
FEATURE [Part::Cylinder] Cylinder1292  label="Cylinder1688"
  Angle = 360
  AttacherType = Attacher::AttachEngine3D
  Height = 10
  Placement = pos=(370,66.5,-12) rot=(0,-1,0;1.5708rad)
  Radius = 0.6
FEATURE [Part::Cylinder] Cylinder1293  label="Cylinder1689"
  Angle = 360
  AttacherType = Attacher::AttachEngine3D
  Height = 5
  Placement = pos=(365,66.5,-12) rot=(0,-1,0;1.5708rad)
  Radius = 1.1
FEATURE [Part::MultiFuse] Fusion248002226
  Placement = pos=(40.5,-6,-2) rot=(0,0,1;0rad)
  Refine = true
  Shapes = -> [Cylinder1293,Cylinder1292]
FEATURE [Part::Cylinder] Cylinder1294  label="Cylinder1692"
  Angle = 360
  AttacherType = Attacher::AttachEngine3D
  Height = 10
  Placement = pos=(370,66.5,-12) rot=(0,-1,0;1.5708rad)
  Radius = 0.6
FEATURE [Part::Cylinder] Cylinder1295  label="Cylinder1693"
  Angle = 360
  AttacherType = Attacher::AttachEngine3D
  Height = 5
  Placement = pos=(365,66.5,-12) rot=(0,-1,0;1.5708rad)
  Radius = 1.1
FEATURE [Part::MultiFuse] Fusion248002227
  Placement = pos=(40.5,-6,6) rot=(0,0,1;0rad)
  Refine = true
  Shapes = -> [Cylinder1295,Cylinder1294]
FEATURE [Part::MultiFuse] Fusion248002228
  Placement = pos=(0,-0.25,2) rot=(0,0,1;0rad)
  Refine = true
  Shapes = -> [Fusion248002227,Fusion248002226]
FEATURE [Part::Fillet] Fillet007081
  Base = -> Box863
  Edges = 2 edges r=3: [Edge9,Edge10]
FEATURE [Part::Cylinder] Cylinder1296  label="Cylinder1694"
  Angle = 360
  AttacherType = Attacher::AttachEngine3D
  Height = 4
  Placement = pos=(404.5,59,-10) rot=(1,0,0;1.5708rad)
  Radius = 1.25
FEATURE [Part::Cylinder] Cylinder1297  label="Cylinder1695"
  Angle = 360
  AttacherType = Attacher::AttachEngine3D
  Height = 10
  Placement = pos=(364.5,63.5,-8) rot=(1,0,0;1.5708rad)
  Radius = 1.25
FEATURE [Part::Cylinder] Cylinder1298  label="Cylinder1696"
  Angle = 360
  AttacherType = Attacher::AttachEngine3D
  Height = 10
  Placement = pos=(366.5,116.5,-8) rot=(1,0,0;1.5708rad)
  Radius = 1.25
FEATURE [Part::MultiFuse] Fusion248002229
  Refine = true
  Shapes = -> [Cylinder1298,Cylinder1297]
FEATURE [Part::Cut] Cut014359
  Base = -> Cut014356
  Refine = true
  Tool = -> Fusion248002229
FEATURE [Part::Cylinder] Cylinder1084  label="Cylinder1410"
  Angle = 360
  AttacherType = Attacher::AttachEngine3D
  Height = 27
  Radius = 8
FEATURE [Part::Box] Box449  label="Cube675"
  AttacherType = Attacher::AttachEngine3D
  Height = 27
  Length = 10.4
  Placement = pos=(-5.2,-6.2,0) rot=(0,0,1;0rad)
  Width = 12.4
FEATURE [Part::Cylinder] Cylinder1085  label="Cylinder1411"
  Angle = 360
  AttacherType = Attacher::AttachEngine3D
  Height = 17
  Radius = 8
FEATURE [Part::Cylinder] Cylinder1086  label="Cylinder1412"
  Angle = 360
  AttacherType = Attacher::AttachEngine3D
  Height = 17
  Radius = 6.5
FEATURE [Part::Cut] Cut469
  Base = -> Cylinder1085
  Refine = true
  Tool = -> Cylinder1086
FEATURE [Part::Fillet] Fillet276
  Base = -> Box449
  Edges = 4 edges r=1: [Edge1,Edge3,Edge5,Edge7]
FEATURE [Part::Cut] Cut470
  Base = -> Cylinder1084
  Refine = true
  Tool = -> Fillet276
FEATURE [Part::MultiFuse] Fusion248002050036
  Refine = true
  Shapes = -> [Cut469,Cut470]
FEATURE [Part::Cylinder] Cylinder1087  label="Cylinder1413"
  Angle = 360
  AttacherType = Attacher::AttachEngine3D
  Height = 27
  Radius = 8
FEATURE [Part::Cut] Cut471  label="micromotor-12mm-body"
  Base = -> Cylinder1087
  Placement = pos=(175,114,18) rot=(-1,0,0;1.5708rad)
  Refine = true
  Tool = -> Fusion248002050036
FEATURE [Part::Cylinder] Cylinder1299  label="micromotor-12mm-rod"
  Angle = 360
  AttacherType = Attacher::AttachEngine3D
  Height = 9
  Placement = pos=(175,141,18) rot=(-1,0,0;1.5708rad)
  Radius = 1.5
FEATURE [Part::MultiFuse] Fusion248002050037  label="micromotor-12mm"
  Placement = pos=(607,-114.75,-26) rot=(0,0,1;1.5708rad)
  Refine = true
  Shapes = -> [Cut471,Cylinder1299]
FEATURE [Part::Cylinder] Cylinder231  label="Cylinder384"
  Angle = 360
  AttacherType = Attacher::AttachEngine3D
  Height = 27
  Radius = 8
FEATURE [Part::Box] Box432  label="Cube658"
  AttacherType = Attacher::AttachEngine3D
  Height = 27
  Length = 10.5
  Placement = pos=(-5.2,-6.2,0) rot=(0,0,1;0rad)
  Width = 12.5
FEATURE [Part::Cylinder] Cylinder232  label="Cylinder385"
  Angle = 360
  AttacherType = Attacher::AttachEngine3D
  Height = 17
  Radius = 8
FEATURE [Part::Cylinder] Cylinder233  label="Cylinder386"
  Angle = 360
  AttacherType = Attacher::AttachEngine3D
  Height = 17
  Radius = 6.5
FEATURE [Part::Cut] Cut443
  Base = -> Cylinder232
  Refine = true
  Tool = -> Cylinder233
FEATURE [Part::Fillet] Fillet272
  Base = -> Box432
  Edges = 4 edges r=1: [Edge1,Edge3,Edge5,Edge7]
FEATURE [Part::Cut] Cut444
  Base = -> Cylinder231
  Refine = true
  Tool = -> Fillet272
FEATURE [Part::MultiFuse] Fusion248002050018
  Refine = true
  Shapes = -> [Cut443,Cut444]
FEATURE [Part::Cylinder] Cylinder234  label="Cylinder387"
  Angle = 360
  AttacherType = Attacher::AttachEngine3D
  Height = 27
  Radius = 8
FEATURE [Part::Cut] Cut445  label="micromotor-12mm-TOOL"
  Base = -> Cylinder234
  Placement = pos=(491,60.3,-8.05) rot=(0.57735,-0.57735,-0.57735;2.0944rad)
  Refine = true
  Tool = -> Fusion248002050018
FEATURE [Part::Chamfer] Chamfer184  label="central-axle-lifter-cross-member"
  Base = -> Cut014359
  Edges = 2 edges r=0.4: [Edge177,Edge179]
FEATURE [Part::Cylinder] Cylinder1300  label="Cylinder1697"
  Angle = 360
  AttacherType = Attacher::AttachEngine3D
  Height = 2.5
  Placement = pos=(408.5,60.25,-8) rot=(0,-1,0;1.5708rad)
  Radius = 3.1
FEATURE [Part::Cut] Cut014360
  Base = -> Fillet007081
  Refine = true
  Tool = -> Fusion248002228
FEATURE [Part::Cut] Cut014361
  Base = -> Cut014360
  Refine = true
  Tool = -> Cylinder1300
FEATURE [Part::Cylinder] Cylinder1301  label="Cylinder1698"
  Angle = 360
  AttacherType = Attacher::AttachEngine3D
  Height = 8
  Placement = pos=(408.5,60.25,-8) rot=(0,-1,0;1.5708rad)
  Radius = 1.25
FEATURE [Part::Cut] Cut014362
  Base = -> Cut014361
  Refine = true
  Tool = -> Cylinder1301
FEATURE [Part::Cut] Cut014363  label="central-axle-lifter-middle"
  Base = -> Cut014362
  Refine = true
  Tool = -> Cylinder1296
FEATURE [Part::Box] Box864  label="Cube1043"
  AttacherType = Attacher::AttachEngine3D
  Height = 17
  Length = 36
  Placement = pos=(400.5,55,-16.5) rot=(0,0,1;0rad)
  Width = 11.5
FEATURE [Part::Fillet] Fillet007082
  Base = -> Box864
  Edges = 2 edges r=3: [Edge9,Edge10]
  Placement = pos=(59,0,0) rot=(0,0,1;0rad)
FEATURE [Part::Box] Box865  label="Cube1044"
  AttacherType = Attacher::AttachEngine3D
  Height = 12.5
  Length = 27
  Placement = pos=(464,54,-14.25) rot=(0,0,1;0rad)
  Width = 7
FEATURE [Part::Cylinder] Cylinder1302  label="Cylinder1699"
  Angle = 360
  AttacherType = Attacher::AttachEngine3D
  Height = 13
  Placement = pos=(464,60.25,-8) rot=(0,-1,0;1.5708rad)
  Radius = 4.5
FEATURE [Part::Box] Box867  label="Cube1046"
  AttacherType = Attacher::AttachEngine3D
  Height = 4
  Length = 2
  Placement = pos=(489,63,-10) rot=(0,0,1;0rad)
  Width = 7
FEATURE [Part::MultiFuse] Fusion248002050038
  Refine = true
  Shapes = -> [Box867,Box865,Cylinder1302,Cut445]
FEATURE [Part::Cut] Cut014364
  Base = -> Fillet007082
  Placement = pos=(2,0,0) rot=(0,0,1;0rad)
  Refine = true
  Tool = -> Fusion248002050038
FEATURE [Part::Cylinder] Cylinder1303  label="Cylinder1700"
  Angle = 360
  AttacherType = Attacher::AttachEngine3D
  Height = 5
  Placement = pos=(463.75,58,-3) rot=(1,0,0;1.5708rad)
  Radius = 0.8
FEATURE [Part::Cylinder] Cylinder1304  label="Cylinder1701"
  Angle = 360
  AttacherType = Attacher::AttachEngine3D
  Height = 5
  Placement = pos=(463.75,58,-13) rot=(1,0,0;1.5708rad)
  Radius = 0.8
FEATURE [Part::Cylinder] Cylinder1305  label="Cylinder1704"
  Angle = 360
  AttacherType = Attacher::AttachEngine3D
  Height = 8
  Placement = pos=(495.25,61,-3) rot=(1,0,0;1.5708rad)
  Radius = 0.8
FEATURE [Part::Cylinder] Cylinder1306  label="Cylinder1705"
  Angle = 360
  AttacherType = Attacher::AttachEngine3D
  Height = 8
  Placement = pos=(495.25,61,-13) rot=(1,0,0;1.5708rad)
  Radius = 0.8
FEATURE [Part::Cylinder] Cylinder1307  label="Cylinder1706"
  Angle = 360
  AttacherType = Attacher::AttachEngine3D
  Height = 51
  Placement = pos=(406,60.25,-8) rot=(0,1,0;1.5708rad)
  Radius = 1.5
FEATURE [Part::MultiFuse] Fusion248002050039
  Refine = true
  Shapes = -> [Cylinder1303,Cylinder1306,Cylinder1304,Cylinder1305]
FEATURE [Part::Cut] Cut014365
  Base = -> Cut014364
  Refine = true
  Tool = -> Fusion248002050039
FEATURE [Part::Cylinder] Cylinder1308  label="Cylinder1707"
  Angle = 360
  AttacherType = Attacher::AttachEngine3D
  Height = 13
  Placement = pos=(453,60.25,-8) rot=(0,1,0;1.5708rad)
  Radius = 4
FEATURE [Part::Cylinder] Cylinder1309  label="Cylinder1710"
  Angle = 360
  AttacherType = Attacher::AttachEngine3D
  Height = 2.5
  Placement = pos=(406,60.25,-8) rot=(0,1,0;1.5708rad)
  Radius = 1.5
FEATURE [Part::Cylinder] Cylinder1310  label="Cylinder1711"
  Angle = 360
  AttacherType = Attacher::AttachEngine3D
  Height = 2.5
  Placement = pos=(406,60.25,-8) rot=(0,1,0;1.5708rad)
  Radius = 3
FEATURE [Part::Cut] Cut014366  label="central-axle-lifter-leadscrew-bearing"
  Base = -> Cylinder1310
  Refine = true
  Tool = -> Cylinder1309
FEATURE [Part::Cylinder] Cylinder1311  label="Cylinder1712"
  Angle = 360
  AttacherType = Attacher::AttachEngine3D
  Height = 6
  Placement = pos=(404.5,59,-3) rot=(1,0,0;1.5708rad)
  Radius = 0.8
FEATURE [Part::Cut] Cut014367  label="central-axle-lifter-middle-01"
  Base = -> Cut014363
  Refine = true
  Tool = -> Cylinder1311
FEATURE [Part::Cylinder] Cylinder1312  label="Cylinder1713"
  Angle = 360
  AttacherType = Attacher::AttachEngine3D
  Height = 2
  Placement = pos=(408.5,62.75,-2) rot=(0,-1,0;1.5708rad)
  Radius = 2
FEATURE [Part::Cylinder] Cylinder1313  label="Cylinder1714"
  Angle = 360
  AttacherType = Attacher::AttachEngine3D
  Height = 6
  Placement = pos=(406.5,62.75,-2) rot=(0,-1,0;1.5708rad)
  Radius = 1.6
FEATURE [Part::MultiFuse] Fusion248002050041
  Refine = true
  Shapes = -> [Cylinder1312,Cylinder1313]
FEATURE [Part::Cut] Cut014368  label="central-axle-lifter-middle-02"
  Base = -> Cut014367
  Refine = true
  Tool = -> Fusion248002050041
FEATURE [Part::Box] Box868  label="Cube1047"
  AttacherType = Attacher::AttachEngine3D
  Height = 17
  Length = 8
  Placement = pos=(400.5,55,-16.5) rot=(0,0,1;0rad)
  Width = 10
FEATURE [Part::Cylinder] Cylinder1316  label="Cylinder1723"
  Angle = 360
  AttacherType = Attacher::AttachEngine3D
  Height = 10
  Placement = pos=(408.5,60.25,-12) rot=(0,-1,0;1.5708rad)
  Radius = 0.6
FEATURE [Part::Fillet] Fillet007083
  Base = -> Box868
  Edges = 2 edges r=3: [Edge9,Edge10]
  Placement = pos=(30,0,0) rot=(0,0,1;0rad)
FEATURE [Part::Cylinder] Cylinder1319  label="Cylinder1726"
  Angle = 360
  AttacherType = Attacher::AttachEngine3D
  Height = 8
  Placement = pos=(438.5,60.25,-8) rot=(0,-1,0;1.5708rad)
  Radius = 2.25
FEATURE [Part::Cylinder] Cylinder1320  label="Cylinder1727"
  Angle = 360
  AttacherType = Attacher::AttachEngine3D
  Height = 10
  Placement = pos=(408.5,60.25,-4) rot=(0,-1,0;1.5708rad)
  Radius = 0.6
FEATURE [Part::MultiFuse] Fusion248002050042
  Placement = pos=(31,0,0) rot=(0,0,1;0rad)
  Refine = true
  Shapes = -> [Cylinder1320,Cylinder1316]
FEATURE [Part::Cylinder] Cylinder1322  label="Cylinder1731"
  Angle = 360
  AttacherType = Attacher::AttachEngine3D
  Height = 10
  Placement = pos=(434.5,61.25,-4) rot=(1,0,0;1.5708rad)
  Radius = 1.8
FEATURE [Part::Cylinder] Cylinder1323  label="Cylinder1732"
  Angle = 360
  AttacherType = Attacher::AttachEngine3D
  Height = 10
  Placement = pos=(434.5,61.25,-12) rot=(1,0,0;1.5708rad)
  Radius = 1.8
FEATURE [Part::MultiFuse] Fusion248002050043
  Refine = true
  Shapes = -> [Cylinder1322,Cylinder1323]
FEATURE [Part::MultiFuse] Fusion248002050044
  Refine = true
  Shapes = -> [Fusion248002050042,Fusion248002050043]
FEATURE [Part::Cut] Cut014369
  Base = -> Fillet007083
  Refine = true
  Tool = -> Fusion248002050044
FEATURE [Part::Cut] Cut014370
  Base = -> Cut014369
  Refine = true
  Tool = -> Cylinder1319
FEATURE [Part::Chamfer] Chamfer185
  Base = -> Cut014370
  Edges = 1 edges: [Edge27 r1=5 r2=3]
FEATURE [Part::Chamfer] Chamfer186
  Base = -> Chamfer185
  Edges = 5 edges: [Edge1 r1=0.5 r2=1,Edge3 r1=0.5 r2=1,Edge5 r1=0.5 r2=1,Edge6 r1=0.5 r2=1,Edge7 r1=0.5 r2=1]
FEATURE [Part::Chamfer] Chamfer187
  Base = -> Chamfer186
  Edges = 5 edges: [Edge44 r1=1 r2=0.5,Edge46 r1=1 r2=0.5,Edge47 r1=1 r2=0.5,Edge48 r1=1 r2=0.5,Edge49 r1=1 r2=0.5]
FEATURE [Part::Box] Box869  label="Cube1048"
  AttacherType = Attacher::AttachEngine3D
  Height = 11
  Length = 38.5
  Placement = pos=(360,65,-16.5) rot=(0,0,1;0rad)
  Width = 1
FEATURE [Part::Box] Box870  label="Cube1049"
  AttacherType = Attacher::AttachEngine3D
  Height = 17
  Length = 48.5
  Placement = pos=(360,65,-16.5) rot=(0,0,1;0rad)
  Width = 1
FEATURE [Part::Box] Box872  label="Cube1051"
  AttacherType = Attacher::AttachEngine3D
  Height = 17
  Length = 7.5
  Placement = pos=(400.5,66,-16.5) rot=(0,0,1;0rad)
  Width = 6.5
FEATURE [Part::Box] Box873  label="Cube1052"
  AttacherType = Attacher::AttachEngine3D
  Height = 13
  Length = 7.5
  Placement = pos=(401.5,66,-14.5) rot=(0,0,1;0rad)
  Width = 5.5
FEATURE [Part::Box] Box874  label="Cube1053"
  AttacherType = Attacher::AttachEngine3D
  Height = 10
  Length = 7.5
  Placement = pos=(400.5,66,-13) rot=(0,0,1;0rad)
  Width = 7
FEATURE [Part::Box] Box875  label="Cube1054"
  AttacherType = Attacher::AttachEngine3D
  Height = 13
  Length = 7.5
  Placement = pos=(401.5,65.6,-14.5) rot=(0,0,1;0rad)
  Width = 5
FEATURE [Part::Box] Box876  label="Cube1055"
  AttacherType = Attacher::AttachEngine3D
  Height = 12
  Length = 7.5
  Placement = pos=(400.5,66,-13.5) rot=(0,0,1;0rad)
  Width = 5.5
FEATURE [Part::Box] Box877  label="Cube1056"
  AttacherType = Attacher::AttachEngine3D
  Height = 1.5
  Length = 1
  Placement = pos=(400.5,65.6,-11.5) rot=(0,0,1;0rad)
  Width = 2
FEATURE [Part::Box] Box879  label="Cube1058"
  AttacherType = Attacher::AttachEngine3D
  Height = 4
  Length = 4
  Placement = pos=(405.5,66,-3) rot=(0,0,1;0rad)
  Width = 7
FEATURE [Part::Cut] Cut014371
  Base = -> Box870
  Refine = true
  Tool = -> Box869
FEATURE [Part::MultiFuse] Fusion248002050057
  Refine = true
  Shapes = -> [Cut014371,Box872]
FEATURE [Part::Cut] Cut014392
  Base = -> Fusion248002050057
  Refine = true
  Tool = -> Box874
FEATURE [Part::Cut] Cut014393
  Base = -> Cut014392
  Refine = true
  Tool = -> Box876
FEATURE [Part::Cut] Cut014394
  Base = -> Cut014393
  Refine = true
  Tool = -> Box873
FEATURE [Part::Cut] Cut014395
  Base = -> Cut014394
  Refine = true
  Tool = -> Box879
FEATURE [Part::MultiFuse] Fusion248002050058
  Refine = true
  Shapes = -> [Cut014395,Box877]
FEATURE [Part::Chamfer] Chamfer196
  Base = -> Fusion248002050058
  Edges = 2 edges: [Edge25 r1=1.99 r2=5,Edge30 r1=1.99 r2=5]
FEATURE [Part::Chamfer] Chamfer197  label="central-axle-lifter-low-position-endstop-holder"
  Base = -> Chamfer196
  Edges = 1 edges: [Edge10 r1=1.99 r2=1.59]
FEATURE [Part::Box] Box888  label="Cube1067"
  AttacherType = Attacher::AttachEngine3D
  Height = 11
  Length = 38.5
  Placement = pos=(360,65,-16.5) rot=(0,0,1;0rad)
  Width = 1
FEATURE [Part::Box] Box889  label="Cube1068"
  AttacherType = Attacher::AttachEngine3D
  Height = 17
  Length = 48.5
  Placement = pos=(360,65,-16.5) rot=(0,0,1;0rad)
  Width = 1
FEATURE [Part::Box] Box890  label="Cube1069"
  AttacherType = Attacher::AttachEngine3D
  Height = 17
  Length = 7.5
  Placement = pos=(400.5,66,-16.5) rot=(0,0,1;0rad)
  Width = 5.5
FEATURE [Part::Box] Box891  label="Cube1070"
  AttacherType = Attacher::AttachEngine3D
  Height = 13
  Length = 7.5
  Placement = pos=(401.5,66,-14.5) rot=(0,0,1;0rad)
  Width = 5.5
FEATURE [Part::Box] Box892  label="central-axle-lifter-low-position-endstop-holder-01-cap"
  AttacherType = Attacher::AttachEngine3D
  Height = 17
  Length = 7.5
  Placement = pos=(400.5,71.5,-16.5) rot=(0,0,1;0rad)
  Width = 1
FEATURE [Part::Box] Box893  label="Cube1072"
  AttacherType = Attacher::AttachEngine3D
  Height = 12
  Length = 7.5
  Placement = pos=(400.5,66,-13.5) rot=(0,0,1;0rad)
  Width = 5.5
FEATURE [Part::Box] Box894  label="Cube1073"
  AttacherType = Attacher::AttachEngine3D
  Height = 1.5
  Length = 1
  Placement = pos=(400.5,65.6,-11.5) rot=(0,0,1;0rad)
  Width = 2
FEATURE [Part::Box] Box895  label="Cube1074"
  AttacherType = Attacher::AttachEngine3D
  Height = 4
  Length = 4
  Placement = pos=(405.5,66,-3) rot=(0,0,1;0rad)
  Width = 7
FEATURE [Part::Cut] Cut014396
  Base = -> Box889
  Refine = true
  Tool = -> Box888
FEATURE [Part::MultiFuse] Fusion248002050059
  Refine = true
  Shapes = -> [Box890,Cut014396]
FEATURE [Part::Cut] Cut014397
  Base = -> Fusion248002050059
  Refine = true
  Tool = -> Box893
FEATURE [Part::Cut] Cut014398
  Base = -> Cut014397
  Refine = true
  Tool = -> Box891
FEATURE [Part::Cut] Cut014399
  Base = -> Cut014398
  Refine = true
  Tool = -> Box895
FEATURE [Part::MultiFuse] Fusion248002050060
  Refine = true
  Shapes = -> [Cut014399,Box894]
FEATURE [Part::Chamfer] Chamfer198
  Base = -> Fusion248002050060
  Edges = 2 edges: [Edge26 r1=1.99 r2=5.49,Edge30 r1=1.99 r2=5.49]
FEATURE [Part::Chamfer] Chamfer199  label="central-axle-lifter-low-position-endstop-holder-01"
  Base = -> Chamfer198
  Edges = 1 edges: [Edge8 r1=1.99 r2=1.59]
FEATURE [Part::Cylinder] Cylinder1324  label="Cylinder1740"
  Angle = 360
  AttacherType = Attacher::AttachEngine3D
  Height = 6
  Placement = pos=(348.5,130.5,-9) rot=(0,0,1;0rad)
  Radius = 12.5
FEATURE [Part::Cylinder] Cylinder1325  label="Cylinder1741"
  Angle = 360
  AttacherType = Attacher::AttachEngine3D
  Height = 3
  Placement = pos=(348.5,40,-10) rot=(0,0,1;0rad)
  Radius = 10.5
FEATURE [Part::Cylinder] Cylinder1326  label="Cylinder1742"
  Angle = 360
  AttacherType = Attacher::AttachEngine3D
  Height = 1.5
  Placement = pos=(348.5,40,-8.25) rot=(0,0,1;0rad)
  Radius = 11.75
FEATURE [Part::MultiFuse] Fusion248002050061
  Placement = pos=(0,90.5,1) rot=(0,0,1;0rad)
  Refine = true
  Shapes = -> [Cylinder1326,Cylinder1325]
FEATURE [Part::Box] Box896  label="Cube1075"
  AttacherType = Attacher::AttachEngine3D
  Height = 6
  Length = 25
  Placement = pos=(336,117,-9) rot=(0,0,1;0rad)
  Width = 13.5
FEATURE [Part::Box] Box897  label="Cube1076"
  AttacherType = Attacher::AttachEngine3D
  Height = 14
  Length = 34
  Placement = pos=(328.5,116.5,-17) rot=(0,0,1;0rad)
  Width = 2
FEATURE [Part::Cylinder] Cylinder1327  label="Cylinder1743"
  Angle = 360
  AttacherType = Attacher::AttachEngine3D
  Height = 8
  Placement = pos=(348.5,130.5,-17) rot=(0,0,1;0rad)
  Radius = 13
FEATURE [Part::Cylinder] Cylinder1328  label="Cylinder1744"
  Angle = 360
  AttacherType = Attacher::AttachEngine3D
  Height = 5
  Placement = pos=(348.5,130.5,-8.5) rot=(0,0,1;0rad)
  Radius = 10.5
FEATURE [Part::Cylinder] Cylinder1329  label="Cylinder1745"
  Angle = 360
  AttacherType = Attacher::AttachEngine3D
  Height = 12
  Placement = pos=(332.5,109,-8) rot=(-1,0,0;1.5708rad)
  Radius = 1.6
FEATURE [Part::Torus] Torus019
  Angle1 = -180
  Angle2 = 180
  Angle3 = 360
  AttacherType = Attacher::AttachEngine3D
  Placement = pos=(348.5,40,-30) rot=(0,0,1;0rad)
  Radius1 = 7
  Radius2 = 5.5
FEATURE [Part::Cylinder] Cylinder1330  label="Cylinder1746"
  Angle = 360
  AttacherType = Attacher::AttachEngine3D
  Height = 1
  Placement = pos=(348.5,40,-25.5) rot=(0,0,1;0rad)
  Radius = 13
FEATURE [Part::Cylinder] Cylinder1331  label="Cylinder1747"
  Angle = 360
  AttacherType = Attacher::AttachEngine3D
  Height = 11
  Placement = pos=(348.5,40,-13.5) rot=(0,0,1;0rad)
  Radius = 8
FEATURE [Part::Cylinder] Cylinder1332  label="Cylinder1748"
  Angle = 360
  AttacherType = Attacher::AttachEngine3D
  Height = 1.5
  Placement = pos=(348.5,40,-11.5) rot=(0,0,1;0rad)
  Radius = 12.5
FEATURE [Part::Cut] Cut014400
  Base = -> Torus019
  Placement = pos=(0,0,16) rot=(0,0,1;0rad)
  Refine = true
  Tool = -> Cylinder1330
FEATURE [Part::Cut] Cut014401
  Base = -> Cylinder1332
  Refine = true
  Tool = -> Cut014400
FEATURE [Part::Cut] Cut014402
  Base = -> Cut014401
  Placement = pos=(0,90.5,1) rot=(0,0,1;0rad)
  Refine = true
  Tool = -> Cylinder1331
FEATURE [Part::Cylinder] Cylinder1333  label="Cylinder1749"
  Angle = 360
  AttacherType = Attacher::AttachEngine3D
  Height = 2.5
  Placement = pos=(348.5,40,-12.5) rot=(0,0,1;0rad)
  Radius = 12.5
FEATURE [Part::Box] Box898  label="Cube1077"
  AttacherType = Attacher::AttachEngine3D
  Height = 5
  Length = 1
  Placement = pos=(336.5,40,-15) rot=(0,0,1;0rad)
  Width = 13.5
FEATURE [Part::Chamfer] Chamfer200
  Base = -> Box898
  Edges = 1 edges: [Edge9 r1=4.99 r2=12]
FEATURE [Part::Box] Box899  label="Cube1078"
  AttacherType = Attacher::AttachEngine3D
  Height = 5
  Length = 1
  Placement = pos=(336.5,40,-15) rot=(0,0,1;0rad)
  Width = 13.5
FEATURE [Part::Chamfer] Chamfer201
  Base = -> Box899
  Edges = 1 edges: [Edge9 r1=4.99 r2=12]
  Placement = pos=(24,0,0) rot=(0,0,1;0rad)
FEATURE [Part::MultiFuse] Fusion248002050062
  Placement = pos=(-0.5,0,0) rot=(0,0,1;0rad)
  Refine = true
  Shapes = -> [Chamfer200,Chamfer201]
FEATURE [Part::Cut] Cut014403
  Base = -> Fusion248002050062
  Refine = true
  Tool = -> Cylinder1333
FEATURE [Part::Mirroring] Part__Mirroring095  label="Cut014241 (Mirror #11)001"
  Base = (0,0,0)
  Normal = (0,1,0)
  Placement = pos=(0,170,1) rot=(0,0,1;0rad)
  Source = -> Cut014403
FEATURE [Part::Cylinder] Cylinder1334  label="Cylinder1750"
  Angle = 360
  AttacherType = Attacher::AttachEngine3D
  Height = 12
  Placement = pos=(357.5,109,-8) rot=(-1,0,0;1.5708rad)
  Radius = 1.25
FEATURE [Part::MultiFuse] Fusion248002050063
  Placement = pos=(0,0,-2) rot=(0,0,1;0rad)
  Refine = true
  Shapes = -> [Cylinder1329,Cylinder1334]
FEATURE [Part::MultiFuse] Fusion248002050064
  Refine = true
  Shapes = -> [Cylinder1324,Box896]
FEATURE [Part::Cut] Cut014404
  Base = -> Fusion248002050064
  Refine = true
  Tool = -> Fusion248002050061
FEATURE [Part::Cut] Cut014405
  Base = -> Cut014404
  Refine = true
  Tool = -> Cylinder1328
FEATURE [Part::Chamfer] Chamfer202
  Base = -> Cut014405
  Edges = 1 edges r=1.2: [Edge22]
FEATURE [Part::Fillet] Fillet007084
  Base = -> Chamfer202
  Edges = 1 edges r=1: [Edge19]
FEATURE [Part::MultiFuse] Fusion248002050065
  Refine = true
  Shapes = -> [Box897,Fillet007084]
FEATURE [Part::Cut] Cut014406
  Base = -> Fusion248002050065
  Refine = true
  Tool = -> Cylinder1327
FEATURE [Part::Cut] Cut014407
  Base = -> Cut014406
  Refine = true
  Tool = -> Fusion248002050063
FEATURE [Part::MultiFuse] Fusion248002050066
  Refine = true
  Shapes = -> [Part__Mirroring095,Cut014407,Cut014402]
FEATURE [Part::Fillet] Fillet007085  label="central-axle-right-baloon-upper-retainer-01"
  Base = -> Fusion248002050066
  Edges = 2 edges r=3: [Edge2,Edge4]
  Placement = pos=(0,0,2) rot=(0,0,1;0rad)
FEATURE [Part::Cylinder] Cylinder1335  label="Cylinder1751"
  Angle = 360
  AttacherType = Attacher::AttachEngine3D
  Height = 6
  Placement = pos=(348.5,40,-9) rot=(0,0,1;0rad)
  Radius = 12.5
FEATURE [Part::Cylinder] Cylinder1336  label="Cylinder1752"
  Angle = 360
  AttacherType = Attacher::AttachEngine3D
  Height = 3
  Placement = pos=(348.5,40,-10) rot=(0,0,1;0rad)
  Radius = 10.5
FEATURE [Part::Cylinder] Cylinder1337  label="Cylinder1753"
  Angle = 360
  AttacherType = Attacher::AttachEngine3D
  Height = 1.5
  Placement = pos=(348.5,40,-8.25) rot=(0,0,1;0rad)
  Radius = 11.75
FEATURE [Part::MultiFuse] Fusion248002050067
  Placement = pos=(0,-0.5,1) rot=(0,0,1;0rad)
  Refine = true
  Shapes = -> [Cylinder1337,Cylinder1336]
FEATURE [Part::Box] Box900  label="Cube1079"
  AttacherType = Attacher::AttachEngine3D
  Height = 6
  Length = 25
  Placement = pos=(336,40,-9) rot=(0,0,1;0rad)
  Width = 13.5
FEATURE [Part::Box] Box901  label="Cube1080"
  AttacherType = Attacher::AttachEngine3D
  Height = 14
  Length = 40
  Placement = pos=(328.5,51.5,-17) rot=(0,0,1;0rad)
  Width = 2
FEATURE [Part::Cylinder] Cylinder1338  label="Cylinder1754"
  Angle = 360
  AttacherType = Attacher::AttachEngine3D
  Height = 8
  Placement = pos=(348.5,39.5,-17) rot=(0,0,1;0rad)
  Radius = 13
FEATURE [Part::Cylinder] Cylinder1339  label="Cylinder1755"
  Angle = 360
  AttacherType = Attacher::AttachEngine3D
  Height = 5
  Placement = pos=(348.5,39.5,-8.5) rot=(0,0,1;0rad)
  Radius = 10.5
FEATURE [Part::Cylinder] Cylinder1340  label="Cylinder1756"
  Angle = 360
  AttacherType = Attacher::AttachEngine3D
  Height = 12
  Placement = pos=(332.5,44,-8) rot=(-1,0,0;1.5708rad)
  Radius = 1.6
FEATURE [Part::Cylinder] Cylinder1341  label="Cylinder1757"
  Angle = 360
  AttacherType = Attacher::AttachEngine3D
  Height = 12
  Placement = pos=(364.5,44,-8) rot=(-1,0,0;1.5708rad)
  Radius = 1.6
FEATURE [Part::MultiFuse] Fusion248002050068
  Placement = pos=(0,0,-2) rot=(0,0,1;0rad)
  Refine = true
  Shapes = -> [Cylinder1341,Cylinder1340]
FEATURE [Part::Torus] Torus020
  Angle1 = -180
  Angle2 = 180
  Angle3 = 360
  AttacherType = Attacher::AttachEngine3D
  Placement = pos=(348.5,40,-30) rot=(0,0,1;0rad)
  Radius1 = 7
  Radius2 = 5.5
FEATURE [Part::Cylinder] Cylinder1342  label="Cylinder1758"
  Angle = 360
  AttacherType = Attacher::AttachEngine3D
  Height = 1
  Placement = pos=(348.5,40,-25.5) rot=(0,0,1;0rad)
  Radius = 13
FEATURE [Part::Cylinder] Cylinder1343  label="Cylinder1759"
  Angle = 360
  AttacherType = Attacher::AttachEngine3D
  Height = 11
  Placement = pos=(348.5,40,-13.5) rot=(0,0,1;0rad)
  Radius = 8
FEATURE [Part::Cylinder] Cylinder1344  label="Cylinder1760"
  Angle = 360
  AttacherType = Attacher::AttachEngine3D
  Height = 1.5
  Placement = pos=(348.5,40,-11.5) rot=(0,0,1;0rad)
  Radius = 12.5
FEATURE [Part::Cut] Cut014408
  Base = -> Torus020
  Placement = pos=(0,0,16) rot=(0,0,1;0rad)
  Refine = true
  Tool = -> Cylinder1342
FEATURE [Part::Cut] Cut014409
  Base = -> Cylinder1344
  Refine = true
  Tool = -> Cut014408
FEATURE [Part::Cut] Cut014410
  Base = -> Cut014409
  Placement = pos=(0,-0.5,1) rot=(0,0,1;0rad)
  Refine = true
  Tool = -> Cylinder1343
FEATURE [Part::Cylinder] Cylinder1345  label="Cylinder1761"
  Angle = 360
  AttacherType = Attacher::AttachEngine3D
  Height = 2.5
  Placement = pos=(348.5,39.5,-12.5) rot=(0,0,1;0rad)
  Radius = 12.5
FEATURE [Part::Box] Box902  label="Cube1081"
  AttacherType = Attacher::AttachEngine3D
  Height = 5
  Length = 1
  Placement = pos=(336.5,40,-15) rot=(0,0,1;0rad)
  Width = 13.5
FEATURE [Part::Chamfer] Chamfer203
  Base = -> Box902
  Edges = 1 edges: [Edge9 r1=4.99 r2=12]
FEATURE [Part::Box] Box903  label="Cube1082"
  AttacherType = Attacher::AttachEngine3D
  Height = 5
  Length = 1
  Placement = pos=(336.5,40,-15) rot=(0,0,1;0rad)
  Width = 13.5
FEATURE [Part::Chamfer] Chamfer204
  Base = -> Box903
  Edges = 1 edges: [Edge9 r1=4.99 r2=12]
  Placement = pos=(24,0,0) rot=(0,0,1;0rad)
FEATURE [Part::MultiFuse] Fusion248002050069
  Placement = pos=(-0.5,0,0) rot=(0,0,1;0rad)
  Refine = true
  Shapes = -> [Chamfer203,Chamfer204]
FEATURE [Part::Cut] Cut014411
  Base = -> Fusion248002050069
  Placement = pos=(0,0,1) rot=(0,0,1;0rad)
  Refine = true
  Tool = -> Cylinder1345
FEATURE [Part::MultiFuse] Fusion248002050070
  Refine = true
  Shapes = -> [Box900,Cylinder1335]
FEATURE [Part::Fillet] Fillet007086
  Base = -> Fusion248002050070
  Edges = 1 edges r=1: [Edge15]
  Placement = pos=(0,-0.5,0) rot=(0,0,1;0rad)
FEATURE [Part::MultiFuse] Fusion248002050071
  Refine = true
  Shapes = -> [Box901,Fillet007086]
FEATURE [Part::Cut] Cut014412
  Base = -> Fusion248002050071
  Refine = true
  Tool = -> Fusion248002050067
FEATURE [Part::Cut] Cut014413
  Base = -> Cut014412
  Refine = true
  Tool = -> Cylinder1339
FEATURE [Part::Cut] Cut014414
  Base = -> Cut014413
  Refine = true
  Tool = -> Cylinder1338
FEATURE [Part::MultiFuse] Fusion248002050072
  Refine = true
  Shapes = -> [Cut014410,Cut014411,Cut014414]
FEATURE [Part::Cut] Cut014415
  Base = -> Fusion248002050072
  Refine = true
  Tool = -> Fusion248002050068
FEATURE [Part::Cylinder] Cylinder1346  label="Cylinder1763"
  Angle = 360
  AttacherType = Attacher::AttachEngine3D
  Height = 5
  Placement = pos=(348.5,40,-10) rot=(0,0,1;0rad)
  Radius = 9
FEATURE [Part::Cylinder] Cylinder1347  label="Cylinder1764"
  Angle = 360
  AttacherType = Attacher::AttachEngine3D
  Height = 1
  Placement = pos=(348.5,40,-35.5) rot=(0,0,1;0rad)
  Radius = 13
FEATURE [Part::Cylinder] Cylinder1348  label="Cylinder1765"
  Angle = 360
  AttacherType = Attacher::AttachEngine3D
  Height = 1
  Placement = pos=(348.5,40,-6) rot=(0,0,1;0rad)
  Radius = 11.5
FEATURE [Part::Cylinder] Cylinder1349  label="Cylinder1766"
  Angle = 360
  AttacherType = Attacher::AttachEngine3D
  Height = 3
  Placement = pos=(348.5,40,-8) rot=(0,0,1;0rad)
  Radius = 10.5
FEATURE [Part::Cylinder] Cylinder1350  label="Cylinder1767"
  Angle = 360
  AttacherType = Attacher::AttachEngine3D
  Height = 2
  Placement = pos=(348.5,40,-34.5) rot=(0,0,1;0rad)
  Radius = 10
FEATURE [Part::Cylinder] Cylinder1351  label="Cylinder1768"
  Angle = 360
  AttacherType = Attacher::AttachEngine3D
  Height = 36
  Placement = pos=(348.5,40,-34.5) rot=(0,0,1;0rad)
  Radius = 6
FEATURE [Part::Box] Box905  label="Cube1084"
  AttacherType = Attacher::AttachEngine3D
  Height = 5
  Length = 8
  Placement = pos=(430.5,65,-13) rot=(0,0,1;0rad)
  Width = 3
FEATURE [Part::MultiFuse] Fusion248002050083  label="central-axle-lifter-leadscrew"
  Refine = true
  Shapes = -> [Cylinder1307,Cylinder1308]
FEATURE [Part::Chamfer] Chamfer205
  Base = -> Box905
  Edges = 1 edges: [Edge12 r1=4.75 r2=2.75]
  Placement = pos=(0,0,-0.5) rot=(0,0,1;0rad)
FEATURE [Part::Box] Box906  label="Cube1085"
  AttacherType = Attacher::AttachEngine3D
  Height = 17
  Length = 9
  Placement = pos=(400.5,55,-16.5) rot=(0,0,1;0rad)
  Width = 12
FEATURE [Part::Fillet] Fillet007088
  Base = -> Box906
  Edges = 2 edges r=3: [Edge9,Edge10]
  Placement = pos=(52,0,0) rot=(0,0,1;0rad)
FEATURE [Part::Cylinder] Cylinder1358  label="Cylinder1775"
  Angle = 360
  AttacherType = Attacher::AttachEngine3D
  Height = 13
  Placement = pos=(452,60.25,-8) rot=(0,1,0;1.5708rad)
  Radius = 4.5
FEATURE [Part::Cut] Cut014424
  Base = -> Fillet007088
  Refine = true
  Tool = -> Cylinder1358
FEATURE [Part::Box] Box907  label="Cube1086"
  AttacherType = Attacher::AttachEngine3D
  Height = 4
  Length = 22
  Placement = pos=(452.5,67,-16.5) rot=(0,0,1;0rad)
  Width = 4
FEATURE [Part::Cylinder] Cylinder1359  label="Cylinder1778"
  Angle = 360
  AttacherType = Attacher::AttachEngine3D
  Height = 10
  Placement = pos=(408.5,64.25,-14) rot=(0,-1,0;1.5708rad)
  Radius = 2
FEATURE [Part::Cylinder] Cylinder1360  label="Cylinder1779"
  Angle = 360
  AttacherType = Attacher::AttachEngine3D
  Height = 10
  Placement = pos=(408.5,64.25,-2) rot=(0,-1,0;1.5708rad)
  Radius = 2
FEATURE [Part::MultiFuse] Fusion248002050084
  Placement = pos=(49,0,0) rot=(0,0,1;0rad)
  Refine = true
  Shapes = -> [Cylinder1360,Cylinder1359]
FEATURE [Part::Chamfer] Chamfer207
  Base = -> Cut014415
  Edges = 1 edges r=1.2: [Edge113]
FEATURE [Part::Fillet] Fillet007089  label="central-axle-left-baloon-upper-retainer-01"
  Base = -> Chamfer207
  Edges = 4 edges r=3: [Edge105,Edge109,Edge111,Edge113]
  Placement = pos=(0,0,2) rot=(0,0,1;0rad)
FEATURE [Part::Box] Box908  label="Cube1087"
  AttacherType = Attacher::AttachEngine3D
  Height = 17
  Length = 22
  Placement = pos=(452.5,66.5,-16.5) rot=(0,0,1;0rad)
  Width = 1
FEATURE [Part::Cylinder] Cylinder1361  label="Cylinder1780"
  Angle = 360
  AttacherType = Attacher::AttachEngine3D
  Height = 5
  Placement = pos=(478.5,60,-2) rot=(0,0,1;0rad)
  Radius = 1.25
FEATURE [Part::Box] Box909  label="Cube1088"
  AttacherType = Attacher::AttachEngine3D
  Height = 2.5
  Length = 4
  Placement = pos=(493.5,59,-16.5) rot=(0,0,1;0rad)
  Width = 4
FEATURE [Part::Fillet] Fillet007090
  Base = -> Box909
  Edges = 2 edges r=1: [Edge1,Edge3]
FEATURE [Part::Cut] Cut014425
  Base = -> Cut014365
  Refine = true
  Tool = -> Cylinder1361
FEATURE [Part::Cut] Cut014426
  Base = -> Cut014425
  Refine = true
  Tool = -> Fillet007090
FEATURE [Part::Fillet] Fillet007091
  Base = -> Box907
  Edges = 2 edges r=1: [Edge11,Edge12]
FEATURE [Part::MultiFuse] Fusion248002050085
  Refine = true
  Shapes = -> [Cut014424,Box908,Fillet007091]
FEATURE [Part::Box] Box910  label="Cube1089"
  AttacherType = Attacher::AttachEngine3D
  Height = 4.2
  Length = 10.5
  Placement = pos=(461.5,66.5,-5.1) rot=(0,0,1;0rad)
  Width = 1
FEATURE [Part::Cone] Cone002
  Angle = 360
  AttacherType = Attacher::AttachEngine3D
  Height = 2
  Radius1 = 1
  Radius2 = 2.1
FEATURE [Part::Cylinder] Cylinder1362  label="Cylinder1781"
  Angle = 360
  AttacherType = Attacher::AttachEngine3D
  Height = 5
  Placement = pos=(0,0,-3) rot=(0,0,1;0rad)
  Radius = 1
FEATURE [Part::MultiFuse] Fusion248002050086  label="screw-01"
  Placement = pos=(463.75,65.5,-3) rot=(-1,0,0;1.5708rad)
  Refine = true
  Shapes = -> [Cone002,Cylinder1362]
FEATURE [Part::Chamfer] Chamfer208
  Base = -> Box910
  Edges = 2 edges: [Edge9 r1=0.55 r2=0.99,Edge10 r1=0.55 r2=0.99]
FEATURE [Part::Chamfer] Chamfer209
  Base = -> Chamfer208
  Edges = 1 edges: [Edge7 r1=0.55 r2=0.99]
FEATURE [Part::Chamfer] Chamfer210
  Base = -> Chamfer209
  Edges = 1 edges: [Edge3 r1=0.55 r2=0.99]
FEATURE [Part::Cut] Cut014427
  Base = -> Fusion248002050085
  Placement = pos=(-6,0,0) rot=(0,0,1;0rad)
  Refine = true
  Tool = -> Chamfer210
FEATURE [Part::Cylinder] Cylinder1363  label="Cylinder1782"
  Angle = 360
  AttacherType = Attacher::AttachEngine3D
  Height = 5
  Placement = pos=(463.75,67.5,-3) rot=(1,0,0;1.5708rad)
  Radius = 0.8
FEATURE [Part::Cut] Cut014428  label="central-axle-lifter-motor-holder"
  Base = -> Cut014426
  Refine = true
  Tool = -> Cylinder1363
FEATURE [Part::Cut] Cut014429
  Base = -> Cut014427
  Refine = true
  Tool = -> Fusion248002050084
FEATURE [Part::Box] Box912  label="Cube1091"
  AttacherType = Attacher::AttachEngine3D
  Height = 17
  Length = 8
  Placement = pos=(400.5,65.5,-16.5) rot=(0,0,1;0rad)
  Width = 0.5
FEATURE [Part::Box] Box913  label="Cube1092"
  AttacherType = Attacher::AttachEngine3D
  Height = 17
  Length = 7.5
  Placement = pos=(400.5,66,-16.5) rot=(0,0,1;0rad)
  Width = 6.5
FEATURE [Part::Box] Box914  label="Cube1093"
  AttacherType = Attacher::AttachEngine3D
  Height = 13
  Length = 7.5
  Placement = pos=(401.5,66,-14.5) rot=(0,0,1;0rad)
  Width = 5.5
FEATURE [Part::Box] Box915  label="Cube1094"
  AttacherType = Attacher::AttachEngine3D
  Height = 10
  Length = 7.5
  Placement = pos=(400.5,66,-13) rot=(0,0,1;0rad)
  Width = 7
FEATURE [Part::Box] Box916  label="Cube1095"
  AttacherType = Attacher::AttachEngine3D
  Height = 12
  Length = 7.5
  Placement = pos=(400.5,66,-13.5) rot=(0,0,1;0rad)
  Width = 5.5
FEATURE [Part::Box] Box917  label="Cube1096"
  AttacherType = Attacher::AttachEngine3D
  Height = 1.5
  Length = 1
  Placement = pos=(400.5,65.6,-11.5) rot=(0,0,1;0rad)
  Width = 2
FEATURE [Part::Box] Box918  label="Cube1097"
  AttacherType = Attacher::AttachEngine3D
  Height = 4
  Length = 4
  Placement = pos=(405.5,66,-3) rot=(0,0,1;0rad)
  Width = 7
FEATURE [Part::Cut] Cut014430
  Base = -> Box913
  Refine = true
  Tool = -> Box915
FEATURE [Part::Cut] Cut014431
  Base = -> Cut014430
  Refine = true
  Tool = -> Box916
FEATURE [Part::Cut] Cut014432
  Base = -> Cut014431
  Refine = true
  Tool = -> Box914
FEATURE [Part::Cut] Cut014433
  Base = -> Cut014432
  Refine = true
  Tool = -> Box918
FEATURE [Part::MultiFuse] Fusion248002050087
  Refine = true
  Shapes = -> [Box917,Cut014433,Box912]
FEATURE [Part::Mirroring] Part__Mirroring096  label="central-axle-lifter-high-position-endstop-holder"
  Base = (0,0,0)
  Normal = (1,0,0)
  Placement = pos=(884,1,0) rot=(0,0,1;0rad)
  Source = -> Fusion248002050087
FEATURE [Part::Cylinder] Cylinder1364  label="Cylinder1783"
  Angle = 360
  AttacherType = Attacher::AttachEngine3D
  Height = 15
  Placement = pos=(453.5,69,-14.5) rot=(0,1,0;1.5708rad)
  Radius = 0.8
FEATURE [Part::Cut] Cut014434  label="central-axle-lifter-high-position-endstop-lever"
  Base = -> Cut014429
  Refine = true
  Tool = -> Cylinder1364
FEATURE [App::DocumentObjectGroup] Group005  label="lifter-actuator"
  Group = -> [Fusion248002050086,Cut014428,Part__Mirroring096,Cut014434,Chamfer205,Fusion248002050083,Chamfer197,Box892,Chamfer199,Cut014368,Cut014366,Fusion248002050037,Chamfer184,Chamfer187,Box875]
FEATURE [Part::Torus] Torus033
  Angle1 = -180
  Angle2 = 180
  Angle3 = 360
  AttacherType = Attacher::AttachEngine3D
  Placement = pos=(348.5,40,-11) rot=(0,0,1;0rad)
  Radius1 = 8
  Radius2 = 4.5
FEATURE [Part::Torus] Torus034
  Angle1 = -180
  Angle2 = 180
  Angle3 = 360
  AttacherType = Attacher::AttachEngine3D
  Placement = pos=(348.5,40,-31) rot=(0,0,1;0rad)
  Radius1 = 8
  Radius2 = 4.5
FEATURE [Part::Torus] Torus035
  Angle1 = -180
  Angle2 = 180
  Angle3 = 360
  AttacherType = Attacher::AttachEngine3D
  Placement = pos=(348.5,40,-17.7) rot=(0,0,1;0rad)
  Radius1 = 8
  Radius2 = 4.5
FEATURE [Part::Torus] Torus036
  Angle1 = -180
  Angle2 = 180
  Angle3 = 360
  AttacherType = Attacher::AttachEngine3D
  Placement = pos=(348.5,40,-24.3) rot=(0,0,1;0rad)
  Radius1 = 8
  Radius2 = 4.5
FEATURE [Part::MultiFuse] Fusion248002050088
  Refine = true
  Shapes = -> [Torus033,Torus036,Torus035,Torus034]
FEATURE [Part::Torus] Torus037
  Angle1 = -180
  Angle2 = 180
  Angle3 = 360
  AttacherType = Attacher::AttachEngine3D
  Placement = pos=(348.5,40,-11) rot=(0,0,1;0rad)
  Radius1 = 8
  Radius2 = 4
FEATURE [Part::Torus] Torus038
  Angle1 = -180
  Angle2 = 180
  Angle3 = 360
  AttacherType = Attacher::AttachEngine3D
  Placement = pos=(348.5,40,-31) rot=(0,0,1;0rad)
  Radius1 = 8
  Radius2 = 4
FEATURE [Part::Torus] Torus039
  Angle1 = -180
  Angle2 = 180
  Angle3 = 360
  AttacherType = Attacher::AttachEngine3D
  Placement = pos=(348.5,40,-17.7) rot=(0,0,1;0rad)
  Radius1 = 8
  Radius2 = 4
FEATURE [Part::Torus] Torus040
  Angle1 = -180
  Angle2 = 180
  Angle3 = 360
  AttacherType = Attacher::AttachEngine3D
  Placement = pos=(348.5,40,-24.3) rot=(0,0,1;0rad)
  Radius1 = 8
  Radius2 = 4
FEATURE [Part::MultiFuse] Fusion248002050089
  Refine = true
  Shapes = -> [Torus037,Torus040,Torus039,Torus038]
FEATURE [Part::Cut] Cut014435
  Base = -> Fusion248002050088
  Refine = true
  Tool = -> Fusion248002050089
FEATURE [Part::MultiFuse] Fusion248002050090
  Refine = true
  Shapes = -> [Cut014435,Cylinder1349,Cylinder1348]
FEATURE [Part::Cut] Cut014436
  Base = -> Fusion248002050090
  Refine = true
  Tool = -> Cylinder1346
FEATURE [Part::MultiFuse] Fusion248002050091
  Refine = true
  Shapes = -> [Cylinder1350,Cut014436]
FEATURE [Part::Cut] Cut014437
  Base = -> Fusion248002050091
  Refine = true
  Tool = -> Cylinder1347
FEATURE [Part::Cut] Cut014438  label="central-axle-left-baloon-02"
  Base = -> Cut014437
  Refine = true
  Tool = -> Cylinder1351
FEATURE [Part::Cylinder] Cylinder1365  label="Cylinder1788"
  Angle = 360
  AttacherType = Attacher::AttachEngine3D
  Height = 5
  Placement = pos=(348.5,40,-10) rot=(0,0,1;0rad)
  Radius = 9
FEATURE [Part::Cylinder] Cylinder1366  label="Cylinder1789"
  Angle = 360
  AttacherType = Attacher::AttachEngine3D
  Height = 1
  Placement = pos=(348.5,40,-35.5) rot=(0,0,1;0rad)
  Radius = 13
FEATURE [Part::Cylinder] Cylinder1367  label="Cylinder1790"
  Angle = 360
  AttacherType = Attacher::AttachEngine3D
  Height = 1
  Placement = pos=(348.5,40,-6) rot=(0,0,1;0rad)
  Radius = 11.5
FEATURE [Part::Cylinder] Cylinder1368  label="Cylinder1791"
  Angle = 360
  AttacherType = Attacher::AttachEngine3D
  Height = 3
  Placement = pos=(348.5,40,-8) rot=(0,0,1;0rad)
  Radius = 10.5
FEATURE [Part::Cylinder] Cylinder1369  label="Cylinder1792"
  Angle = 360
  AttacherType = Attacher::AttachEngine3D
  Height = 2
  Placement = pos=(348.5,40,-34.5) rot=(0,0,1;0rad)
  Radius = 10
FEATURE [Part::Cylinder] Cylinder1370  label="Cylinder1793"
  Angle = 360
  AttacherType = Attacher::AttachEngine3D
  Height = 36
  Placement = pos=(348.5,40,-34.5) rot=(0,0,1;0rad)
  Radius = 6
FEATURE [Part::Torus] Torus041
  Angle1 = -180
  Angle2 = 180
  Angle3 = 360
  AttacherType = Attacher::AttachEngine3D
  Placement = pos=(348.5,40,-11) rot=(0,0,1;0rad)
  Radius1 = 8
  Radius2 = 4.5
FEATURE [Part::Torus] Torus042
  Angle1 = -180
  Angle2 = 180
  Angle3 = 360
  AttacherType = Attacher::AttachEngine3D
  Placement = pos=(348.5,40,-31) rot=(0,0,1;0rad)
  Radius1 = 8
  Radius2 = 4.5
FEATURE [Part::Torus] Torus043
  Angle1 = -180
  Angle2 = 180
  Angle3 = 360
  AttacherType = Attacher::AttachEngine3D
  Placement = pos=(348.5,40,-17.7) rot=(0,0,1;0rad)
  Radius1 = 8
  Radius2 = 4.5
FEATURE [Part::Torus] Torus044
  Angle1 = -180
  Angle2 = 180
  Angle3 = 360
  AttacherType = Attacher::AttachEngine3D
  Placement = pos=(348.5,40,-24.3) rot=(0,0,1;0rad)
  Radius1 = 8
  Radius2 = 4.5
FEATURE [Part::MultiFuse] Fusion248002050092
  Refine = true
  Shapes = -> [Torus041,Torus044,Torus043,Torus042]
FEATURE [Part::Torus] Torus045
  Angle1 = -180
  Angle2 = 180
  Angle3 = 360
  AttacherType = Attacher::AttachEngine3D
  Placement = pos=(348.5,40,-11) rot=(0,0,1;0rad)
  Radius1 = 8
  Radius2 = 4
FEATURE [Part::Torus] Torus046
  Angle1 = -180
  Angle2 = 180
  Angle3 = 360
  AttacherType = Attacher::AttachEngine3D
  Placement = pos=(348.5,40,-31) rot=(0,0,1;0rad)
  Radius1 = 8
  Radius2 = 4
FEATURE [Part::Torus] Torus047
  Angle1 = -180
  Angle2 = 180
  Angle3 = 360
  AttacherType = Attacher::AttachEngine3D
  Placement = pos=(348.5,40,-17.7) rot=(0,0,1;0rad)
  Radius1 = 8
  Radius2 = 4
FEATURE [Part::Torus] Torus048
  Angle1 = -180
  Angle2 = 180
  Angle3 = 360
  AttacherType = Attacher::AttachEngine3D
  Placement = pos=(348.5,40,-24.3) rot=(0,0,1;0rad)
  Radius1 = 8
  Radius2 = 4
FEATURE [Part::MultiFuse] Fusion248002050093
  Refine = true
  Shapes = -> [Torus045,Torus048,Torus047,Torus046]
FEATURE [Part::Cut] Cut014439
  Base = -> Fusion248002050092
  Refine = true
  Tool = -> Fusion248002050093
FEATURE [Part::MultiFuse] Fusion248002050094
  Refine = true
  Shapes = -> [Cut014439,Cylinder1368,Cylinder1367]
FEATURE [Part::Cut] Cut014440
  Base = -> Fusion248002050094
  Refine = true
  Tool = -> Cylinder1365
FEATURE [Part::MultiFuse] Fusion248002050095
  Refine = true
  Shapes = -> [Cylinder1369,Cut014440]
FEATURE [Part::Cut] Cut014441
  Base = -> Fusion248002050095
  Refine = true
  Tool = -> Cylinder1366
FEATURE [Part::Cut] Cut014442  label="central-axle-right-baloon-02"
  Base = -> Cut014441
  Placement = pos=(0,90,0) rot=(0,0,1;0rad)
  Refine = true
  Tool = -> Cylinder1370
FEATURE [Part::Box] Box919  label="Cube1098"
  AttacherType = Attacher::AttachEngine3D
  Height = 17
  Length = 8
  Placement = pos=(400.5,55,-16.5) rot=(0,0,1;0rad)
  Width = 10
FEATURE [Part::Cylinder] Cylinder1371  label="Cylinder1794"
  Angle = 360
  AttacherType = Attacher::AttachEngine3D
  Height = 10
  Placement = pos=(408.5,60.25,-12) rot=(0,-1,0;1.5708rad)
  Radius = 0.75
FEATURE [Part::Fillet] Fillet007092
  Base = -> Box919
  Edges = 2 edges r=3: [Edge9,Edge10]
  Placement = pos=(30,0,0) rot=(0,0,1;0rad)
FEATURE [Part::Cylinder] Cylinder1372  label="Cylinder1795"
  Angle = 360
  AttacherType = Attacher::AttachEngine3D
  Height = 8
  Placement = pos=(438.5,60.25,-8) rot=(0,-1,0;1.5708rad)
  Radius = 2.25
FEATURE [Part::Cylinder] Cylinder1373  label="Cylinder1796"
  Angle = 360
  AttacherType = Attacher::AttachEngine3D
  Height = 10
  Placement = pos=(408.5,60.25,-4) rot=(0,-1,0;1.5708rad)
  Radius = 0.75
FEATURE [Part::MultiFuse] Fusion248002050096
  Placement = pos=(45.4103,181.252,0) rot=(0,0,1;5.8294rad)
  Refine = true
  Shapes = -> [Cylinder1373,Cylinder1371]
FEATURE [Part::Cylinder] Cylinder1374  label="Cylinder1797"
  Angle = 360
  AttacherType = Attacher::AttachEngine3D
  Height = 10
  Placement = pos=(434.5,61.25,-4) rot=(1,0,0;1.5708rad)
  Radius = 1.25
FEATURE [Part::Cylinder] Cylinder1375  label="Cylinder1798"
  Angle = 360
  AttacherType = Attacher::AttachEngine3D
  Height = 10
  Placement = pos=(432.5,63,-12) rot=(1,0,0;1.5708rad)
  Radius = 0.9
FEATURE [Part::MultiFuse] Fusion248002050097
  Placement = pos=(0,6,0) rot=(0,0,1;0rad)
  Refine = true
  Shapes = -> [Cylinder1374,Cylinder1375]
FEATURE [Part::Cut] Cut014443
  Base = -> Fillet007092
  Refine = true
  Tool = -> Cylinder1372
FEATURE [Part::Cylinder] Cylinder1376  label="Cylinder1799"
  Angle = 360
  AttacherType = Attacher::AttachEngine3D
  Height = 10
  Placement = pos=(430.5,60.5,0) rot=(0,0,1;0rad)
  Radius = 2
FEATURE [Part::Cut] Cut014444
  Base = -> Cut014443
  Refine = true
  Tool = -> Fusion248002050096
FEATURE [Part::Cut] Cut014445
  Base = -> Cut014444
  Refine = true
  Tool = -> Fusion248002050097
FEATURE [Part::Chamfer] Chamfer211
  Base = -> Cut014445
  Edges = 3 edges: [Edge10 r1=1 r2=0.5,Edge18 r1=1 r2=0.5,Edge20 r1=1 r2=0.5]
FEATURE [Part::Chamfer] Chamfer212
  Base = -> Chamfer211
  Edges = 3 edges: [Edge3 r1=1 r2=0.5,Edge12 r1=1 r2=0.5,Edge13 r1=1 r2=0.5]
FEATURE [Part::Chamfer] Chamfer213
  Base = -> Chamfer212
  Edges = 1 edges: [Edge23 r1=5 r2=3]
FEATURE [Part::Box] Box920  label="Cube1099"
  AttacherType = Attacher::AttachEngine3D
  Height = 10
  Length = 1
  Placement = pos=(437.5,55.75,-13) rot=(0,0,1;0rad)
  Width = 2
FEATURE [Part::Cut] Cut014446
  Base = -> Chamfer213
  Refine = true
  Tool = -> Box920
